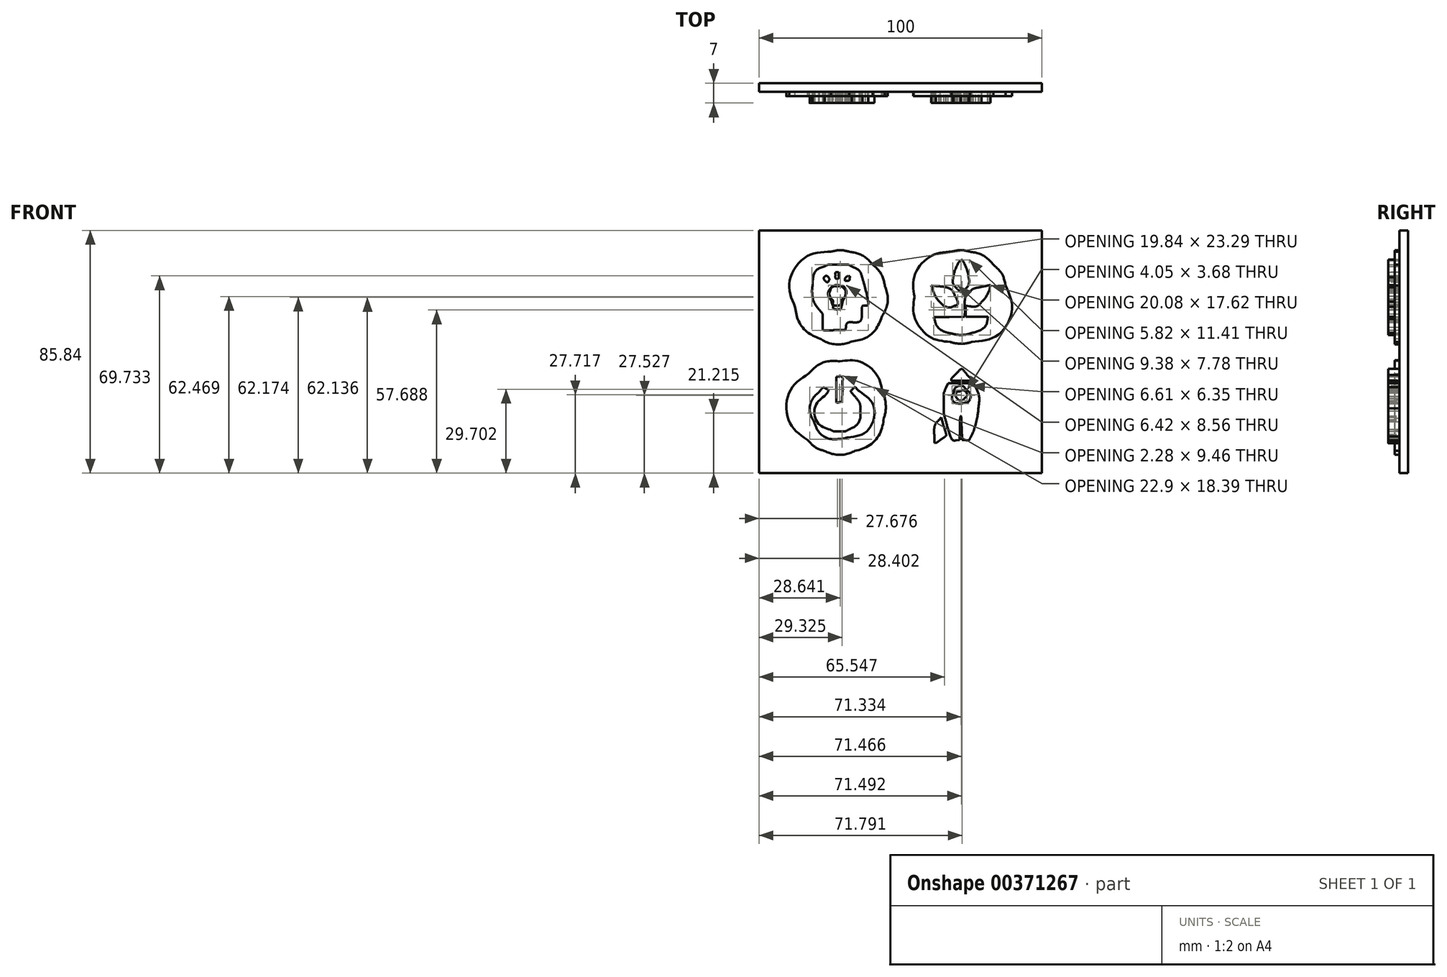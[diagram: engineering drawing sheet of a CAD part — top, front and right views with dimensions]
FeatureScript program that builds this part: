
annotation { "Feature Type Name" : "Feature", "Feature Type Description" : "" }
export const myFeature = defineFeature(function(context is Context, id is Id, definition is map)
    precondition{}
    {
        {
            var Q0;
            Q0=qCreatedBy(makeId("Front.planeOp"),FACE);
            var sketch = newSketch(context, id + "F0", { "sketchPlane" : qUnion([Q0])});
            skFitSpline(sketch, "E0", {"points": [v(-58.7, -58.7) * mm, v(-59.54, -57.85) * mm, v(-59.7, -57.5) * mm, v(-59.68, -56.5) * mm]});
            skLineSegment(sketch, "E1", {"start": v(-59.68, -56.5) * mm, "end": v(-59.65, -55.31) * mm});
            skLineSegment(sketch, "E2", {"start": v(-59.65, -55.31) * mm, "end": v(-59.39, -56.23) * mm});
            skFitSpline(sketch, "E3", {"points": [v(-59.39, -56.23) * mm, v(-59.05, -57.4) * mm, v(-57.42, -59.03) * mm, v(-56.24, -59.37) * mm]});
            skLineSegment(sketch, "E4", {"start": v(-56.24, -59.37) * mm, "end": v(-55.33, -59.64) * mm});
            skLineSegment(sketch, "E5", {"start": v(-55.33, -59.64) * mm, "end": v(-56.52, -59.66) * mm});
            skFitSpline(sketch, "E6", {"points": [v(-56.52, -59.66) * mm, v(-57.52, -59.68) * mm, v(-57.86, -59.53) * mm, v(-58.7, -58.7) * mm]});
            skFitSpline(sketch, "E7", {"points": [v(56.22, -59.37) * mm, v(56.72, -59.23) * mm, v(57.58, -58.67) * mm, v(58.12, -58.13) * mm]});
            skFitSpline(sketch, "E8", {"points": [v(58.12, -58.13) * mm, v(58.66, -57.59) * mm, v(59.22, -56.73) * mm, v(59.36, -56.23) * mm]});
            skLineSegment(sketch, "E9", {"start": v(59.36, -56.23) * mm, "end": v(59.63, -55.31) * mm});
            skLineSegment(sketch, "E10", {"start": v(59.63, -55.31) * mm, "end": v(59.65, -56.5) * mm});
            skFitSpline(sketch, "E11", {"points": [v(59.65, -56.5) * mm, v(59.67, -57.5) * mm, v(59.52, -57.85) * mm, v(58.68, -58.7) * mm]});
            skFitSpline(sketch, "E12", {"points": [v(58.68, -58.7) * mm, v(57.84, -59.53) * mm, v(57.5, -59.68) * mm, v(56.5, -59.66) * mm]});
            skLineSegment(sketch, "E13", {"start": v(56.5, -59.66) * mm, "end": v(55.3, -59.64) * mm});
            skLineSegment(sketch, "E14", {"start": v(55.3, -59.64) * mm, "end": v(56.22, -59.37) * mm});
            skFitSpline(sketch, "E15", {"points": [v(-25.98, -48.72) * mm, v(-28.66, -47.95) * mm, v(-31.18, -46.46) * mm, v(-33.19, -44.46) * mm]});
            skFitSpline(sketch, "E16", {"points": [v(-33.19, -44.46) * mm, v(-35.29, -42.37) * mm, v(-36.5, -40.4) * mm, v(-37.45, -37.53) * mm]});
            skFitSpline(sketch, "E17", {"points": [v(-37.45, -37.53) * mm, v(-38.36, -34.76) * mm, v(-38.36, -29.9) * mm, v(-37.43, -27.23) * mm]});
            skFitSpline(sketch, "E18", {"points": [v(-37.43, -27.23) * mm, v(-36.45, -24.4) * mm, v(-35.23, -22.47) * mm, v(-33.05, -20.32) * mm]});
            skFitSpline(sketch, "E19", {"points": [v(-33.05, -20.32) * mm, v(-29.86, -17.16) * mm, v(-26.18, -15.66) * mm, v(-21.6, -15.66) * mm]});
            skFitSpline(sketch, "E20", {"points": [v(-21.6, -15.66) * mm, v(-16.86, -15.66) * mm, v(-13.33, -17.12) * mm, v(-9.96, -20.48) * mm]});
            skFitSpline(sketch, "E21", {"points": [v(-9.96, -20.48) * mm, v(-6.62, -23.8) * mm, v(-4.95, -27.8) * mm, v(-4.95, -32.45) * mm]});
            skFitSpline(sketch, "E22", {"points": [v(-4.95, -32.45) * mm, v(-4.95, -40.1) * mm, v(-10.21, -46.96) * mm, v(-17.5, -48.82) * mm]});
            skFitSpline(sketch, "E23", {"points": [v(-17.5, -48.82) * mm, v(-19.73, -49.39) * mm, v(-23.82, -49.34) * mm, v(-25.98, -48.72) * mm]});
            skLineSegment(sketch, "E24", {"start": v(-25.98, -48.72) * mm, "end": v(-25.98, -48.72) * mm});
            skFitSpline(sketch, "E25", {"points": [v(-16.12, -47.82) * mm, v(-11.18, -45.97) * mm, v(-7.23, -41.5) * mm, v(-5.9, -36.27) * mm]});
            skFitSpline(sketch, "E26", {"points": [v(-5.9, -36.27) * mm, v(-5.29, -33.8) * mm, v(-5.5, -29.47) * mm, v(-6.36, -27.03) * mm]});
            skFitSpline(sketch, "E27", {"points": [v(-6.36, -27.03) * mm, v(-8.6, -20.64) * mm, v(-14.77, -16.18) * mm, v(-21.42, -16.16) * mm]});
            skFitSpline(sketch, "E28", {"points": [v(-21.42, -16.16) * mm, v(-25.68, -16.15) * mm, v(-29.35, -17.6) * mm, v(-32.46, -20.5) * mm]});
            skFitSpline(sketch, "E29", {"points": [v(-32.46, -20.5) * mm, v(-39.17, -26.79) * mm, v(-39.37, -37.44) * mm, v(-32.91, -43.9) * mm]});
            skFitSpline(sketch, "E30", {"points": [v(-32.91, -43.9) * mm, v(-30.85, -45.96) * mm, v(-29.24, -47) * mm, v(-26.78, -47.88) * mm]});
            skFitSpline(sketch, "E31", {"points": [v(-26.78, -47.88) * mm, v(-23.57, -49) * mm, v(-19.23, -48.98) * mm, v(-16.12, -47.82) * mm]});
            skFitSpline(sketch, "E32", {"points": [v(-23.93, -43.88) * mm, v(-26.91, -43.13) * mm, v(-29.78, -40.69) * mm, v(-31.13, -37.74) * mm]});
            skFitSpline(sketch, "E33", {"points": [v(-31.13, -37.74) * mm, v(-31.75, -36.39) * mm, v(-31.87, -35.7) * mm, v(-31.89, -33.58) * mm]});
            skFitSpline(sketch, "E34", {"points": [v(-31.89, -33.58) * mm, v(-31.9, -31.26) * mm, v(-31.82, -30.87) * mm, v(-30.99, -29.17) * mm]});
            skFitSpline(sketch, "E35", {"points": [v(-30.99, -29.17) * mm, v(-30.02, -27.21) * mm, v(-27.91, -24.98) * mm, v(-27.03, -24.98) * mm]});
            skFitSpline(sketch, "E36", {"points": [v(-27.03, -24.98) * mm, v(-26.75, -24.98) * mm, v(-26.24, -25.17) * mm, v(-25.9, -25.41) * mm]});
            skFitSpline(sketch, "E37", {"points": [v(-25.9, -25.41) * mm, v(-24.95, -26.08) * mm, v(-25.08, -27.3) * mm, v(-26.22, -28.57) * mm]});
            skFitSpline(sketch, "E38", {"points": [v(-26.22, -28.57) * mm, v(-27.8, -30.34) * mm, v(-28.22, -31.39) * mm, v(-28.22, -33.58) * mm]});
            skFitSpline(sketch, "E39", {"points": [v(-28.22, -33.58) * mm, v(-28.22, -36.4) * mm, v(-27.01, -38.46) * mm, v(-24.64, -39.68) * mm]});
            skFitSpline(sketch, "E40", {"points": [v(-24.64, -39.68) * mm, v(-20.27, -41.93) * mm, v(-14.86, -38.73) * mm, v(-14.83, -33.9) * mm]});
            skFitSpline(sketch, "E41", {"points": [v(-14.83, -33.9) * mm, v(-14.83, -31.88) * mm, v(-15.31, -30.57) * mm, v(-16.7, -28.88) * mm]});
            skFitSpline(sketch, "E42", {"points": [v(-16.7, -28.88) * mm, v(-18.06, -27.23) * mm, v(-18.22, -26.4) * mm, v(-17.37, -25.54) * mm]});
            skFitSpline(sketch, "E43", {"points": [v(-17.37, -25.54) * mm, v(-16.46, -24.64) * mm, v(-15.64, -24.84) * mm, v(-14.23, -26.32) * mm]});
            skFitSpline(sketch, "E44", {"points": [v(-14.23, -26.32) * mm, v(-12.61, -28.01) * mm, v(-12.17, -28.74) * mm, v(-11.6, -30.62) * mm]});
            skFitSpline(sketch, "E45", {"points": [v(-11.6, -30.62) * mm, v(-10.12, -35.63) * mm, v(-12.51, -40.87) * mm, v(-17.3, -43.11) * mm]});
            skFitSpline(sketch, "E46", {"points": [v(-17.3, -43.11) * mm, v(-19.3, -44.05) * mm, v(-22.01, -44.36) * mm, v(-23.93, -43.88) * mm]});
            skFitSpline(sketch, "E47", {"points": [v(-18.7, -43.01) * mm, v(-11.6, -40.62) * mm, v(-9.47, -32.06) * mm, v(-14.63, -26.74) * mm]});
            skFitSpline(sketch, "E48", {"points": [v(-14.63, -26.74) * mm, v(-15.9, -25.43) * mm, v(-16.25, -25.31) * mm, v(-16.92, -25.98) * mm]});
            skFitSpline(sketch, "E49", {"points": [v(-16.92, -25.98) * mm, v(-17.58, -26.64) * mm, v(-17.49, -26.95) * mm, v(-16.14, -28.6) * mm]});
            skFitSpline(sketch, "E50", {"points": [v(-16.14, -28.6) * mm, v(-14.75, -30.3) * mm, v(-14.26, -31.6) * mm, v(-14.26, -33.64) * mm]});
            skFitSpline(sketch, "E51", {"points": [v(-14.26, -33.64) * mm, v(-14.26, -36.4) * mm, v(-15.67, -38.8) * mm, v(-18.03, -40.11) * mm]});
            skFitSpline(sketch, "E52", {"points": [v(-18.03, -40.11) * mm, v(-19.27, -40.8) * mm, v(-19.8, -40.92) * mm, v(-21.6, -40.91) * mm]});
            skFitSpline(sketch, "E53", {"points": [v(-21.6, -40.91) * mm, v(-23.22, -40.9) * mm, v(-23.99, -40.76) * mm, v(-24.85, -40.3) * mm]});
            skFitSpline(sketch, "E54", {"points": [v(-24.85, -40.3) * mm, v(-29.26, -37.95) * mm, v(-30.25, -32.3) * mm, v(-26.94, -28.47) * mm]});
            skFitSpline(sketch, "E55", {"points": [v(-26.94, -28.47) * mm, v(-25.71, -27.06) * mm, v(-25.55, -26.27) * mm, v(-26.4, -25.82) * mm]});
            skFitSpline(sketch, "E56", {"points": [v(-26.4, -25.82) * mm, v(-27.12, -25.44) * mm, v(-27.72, -25.75) * mm, v(-28.94, -27.14) * mm]});
            skFitSpline(sketch, "E57", {"points": [v(-28.94, -27.14) * mm, v(-31.39, -29.92) * mm, v(-32.05, -34.14) * mm, v(-30.56, -37.44) * mm]});
            skFitSpline(sketch, "E58", {"points": [v(-30.56, -37.44) * mm, v(-28.9, -41.1) * mm, v(-25.4, -43.47) * mm, v(-21.52, -43.57) * mm]});
            skFitSpline(sketch, "E59", {"points": [v(-21.52, -43.57) * mm, v(-20.93, -43.59) * mm, v(-19.67, -43.34) * mm, v(-18.7, -43.01) * mm]});
            skFitSpline(sketch, "E60", {"points": [v(-22.83, -30.67) * mm, v(-23.22, -30.24) * mm, v(-23.3, -29.47) * mm, v(-23.3, -26.01) * mm]});
            skFitSpline(sketch, "E61", {"points": [v(-23.3, -26.01) * mm, v(-23.3, -22.25) * mm, v(-23.24, -21.82) * mm, v(-22.73, -21.3) * mm]});
            skFitSpline(sketch, "E62", {"points": [v(-22.73, -21.3) * mm, v(-22.03, -20.6) * mm, v(-20.99, -20.58) * mm, v(-20.38, -21.26) * mm]});
            skFitSpline(sketch, "E63", {"points": [v(-20.38, -21.26) * mm, v(-19.7, -22) * mm, v(-19.68, -30.07) * mm, v(-20.35, -30.74) * mm]});
            skFitSpline(sketch, "E64", {"points": [v(-20.35, -30.74) * mm, v(-20.95, -31.34) * mm, v(-22.25, -31.3) * mm, v(-22.83, -30.67) * mm]});
            skLineSegment(sketch, "E65", {"start": v(-22.83, -30.67) * mm, "end": v(-22.83, -30.67) * mm});
            skFitSpline(sketch, "E66", {"points": [v(-20.54, -26.22) * mm, v(-20.47, -22.64) * mm, v(-20.53, -21.9) * mm, v(-20.9, -21.59) * mm]});
            skFitSpline(sketch, "E67", {"points": [v(-20.9, -21.59) * mm, v(-21.23, -21.3) * mm, v(-21.5, -21.3) * mm, v(-22.03, -21.54) * mm]});
            skFitSpline(sketch, "E68", {"points": [v(-22.03, -21.54) * mm, v(-22.73, -21.86) * mm, v(-22.73, -21.88) * mm, v(-22.73, -25.9) * mm]});
            skFitSpline(sketch, "E69", {"points": [v(-22.73, -25.9) * mm, v(-22.73, -30.25) * mm, v(-22.6, -30.7) * mm, v(-21.32, -30.56) * mm]});
            skLineSegment(sketch, "E70", {"start": v(-21.32, -30.56) * mm, "end": v(-20.61, -30.48) * mm});
            skLineSegment(sketch, "E71", {"start": v(-20.61, -30.48) * mm, "end": v(-20.54, -26.22) * mm});
            skFitSpline(sketch, "E72", {"points": [v(17.06, -48.8) * mm, v(11.27, -47.27) * mm, v(6.44, -42.41) * mm, v(5.04, -36.7) * mm]});
            skFitSpline(sketch, "E73", {"points": [v(5.04, -36.7) * mm, v(4.1, -32.91) * mm, v(4.57, -28.18) * mm, v(6.19, -25) * mm]});
            skFitSpline(sketch, "E74", {"points": [v(6.19, -25) * mm, v(9.14, -19.16) * mm, v(14.82, -15.66) * mm, v(21.29, -15.67) * mm]});
            skFitSpline(sketch, "E75", {"points": [v(21.29, -15.67) * mm, v(26.13, -15.67) * mm, v(29.94, -17.24) * mm, v(33.3, -20.6) * mm]});
            skFitSpline(sketch, "E76", {"points": [v(33.3, -20.6) * mm, v(39.88, -27.18) * mm, v(39.86, -37.72) * mm, v(33.27, -44.35) * mm]});
            skFitSpline(sketch, "E77", {"points": [v(33.27, -44.35) * mm, v(31.06, -46.57) * mm, v(27.84, -48.36) * mm, v(25.02, -48.94) * mm]});
            skFitSpline(sketch, "E78", {"points": [v(25.02, -48.94) * mm, v(22.96, -49.36) * mm, v(18.93, -49.3) * mm, v(17.06, -48.8) * mm]});
            skFitSpline(sketch, "E79", {"points": [v(27.02, -47.73) * mm, v(34.74, -44.82) * mm, v(39.11, -36.66) * mm, v(37.23, -28.67) * mm]});
            skFitSpline(sketch, "E80", {"points": [v(37.23, -28.67) * mm, v(36.18, -24.21) * mm, v(32.7, -19.85) * mm, v(28.63, -17.87) * mm]});
            skFitSpline(sketch, "E81", {"points": [v(28.63, -17.87) * mm, v(25.96, -16.58) * mm, v(24.06, -16.14) * mm, v(21.14, -16.16) * mm]});
            skFitSpline(sketch, "E82", {"points": [v(21.14, -16.16) * mm, v(11.14, -16.2) * mm, v(3.3, -25.76) * mm, v(5.32, -35.42) * mm]});
            skFitSpline(sketch, "E83", {"points": [v(5.32, -35.42) * mm, v(7.42, -45.46) * mm, v(17.64, -51.26) * mm, v(27.02, -47.73) * mm]});
            skFitSpline(sketch, "E84", {"points": [v(11.53, -44.94) * mm, v(11.07, -43.55) * mm, v(11.32, -39.84) * mm, v(11.96, -38.34) * mm]});
            skFitSpline(sketch, "E85", {"points": [v(11.96, -38.34) * mm, v(12.66, -36.74) * mm, v(14, -35.27) * mm, v(14.58, -35.49) * mm]});
            skFitSpline(sketch, "E86", {"points": [v(14.58, -35.49) * mm, v(14.95, -35.63) * mm, v(16.47, -40.39) * mm, v(16.68, -42.05) * mm]});
            skFitSpline(sketch, "E87", {"points": [v(16.68, -42.05) * mm, v(16.78, -42.82) * mm, v(16.62, -43.01) * mm, v(14.82, -44.24) * mm]});
            skFitSpline(sketch, "E88", {"points": [v(14.82, -44.24) * mm, v(12.62, -45.73) * mm, v(11.84, -45.9) * mm, v(11.53, -44.94) * mm]});
            skFitSpline(sketch, "E89", {"points": [v(14.42, -43.7) * mm, v(15.69, -42.8) * mm, v(16.22, -42.25) * mm, v(16.13, -41.94) * mm]});
            skFitSpline(sketch, "E90", {"points": [v(16.13, -41.94) * mm, v(16.05, -41.69) * mm, v(15.63, -40.23) * mm, v(15.2, -38.7) * mm]});
            skLineSegment(sketch, "E91", {"start": v(15.2, -38.7) * mm, "end": v(14.4, -35.92) * mm});
            skLineSegment(sketch, "E92", {"start": v(14.4, -35.92) * mm, "end": v(13.47, -36.99) * mm});
            skFitSpline(sketch, "E93", {"points": [v(13.47, -36.99) * mm, v(12.33, -38.3) * mm, v(11.92, -39.74) * mm, v(11.92, -42.38) * mm]});
            skFitSpline(sketch, "E94", {"points": [v(11.92, -42.38) * mm, v(11.92, -44.24) * mm, v(12.07, -45.01) * mm, v(12.44, -45.01) * mm]});
            skFitSpline(sketch, "E95", {"points": [v(12.44, -45.01) * mm, v(12.52, -45.01) * mm, v(13.41, -44.42) * mm, v(14.42, -43.7) * mm]});
            skFitSpline(sketch, "E96", {"points": [v(27.82, -44.13) * mm, v(26.16, -42.96) * mm, v(25.79, -42.57) * mm, v(25.9, -42.08) * mm]});
            skFitSpline(sketch, "E97", {"points": [v(25.9, -42.08) * mm, v(26, -41.57) * mm, v(27.35, -36.77) * mm, v(27.66, -35.77) * mm]});
            skFitSpline(sketch, "E98", {"points": [v(27.66, -35.77) * mm, v(27.98, -34.75) * mm, v(29.6, -36) * mm, v(30.69, -38.1) * mm]});
            skFitSpline(sketch, "E99", {"points": [v(30.69, -38.1) * mm, v(31.37, -39.42) * mm, v(31.7, -43.55) * mm, v(31.2, -44.8) * mm]});
            skFitSpline(sketch, "E100", {"points": [v(31.2, -44.8) * mm, v(30.78, -45.9) * mm, v(30.17, -45.78) * mm, v(27.82, -44.13) * mm]});
            skFitSpline(sketch, "E101", {"points": [v(30.77, -43.72) * mm, v(31.03, -41.97) * mm, v(30.72, -39.55) * mm, v(30.06, -38.29) * mm]});
            skFitSpline(sketch, "E102", {"points": [v(30.06, -38.29) * mm, v(29.45, -37.1) * mm, v(28.27, -35.76) * mm, v(28.18, -36.15) * mm]});
            skFitSpline(sketch, "E103", {"points": [v(28.18, -36.15) * mm, v(27.97, -37.03) * mm, v(26.67, -41.56) * mm, v(26.53, -41.94) * mm]});
            skFitSpline(sketch, "E104", {"points": [v(26.53, -41.94) * mm, v(26.4, -42.26) * mm, v(26.87, -42.74) * mm, v(28.25, -43.7) * mm]});
            skFitSpline(sketch, "E105", {"points": [v(28.25, -43.7) * mm, v(29.3, -44.42) * mm, v(30.25, -45.01) * mm, v(30.37, -45.01) * mm]});
            skFitSpline(sketch, "E106", {"points": [v(30.37, -45.01) * mm, v(30.48, -45.01) * mm, v(30.66, -44.43) * mm, v(30.77, -43.72) * mm]});
            skFitSpline(sketch, "E107", {"points": [v(18.27, -43.83) * mm, v(17.92, -43.38) * mm, v(16.7, -39.78) * mm, v(15.86, -36.69) * mm]});
            skFitSpline(sketch, "E108", {"points": [v(15.86, -36.69) * mm, v(15.38, -34.94) * mm, v(15.24, -33.63) * mm, v(15.24, -30.9) * mm]});
            skFitSpline(sketch, "E109", {"points": [v(15.24, -30.9) * mm, v(15.23, -27.6) * mm, v(15.28, -27.26) * mm, v(16.04, -25.61) * mm]});
            skLineSegment(sketch, "E110", {"start": v(16.04, -25.61) * mm, "end": v(16.86, -23.85) * mm});
            skLineSegment(sketch, "E111", {"start": v(16.86, -23.85) * mm, "end": v(21.35, -23.85) * mm});
            skLineSegment(sketch, "E112", {"start": v(21.35, -23.85) * mm, "end": v(25.84, -23.85) * mm});
            skLineSegment(sketch, "E113", {"start": v(25.84, -23.85) * mm, "end": v(26.52, -25.33) * mm});
            skFitSpline(sketch, "E114", {"points": [v(26.52, -25.33) * mm, v(27.5, -27.49) * mm, v(27.81, -29.9) * mm, v(27.48, -32.82) * mm]});
            skFitSpline(sketch, "E115", {"points": [v(27.48, -32.82) * mm, v(27.18, -35.55) * mm, v(25.8, -40.8) * mm, v(24.86, -42.76) * mm]});
            skFitSpline(sketch, "E116", {"points": [v(24.86, -42.76) * mm, v(24.28, -43.98) * mm, v(24.22, -44.03) * mm, v(22.99, -44.03) * mm]});
            skLineSegment(sketch, "E117", {"start": v(22.99, -44.03) * mm, "end": v(21.72, -44.03) * mm});
            skLineSegment(sketch, "E118", {"start": v(21.72, -44.03) * mm, "end": v(21.58, -39.65) * mm});
            skFitSpline(sketch, "E119", {"points": [v(21.58, -39.65) * mm, v(21.5, -37.25) * mm, v(21.34, -35.47) * mm, v(21.23, -35.7) * mm]});
            skFitSpline(sketch, "E120", {"points": [v(21.23, -35.7) * mm, v(21.11, -35.93) * mm, v(20.99, -37.9) * mm, v(20.95, -40.07) * mm]});
            skLineSegment(sketch, "E121", {"start": v(20.95, -40.07) * mm, "end": v(20.87, -44.03) * mm});
            skLineSegment(sketch, "E122", {"start": v(20.87, -44.03) * mm, "end": v(19.72, -44.1) * mm});
            skFitSpline(sketch, "E123", {"points": [v(19.72, -44.1) * mm, v(19.02, -44.16) * mm, v(18.45, -44.05) * mm, v(18.27, -43.83) * mm]});
            skFitSpline(sketch, "E124", {"points": [v(20.45, -39.54) * mm, v(20.45, -36.3) * mm, v(20.53, -35.42) * mm, v(20.87, -35.14) * mm]});
            skFitSpline(sketch, "E125", {"points": [v(20.87, -35.14) * mm, v(21.1, -34.95) * mm, v(21.48, -34.86) * mm, v(21.72, -34.95) * mm]});
            skFitSpline(sketch, "E126", {"points": [v(21.72, -34.95) * mm, v(22.07, -35.1) * mm, v(22.14, -35.83) * mm, v(22.14, -39.36) * mm]});
            skLineSegment(sketch, "E127", {"start": v(22.14, -39.36) * mm, "end": v(22.14, -43.6) * mm});
            skLineSegment(sketch, "E128", {"start": v(22.14, -43.6) * mm, "end": v(23, -43.6) * mm});
            skFitSpline(sketch, "E129", {"points": [v(23, -43.6) * mm, v(23.74, -43.6) * mm, v(23.93, -43.44) * mm, v(24.37, -42.4) * mm]});
            skFitSpline(sketch, "E130", {"points": [v(24.37, -42.4) * mm, v(24.65, -41.74) * mm, v(25.14, -40.31) * mm, v(25.47, -39.23) * mm]});
            skFitSpline(sketch, "E131", {"points": [v(25.47, -39.23) * mm, v(27.32, -33.08) * mm, v(27.49, -29.12) * mm, v(26.05, -25.78) * mm]});
            skLineSegment(sketch, "E132", {"start": v(26.05, -25.78) * mm, "end": v(25.46, -24.41) * mm});
            skLineSegment(sketch, "E133", {"start": v(25.46, -24.41) * mm, "end": v(21.39, -24.41) * mm});
            skLineSegment(sketch, "E134", {"start": v(21.39, -24.41) * mm, "end": v(17.31, -24.41) * mm});
            skLineSegment(sketch, "E135", {"start": v(17.31, -24.41) * mm, "end": v(16.55, -26.03) * mm});
            skFitSpline(sketch, "E136", {"points": [v(16.55, -26.03) * mm, v(15.86, -27.5) * mm, v(15.8, -27.95) * mm, v(15.8, -30.9) * mm]});
            skFitSpline(sketch, "E137", {"points": [v(15.8, -30.9) * mm, v(15.82, -34.17) * mm, v(16.24, -36.36) * mm, v(17.63, -40.5) * mm]});
            skFitSpline(sketch, "E138", {"points": [v(17.63, -40.5) * mm, v(18.67, -43.6) * mm, v(18.68, -43.6) * mm, v(19.6, -43.6) * mm]});
            skLineSegment(sketch, "E139", {"start": v(19.6, -43.6) * mm, "end": v(20.45, -43.6) * mm});
            skLineSegment(sketch, "E140", {"start": v(20.45, -43.6) * mm, "end": v(20.45, -39.54) * mm});
            skFitSpline(sketch, "E141", {"points": [v(20.17, -31.55) * mm, v(19.3, -31.24) * mm, v(18.2, -29.93) * mm, v(18.03, -29.04) * mm]});
            skFitSpline(sketch, "E142", {"points": [v(18.03, -29.04) * mm, v(17.6, -26.78) * mm, v(19.12, -24.98) * mm, v(21.44, -24.98) * mm]});
            skFitSpline(sketch, "E143", {"points": [v(21.44, -24.98) * mm, v(22.57, -24.98) * mm, v(22.9, -25.12) * mm, v(23.72, -25.93) * mm]});
            skFitSpline(sketch, "E144", {"points": [v(23.72, -25.93) * mm, v(24.5, -26.72) * mm, v(24.68, -27.11) * mm, v(24.68, -28.07) * mm]});
            skFitSpline(sketch, "E145", {"points": [v(24.68, -28.07) * mm, v(24.68, -28.7) * mm, v(24.5, -29.6) * mm, v(24.27, -30.03) * mm]});
            skFitSpline(sketch, "E146", {"points": [v(24.27, -30.03) * mm, v(23.62, -31.29) * mm, v(21.55, -32.05) * mm, v(20.17, -31.55) * mm]});
            skFitSpline(sketch, "E147", {"points": [v(22.4, -30.87) * mm, v(24.2, -30.24) * mm, v(24.7, -27.76) * mm, v(23.3, -26.36) * mm]});
            skFitSpline(sketch, "E148", {"points": [v(23.3, -26.36) * mm, v(21.82, -24.9) * mm, v(19.4, -25.43) * mm, v(18.76, -27.37) * mm]});
            skFitSpline(sketch, "E149", {"points": [v(18.76, -27.37) * mm, v(18.14, -29.25) * mm, v(19.14, -30.73) * mm, v(21.32, -31.15) * mm]});
            skFitSpline(sketch, "E150", {"points": [v(21.32, -31.15) * mm, v(21.42, -31.17) * mm, v(21.9, -31.04) * mm, v(22.4, -30.87) * mm]});
            skFitSpline(sketch, "E151", {"points": [v(20.54, -30.33) * mm, v(19.62, -29.97) * mm, v(18.94, -28.78) * mm, v(19.16, -27.93) * mm]});
            skFitSpline(sketch, "E152", {"points": [v(19.16, -27.93) * mm, v(19.6, -26.13) * mm, v(21.59, -25.52) * mm, v(22.86, -26.8) * mm]});
            skFitSpline(sketch, "E153", {"points": [v(22.86, -26.8) * mm, v(23.85, -27.78) * mm, v(23.78, -28.97) * mm, v(22.69, -29.89) * mm]});
            skFitSpline(sketch, "E154", {"points": [v(22.69, -29.89) * mm, v(21.76, -30.67) * mm, v(21.5, -30.72) * mm, v(20.54, -30.33) * mm]});
            skFitSpline(sketch, "E155", {"points": [v(22.56, -29.22) * mm, v(23.55, -28.12) * mm, v(22.37, -26.4) * mm, v(20.87, -26.79) * mm]});
            skFitSpline(sketch, "E156", {"points": [v(20.87, -26.79) * mm, v(19.87, -27.04) * mm, v(19.5, -28.54) * mm, v(20.23, -29.42) * mm]});
            skFitSpline(sketch, "E157", {"points": [v(20.23, -29.42) * mm, v(20.67, -29.96) * mm, v(22, -29.84) * mm, v(22.56, -29.22) * mm]});
            skFitSpline(sketch, "E158", {"points": [v(17.9, -22.64) * mm, v(17.9, -22.44) * mm, v(18.6, -21.6) * mm, v(19.44, -20.77) * mm]});
            skFitSpline(sketch, "E159", {"points": [v(19.44, -20.77) * mm, v(21.28, -18.95) * mm, v(21.8, -18.97) * mm, v(23.53, -20.92) * mm]});
            skFitSpline(sketch, "E160", {"points": [v(23.53, -20.92) * mm, v(25.3, -22.93) * mm, v(25.22, -23) * mm, v(21.3, -23) * mm]});
            skFitSpline(sketch, "E161", {"points": [v(21.3, -23) * mm, v(18.73, -23) * mm, v(17.9, -22.91) * mm, v(17.9, -22.64) * mm]});
            skFitSpline(sketch, "E162", {"points": [v(23.57, -21.9) * mm, v(23.26, -21.33) * mm, v(21.67, -19.9) * mm, v(21.33, -19.9) * mm]});
            skFitSpline(sketch, "E163", {"points": [v(21.33, -19.9) * mm, v(21.22, -19.9) * mm, v(20.57, -20.47) * mm, v(19.89, -21.17) * mm]});
            skLineSegment(sketch, "E164", {"start": v(19.89, -21.17) * mm, "end": v(18.64, -22.44) * mm});
            skLineSegment(sketch, "E165", {"start": v(18.64, -22.44) * mm, "end": v(21.25, -22.44) * mm});
            skFitSpline(sketch, "E166", {"points": [v(21.25, -22.44) * mm, v(23.72, -22.44) * mm, v(23.84, -22.4) * mm, v(23.57, -21.9) * mm]});
            skFitSpline(sketch, "E167", {"points": [v(-24.14, -10.12) * mm, v(-30.9, -8.81) * mm, v(-36.45, -3.46) * mm, v(-37.83, 3.1) * mm]});
            skFitSpline(sketch, "E168", {"points": [v(-37.83, 3.1) * mm, v(-39.6, 11.57) * mm, v(-34.76, 19.95) * mm, v(-26.54, 22.62) * mm]});
            skFitSpline(sketch, "E169", {"points": [v(-26.54, 22.62) * mm, v(-23.33, 23.66) * mm, v(-19.3, 23.66) * mm, v(-16.1, 22.62) * mm]});
            skFitSpline(sketch, "E170", {"points": [v(-16.1, 22.62) * mm, v(-10.86, 20.92) * mm, v(-6.97, 16.98) * mm, v(-5.2, 11.57) * mm]});
            skFitSpline(sketch, "E171", {"points": [v(-5.2, 11.57) * mm, v(-4.3, 8.84) * mm, v(-4.28, 4.52) * mm, v(-5.16, 1.7) * mm]});
            skFitSpline(sketch, "E172", {"points": [v(-5.16, 1.7) * mm, v(-6.75, -3.44) * mm, v(-10.65, -7.45) * mm, v(-15.89, -9.38) * mm]});
            skFitSpline(sketch, "E173", {"points": [v(-15.89, -9.38) * mm, v(-17.32, -9.9) * mm, v(-18.49, -10.1) * mm, v(-20.61, -10.17) * mm]});
            skFitSpline(sketch, "E174", {"points": [v(-20.61, -10.17) * mm, v(-22.17, -10.22) * mm, v(-23.75, -10.2) * mm, v(-24.14, -10.12) * mm]});
            skFitSpline(sketch, "E175", {"points": [v(-17.25, -9.18) * mm, v(-12.55, -7.98) * mm, v(-8.8, -4.9) * mm, v(-6.65, -0.5) * mm]});
            skFitSpline(sketch, "E176", {"points": [v(-6.65, -0.5) * mm, v(-4.94, 3.03) * mm, v(-4.55, 6.68) * mm, v(-5.5, 10.42) * mm]});
            skFitSpline(sketch, "E177", {"points": [v(-5.5, 10.42) * mm, v(-6.3, 13.52) * mm, v(-7.59, 15.77) * mm, v(-9.88, 18.09) * mm]});
            skFitSpline(sketch, "E178", {"points": [v(-9.88, 18.09) * mm, v(-12.18, 20.4) * mm, v(-14.94, 21.92) * mm, v(-18.07, 22.58) * mm]});
            skFitSpline(sketch, "E179", {"points": [v(-18.07, 22.58) * mm, v(-20.56, 23.1) * mm, v(-22.07, 23.1) * mm, v(-24.56, 22.58) * mm]});
            skFitSpline(sketch, "E180", {"points": [v(-24.56, 22.58) * mm, v(-33.48, 20.7) * mm, v(-39.3, 11.7) * mm, v(-37.25, 2.99) * mm]});
            skFitSpline(sketch, "E181", {"points": [v(-37.25, 2.99) * mm, v(-36.15, -1.7) * mm, v(-32.86, -5.9) * mm, v(-28.57, -8.09) * mm]});
            skFitSpline(sketch, "E182", {"points": [v(-28.57, -8.09) * mm, v(-25.44, -9.68) * mm, v(-20.93, -10.12) * mm, v(-17.25, -9.18) * mm]});
            skFitSpline(sketch, "E183", {"points": [v(-27.75, -5.45) * mm, v(-27.97, -5.23) * mm, v(-28.1, -4.12) * mm, v(-28.1, -2.36) * mm]});
            skLineSegment(sketch, "E184", {"start": v(-28.1, -2.36) * mm, "end": v(-28.1, 0.38) * mm});
            skLineSegment(sketch, "E185", {"start": v(-28.1, 0.38) * mm, "end": v(-29.35, 1.86) * mm});
            skFitSpline(sketch, "E186", {"points": [v(-29.23, 16.61) * mm, v(-27.47, 18.2) * mm, v(-25.92, 18.63) * mm, v(-21.88, 18.63) * mm]});
            skFitSpline(sketch, "E187", {"points": [v(-21.88, 18.63) * mm, v(-18.7, 18.63) * mm, v(-18.22, 18.56) * mm, v(-16.96, 17.93) * mm]});
            skFitSpline(sketch, "E188", {"points": [v(-16.96, 17.93) * mm, v(-13.75, 16.35) * mm, v(-12.97, 14.84) * mm, v(-11.56, 7.6) * mm]});
            skFitSpline(sketch, "E189", {"points": [v(-11.56, 7.6) * mm, v(-10.77, 3.5) * mm, v(-10.84, 2.96) * mm, v(-12.15, 2.96) * mm]});
            skFitSpline(sketch, "E190", {"points": [v(-12.15, 2.96) * mm, v(-12.83, 2.96) * mm, v(-13.13, 2.13) * mm, v(-13.13, 0.3) * mm]});
            skFitSpline(sketch, "E191", {"points": [v(-13.13, 0.3) * mm, v(-13.13, -0.98) * mm, v(-13.66, -2.36) * mm, v(-14.27, -2.69) * mm]});
            skFitSpline(sketch, "E192", {"points": [v(-14.27, -2.69) * mm, v(-14.56, -2.84) * mm, v(-15.49, -2.96) * mm, v(-16.34, -2.96) * mm]});
            skFitSpline(sketch, "E193", {"points": [v(-16.34, -2.96) * mm, v(-18.05, -2.96) * mm, v(-18.78, -3.42) * mm, v(-18.78, -4.48) * mm]});
            skFitSpline(sketch, "E194", {"points": [v(-18.78, -4.48) * mm, v(-18.78, -5.66) * mm, v(-19.23, -5.78) * mm, v(-23.44, -5.78) * mm]});
            skFitSpline(sketch, "E195", {"points": [v(-23.44, -5.78) * mm, v(-26.15, -5.78) * mm, v(-27.52, -5.68) * mm, v(-27.75, -5.45) * mm]});
            skFitSpline(sketch, "E196", {"points": [v(-19.3, -4.1) * mm, v(-19.04, -2.8) * mm, v(-18.4, -2.4) * mm, v(-16.54, -2.4) * mm]});
            skFitSpline(sketch, "E197", {"points": [v(-16.54, -2.4) * mm, v(-15.68, -2.4) * mm, v(-14.82, -2.3) * mm, v(-14.63, -2.18) * mm]});
            skFitSpline(sketch, "E198", {"points": [v(-14.63, -2.18) * mm, v(-14.11, -1.84) * mm, v(-13.7, -0.5) * mm, v(-13.7, 0.85) * mm]});
            skFitSpline(sketch, "E199", {"points": [v(-13.7, 0.85) * mm, v(-13.7, 2.65) * mm, v(-13.3, 3.53) * mm, v(-12.45, 3.53) * mm]});
            skFitSpline(sketch, "E200", {"points": [v(-12.45, 3.53) * mm, v(-12.07, 3.53) * mm, v(-11.7, 3.62) * mm, v(-11.63, 3.74) * mm]});
            skFitSpline(sketch, "E201", {"points": [v(-11.63, 3.74) * mm, v(-11.44, 4.04) * mm, v(-12.73, 10.63) * mm, v(-13.42, 12.91) * mm]});
            skFitSpline(sketch, "E202", {"points": [v(-13.42, 12.91) * mm, v(-14.08, 15.1) * mm, v(-15.15, 16.35) * mm, v(-17.27, 17.39) * mm]});
            skFitSpline(sketch, "E203", {"points": [v(-17.27, 17.39) * mm, v(-18.48, 17.99) * mm, v(-19.02, 18.06) * mm, v(-22.02, 18.06) * mm]});
            skFitSpline(sketch, "E204", {"points": [v(-22.02, 18.06) * mm, v(-24.96, 18.06) * mm, v(-25.6, 17.97) * mm, v(-26.86, 17.4) * mm]});
            skFitSpline(sketch, "E205", {"points": [v(-26.86, 17.4) * mm, v(-29.59, 16.17) * mm, v(-30.75, 14.3) * mm, v(-31.1, 10.59) * mm]});
            skFitSpline(sketch, "E206", {"points": [v(-31.1, 10.59) * mm, v(-31.29, 8.53) * mm, v(-30.84, 5.32) * mm, v(-30.2, 4.07) * mm]});
            skFitSpline(sketch, "E207", {"points": [v(-30.2, 4.07) * mm, v(-29.98, 3.64) * mm, v(-29.28, 2.7) * mm, v(-28.66, 1.98) * mm]});
            skLineSegment(sketch, "E208", {"start": v(-28.66, 1.98) * mm, "end": v(-27.53, 0.67) * mm});
            skLineSegment(sketch, "E209", {"start": v(-27.53, 0.67) * mm, "end": v(-27.53, -2.09) * mm});
            skFitSpline(sketch, "E210", {"points": [v(-27.53, -2.09) * mm, v(-27.53, -3.6) * mm, v(-27.44, -4.93) * mm, v(-27.33, -5.04) * mm]});
            skFitSpline(sketch, "E211", {"points": [v(-27.33, -5.04) * mm, v(-27.22, -5.15) * mm, v(-25.42, -5.2) * mm, v(-23.32, -5.16) * mm]});
            skLineSegment(sketch, "E212", {"start": v(-23.32, -5.16) * mm, "end": v(-19.5, -5.08) * mm});
            skLineSegment(sketch, "E213", {"start": v(-19.5, -5.08) * mm, "end": v(-19.3, -4.1) * mm});
            skFitSpline(sketch, "E214", {"points": [v(-23.7, 1.43) * mm, v(-23.94, 1.68) * mm, v(-24.14, 2.06) * mm, v(-24.14, 2.28) * mm]});
            skFitSpline(sketch, "E215", {"points": [v(-24.14, 2.28) * mm, v(-24.14, 2.5) * mm, v(-24.25, 2.68) * mm, v(-24.39, 2.68) * mm]});
            skFitSpline(sketch, "E216", {"points": [v(-24.39, 2.68) * mm, v(-24.53, 2.68) * mm, v(-24.8, 3.1) * mm, v(-24.98, 3.6) * mm]});
            skFitSpline(sketch, "E217", {"points": [v(-24.98, 3.6) * mm, v(-25.17, 4.1) * mm, v(-25.57, 4.98) * mm, v(-25.86, 5.54) * mm]});
            skFitSpline(sketch, "E218", {"points": [v(-25.86, 5.54) * mm, v(-27.37, 8.42) * mm, v(-25.58, 11.7) * mm, v(-22.5, 11.71) * mm]});
            skFitSpline(sketch, "E219", {"points": [v(-22.5, 11.71) * mm, v(-20.97, 11.71) * mm, v(-19.75, 11.1) * mm, v(-19.05, 9.94) * mm]});
            skFitSpline(sketch, "E220", {"points": [v(-19.05, 9.94) * mm, v(-18.32, 8.74) * mm, v(-18.33, 6.77) * mm, v(-19.06, 5.57) * mm]});
            skFitSpline(sketch, "E221", {"points": [v(-19.06, 5.57) * mm, v(-19.37, 5.06) * mm, v(-19.63, 4.42) * mm, v(-19.63, 4.14) * mm]});
            skFitSpline(sketch, "E222", {"points": [v(-19.63, 4.14) * mm, v(-19.63, 3.86) * mm, v(-19.88, 3.36) * mm, v(-20.2, 3.03) * mm]});
            skFitSpline(sketch, "E223", {"points": [v(-20.2, 3.03) * mm, v(-20.5, 2.7) * mm, v(-20.75, 2.3) * mm, v(-20.75, 2.15) * mm]});
            skFitSpline(sketch, "E224", {"points": [v(-20.75, 2.15) * mm, v(-20.75, 1.6) * mm, v(-21.66, 0.99) * mm, v(-22.45, 0.99) * mm]});
            skFitSpline(sketch, "E225", {"points": [v(-22.45, 0.99) * mm, v(-22.9, 0.99) * mm, v(-23.45, 1.19) * mm, v(-23.7, 1.43) * mm]});
            skFitSpline(sketch, "E226", {"points": [v(-21.38, 2.47) * mm, v(-21.17, 2.9) * mm, v(-20.89, 3.25) * mm, v(-20.74, 3.25) * mm]});
            skFitSpline(sketch, "E227", {"points": [v(-20.74, 3.25) * mm, v(-20.6, 3.25) * mm, v(-20.47, 3.4) * mm, v(-20.47, 3.57) * mm]});
            skFitSpline(sketch, "E228", {"points": [v(-20.47, 3.57) * mm, v(-20.47, 3.77) * mm, v(-20.68, 3.71) * mm, v(-20.99, 3.43) * mm]});
            skFitSpline(sketch, "E229", {"points": [v(-20.99, 3.43) * mm, v(-21.27, 3.17) * mm, v(-21.93, 2.96) * mm, v(-22.45, 2.96) * mm]});
            skFitSpline(sketch, "E230", {"points": [v(-23.9, 3.43) * mm, v(-24.2, 3.69) * mm, v(-24.42, 3.77) * mm, v(-24.42, 3.6) * mm]});
            skFitSpline(sketch, "E231", {"points": [v(-24.42, 3.6) * mm, v(-24.42, 3.44) * mm, v(-24.23, 3.23) * mm, v(-24, 3.14) * mm]});
            skFitSpline(sketch, "E232", {"points": [v(-24, 3.14) * mm, v(-23.77, 3.06) * mm, v(-23.58, 2.81) * mm, v(-23.58, 2.6) * mm]});
            skFitSpline(sketch, "E233", {"points": [v(-23.58, 2.6) * mm, v(-23.58, 1.38) * mm, v(-21.94, 1.28) * mm, v(-21.38, 2.47) * mm]});
            skFitSpline(sketch, "E234", {"points": [v(-21.38, 3.87) * mm, v(-21.19, 4.05) * mm, v(-21.04, 4.44) * mm, v(-21.04, 4.73) * mm]});
            skFitSpline(sketch, "E235", {"points": [v(-21.04, 4.73) * mm, v(-21.04, 5.01) * mm, v(-20.8, 5.59) * mm, v(-20.49, 6) * mm]});
            skFitSpline(sketch, "E236", {"points": [v(-20.49, 6) * mm, v(-19.12, 7.92) * mm, v(-20.16, 10.3) * mm, v(-22.37, 10.3) * mm]});
            skFitSpline(sketch, "E237", {"points": [v(-22.37, 10.3) * mm, v(-23.7, 10.3) * mm, v(-24.4, 9.86) * mm, v(-24.87, 8.73) * mm]});
            skFitSpline(sketch, "E238", {"points": [v(-24.87, 8.73) * mm, v(-25.22, 7.9) * mm, v(-25.22, 7.63) * mm, v(-24.88, 6.8) * mm]});
            skFitSpline(sketch, "E239", {"points": [v(-24.88, 6.8) * mm, v(-24.66, 6.28) * mm, v(-24.34, 5.77) * mm, v(-24.17, 5.66) * mm]});
            skFitSpline(sketch, "E240", {"points": [v(-24.17, 5.66) * mm, v(-24, 5.56) * mm, v(-23.86, 5.19) * mm, v(-23.86, 4.84) * mm]});
            skFitSpline(sketch, "E241", {"points": [v(-23.86, 4.84) * mm, v(-23.86, 4) * mm, v(-23.35, 3.53) * mm, v(-22.45, 3.53) * mm]});
            skFitSpline(sketch, "E242", {"points": [v(-22.45, 3.53) * mm, v(-22.04, 3.53) * mm, v(-21.56, 3.68) * mm, v(-21.38, 3.87) * mm]});
            skLineSegment(sketch, "E243", {"start": v(-21.38, 3.87) * mm, "end": v(-21.38, 3.87) * mm});
            skFitSpline(sketch, "E244", {"points": [v(-24.82, 5.4) * mm, v(-25.07, 5.61) * mm, v(-25.14, 5.64) * mm, v(-24.99, 5.45) * mm]});
            skFitSpline(sketch, "E245", {"points": [v(-24.99, 5.45) * mm, v(-24.83, 5.26) * mm, v(-24.7, 4.85) * mm, v(-24.67, 4.53) * mm]});
            skFitSpline(sketch, "E246", {"points": [v(-24.67, 4.53) * mm, v(-24.64, 4) * mm, v(-24.63, 4) * mm, v(-24.5, 4.48) * mm]});
            skFitSpline(sketch, "E247", {"points": [v(-24.5, 4.48) * mm, v(-24.43, 4.77) * mm, v(-24.57, 5.18) * mm, v(-24.82, 5.4) * mm]});
            skFitSpline(sketch, "E248", {"points": [v(-19.8, 5.5) * mm, v(-19.53, 5.87) * mm, v(-19.55, 5.88) * mm, v(-19.98, 5.54) * mm]});
            skFitSpline(sketch, "E249", {"points": [v(-19.98, 5.54) * mm, v(-20.25, 5.33) * mm, v(-20.46, 4.88) * mm, v(-20.44, 4.55) * mm]});
            skFitSpline(sketch, "E250", {"points": [v(-20.44, 4.55) * mm, v(-20.4, 3.98) * mm, v(-20.4, 3.98) * mm, v(-20.27, 4.52) * mm]});
            skFitSpline(sketch, "E251", {"points": [v(-20.27, 4.52) * mm, v(-20.2, 4.83) * mm, v(-19.98, 5.27) * mm, v(-19.8, 5.5) * mm]});
            skFitSpline(sketch, "E252", {"points": [v(-19.15, 8.66) * mm, v(-19.24, 8.89) * mm, v(-19.3, 8.82) * mm, v(-19.32, 8.5) * mm]});
            skFitSpline(sketch, "E253", {"points": [v(-19.32, 8.5) * mm, v(-19.33, 8.2) * mm, v(-19.27, 8.03) * mm, v(-19.17, 8.12) * mm]});
            skFitSpline(sketch, "E254", {"points": [v(-19.17, 8.12) * mm, v(-19.08, 8.21) * mm, v(-19.07, 8.46) * mm, v(-19.15, 8.66) * mm]});
            skLineSegment(sketch, "E255", {"start": v(-19.15, 8.66) * mm, "end": v(-19.15, 8.66) * mm});
            skFitSpline(sketch, "E256", {"points": [v(-24.23, 10.48) * mm, v(-23.75, 10.87) * mm, v(-23.76, 10.88) * mm, v(-24.35, 10.6) * mm]});
            skFitSpline(sketch, "E257", {"points": [v(-24.35, 10.6) * mm, v(-24.7, 10.43) * mm, v(-25.11, 10) * mm, v(-25.28, 9.66) * mm]});
            skFitSpline(sketch, "E258", {"points": [v(-25.28, 9.66) * mm, v(-25.56, 9.08) * mm, v(-25.55, 9.07) * mm, v(-25.17, 9.55) * mm]});
            skFitSpline(sketch, "E259", {"points": [v(-25.17, 9.55) * mm, v(-24.94, 9.83) * mm, v(-24.52, 10.25) * mm, v(-24.23, 10.48) * mm]});
            skFitSpline(sketch, "E260", {"points": [v(-19.62, 9.73) * mm, v(-19.79, 10.04) * mm, v(-20.2, 10.44) * mm, v(-20.54, 10.62) * mm]});
            skFitSpline(sketch, "E261", {"points": [v(-20.54, 10.62) * mm, v(-21.02, 10.88) * mm, v(-20.98, 10.76) * mm, v(-20.32, 10.07) * mm]});
            skFitSpline(sketch, "E262", {"points": [v(-20.32, 10.07) * mm, v(-19.33, 9.04) * mm, v(-19.22, 8.99) * mm, v(-19.62, 9.73) * mm]});
            skFitSpline(sketch, "E263", {"points": [v(-21.4, 11.04) * mm, v(-21.49, 11.13) * mm, v(-21.73, 11.14) * mm, v(-21.94, 11.06) * mm]});
            skFitSpline(sketch, "E264", {"points": [v(-21.94, 11.06) * mm, v(-22.16, 10.97) * mm, v(-22.1, 10.9) * mm, v(-21.77, 10.89) * mm]});
            skFitSpline(sketch, "E265", {"points": [v(-21.77, 10.89) * mm, v(-21.47, 10.88) * mm, v(-21.3, 10.94) * mm, v(-21.4, 11.04) * mm]});
            skLineSegment(sketch, "E266", {"start": v(-21.4, 11.04) * mm, "end": v(-21.4, 11.04) * mm});
            skFitSpline(sketch, "E267", {"points": [v(-26.62, 12.33) * mm, v(-27.05, 12.76) * mm, v(-27.06, 13.6) * mm, v(-26.65, 13.85) * mm]});
            skFitSpline(sketch, "E268", {"points": [v(-26.65, 13.85) * mm, v(-26.2, 14.12) * mm, v(-25.16, 12.98) * mm, v(-25.36, 12.44) * mm]});
            skFitSpline(sketch, "E269", {"points": [v(-25.36, 12.44) * mm, v(-25.57, 11.91) * mm, v(-26.15, 11.86) * mm, v(-26.62, 12.33) * mm]});
            skFitSpline(sketch, "E270", {"points": [v(-19.63, 12.64) * mm, v(-19.63, 13.11) * mm, v(-18.74, 13.97) * mm, v(-18.24, 13.97) * mm]});
            skFitSpline(sketch, "E271", {"points": [v(-18.24, 13.97) * mm, v(-18.03, 13.97) * mm, v(-17.93, 13.67) * mm, v(-17.98, 13.2) * mm]});
            skFitSpline(sketch, "E272", {"points": [v(-17.98, 13.2) * mm, v(-18.05, 12.59) * mm, v(-18.24, 12.4) * mm, v(-18.85, 12.33) * mm]});
            skFitSpline(sketch, "E273", {"points": [v(-18.85, 12.33) * mm, v(-19.37, 12.27) * mm, v(-19.63, 12.37) * mm, v(-19.63, 12.64) * mm]});
            skFitSpline(sketch, "E274", {"points": [v(-23.01, 14.25) * mm, v(-23.01, 15.2) * mm, v(-22.92, 15.38) * mm, v(-22.45, 15.38) * mm]});
            skFitSpline(sketch, "E275", {"points": [v(-22.45, 15.38) * mm, v(-21.98, 15.38) * mm, v(-21.88, 15.2) * mm, v(-21.88, 14.25) * mm]});
            skFitSpline(sketch, "E276", {"points": [v(-21.88, 14.25) * mm, v(-21.88, 13.31) * mm, v(-21.98, 13.12) * mm, v(-22.45, 13.12) * mm]});
            skFitSpline(sketch, "E277", {"points": [v(-22.45, 13.12) * mm, v(-22.92, 13.12) * mm, v(-23.01, 13.31) * mm, v(-23.01, 14.25) * mm]});
            skFitSpline(sketch, "E278", {"points": [v(17.12, -9.73) * mm, v(11.51, -8.26) * mm, v(7.08, -4.08) * mm, v(5.32, 1.41) * mm]});
            skFitSpline(sketch, "E279", {"points": [v(5.32, 1.41) * mm, v(4.4, 4.25) * mm, v(4.29, 8.38) * mm, v(5.05, 11) * mm]});
            skFitSpline(sketch, "E280", {"points": [v(5.05, 11) * mm, v(6.73, 16.78) * mm, v(11.14, 21.2) * mm, v(16.92, 22.88) * mm]});
            skFitSpline(sketch, "E281", {"points": [v(16.92, 22.88) * mm, v(18.97, 23.48) * mm, v(23.04, 23.55) * mm, v(25.25, 23.03) * mm]});
            skFitSpline(sketch, "E282", {"points": [v(25.25, 23.03) * mm, v(32.4, 21.33) * mm, v(37.72, 14.97) * mm, v(38.14, 7.62) * mm]});
            skFitSpline(sketch, "E283", {"points": [v(38.14, 7.62) * mm, v(38.8, -3.9) * mm, v(28.21, -12.64) * mm, v(17.12, -9.73) * mm]});
            skFitSpline(sketch, "E284", {"points": [v(25.12, -9.3) * mm, v(34.06, -7.05) * mm, v(39.38, 1.83) * mm, v(37.1, 10.7) * mm]});
            skFitSpline(sketch, "E285", {"points": [v(37.1, 10.7) * mm, v(36.32, 13.77) * mm, v(35.32, 15.47) * mm, v(32.84, 17.99) * mm]});
            skFitSpline(sketch, "E286", {"points": [v(32.84, 17.99) * mm, v(30.39, 20.47) * mm, v(27.86, 21.87) * mm, v(24.53, 22.58) * mm]});
            skFitSpline(sketch, "E287", {"points": [v(24.53, 22.58) * mm, v(22.06, 23.1) * mm, v(20.54, 23.1) * mm, v(18.05, 22.58) * mm]});
            skFitSpline(sketch, "E288", {"points": [v(18.05, 22.58) * mm, v(10.66, 21.03) * mm, v(4.94, 14.07) * mm, v(4.94, 6.63) * mm]});
            skFitSpline(sketch, "E289", {"points": [v(4.94, 6.63) * mm, v(4.94, -0.58) * mm, v(10.47, -7.58) * mm, v(17.51, -9.29) * mm]});
            skFitSpline(sketch, "E290", {"points": [v(17.51, -9.29) * mm, v(19.73, -9.82) * mm, v(23.05, -9.83) * mm, v(25.12, -9.3) * mm]});
            skLineSegment(sketch, "E291", {"start": v(25.12, -9.3) * mm, "end": v(25.12, -9.3) * mm});
            skFitSpline(sketch, "E292", {"points": [v(17.49, -6.8) * mm, v(15.54, -6.18) * mm, v(14.12, -5.31) * mm, v(12.9, -4) * mm]});
            skFitSpline(sketch, "E293", {"points": [v(12.9, -4) * mm, v(11.78, -2.78) * mm, v(10.92, -0.72) * mm, v(11.28, -0.13) * mm]});
            skFitSpline(sketch, "E294", {"points": [v(11.28, -0.13) * mm, v(11.38, 0.03) * mm, v(13.62, 0.14) * mm, v(16.8, 0.14) * mm]});
            skLineSegment(sketch, "E295", {"start": v(16.8, 0.14) * mm, "end": v(22.14, 0.14) * mm});
            skLineSegment(sketch, "E296", {"start": v(22.14, 0.14) * mm, "end": v(22.14, 2.61) * mm});
            skFitSpline(sketch, "E297", {"points": [v(22.14, 2.61) * mm, v(22.15, 5.96) * mm, v(22.5, 7.07) * mm, v(24.08, 8.65) * mm]});
            skFitSpline(sketch, "E298", {"points": [v(24.08, 8.65) * mm, v(25.56, 10.12) * mm, v(27.22, 10.76) * mm, v(30.4, 11.05) * mm]});
            skFitSpline(sketch, "E299", {"points": [v(30.4, 11.05) * mm, v(32.28, 11.23) * mm, v(32.3, 11.22) * mm, v(32.3, 10.54) * mm]});
            skFitSpline(sketch, "E300", {"points": [v(32.3, 10.54) * mm, v(32.3, 9.43) * mm, v(30.2, 5.45) * mm, v(29.02, 4.32) * mm]});
            skFitSpline(sketch, "E301", {"points": [v(29.02, 4.32) * mm, v(27.7, 3.05) * mm, v(26.77, 2.68) * mm, v(24.95, 2.68) * mm]});
            skLineSegment(sketch, "E302", {"start": v(24.95, 2.68) * mm, "end": v(23.55, 2.68) * mm});
            skLineSegment(sketch, "E303", {"start": v(23.55, 2.68) * mm, "end": v(23.55, 1.42) * mm});
            skLineSegment(sketch, "E304", {"start": v(23.55, 1.42) * mm, "end": v(23.55, 0.16) * mm});
            skLineSegment(sketch, "E305", {"start": v(23.55, 0.16) * mm, "end": v(27.43, 0.08) * mm});
            skLineSegment(sketch, "E306", {"start": v(27.43, 0.08) * mm, "end": v(31.32, 0) * mm});
            skLineSegment(sketch, "E307", {"start": v(31.32, 0) * mm, "end": v(31.28, -1.06) * mm});
            skFitSpline(sketch, "E308", {"points": [v(31.28, -1.06) * mm, v(31.22, -3.26) * mm, v(28.73, -5.66) * mm, v(25.46, -6.67) * mm]});
            skFitSpline(sketch, "E309", {"points": [v(25.46, -6.67) * mm, v(23.49, -7.29) * mm, v(19.24, -7.35) * mm, v(17.49, -6.8) * mm]});
            skFitSpline(sketch, "E310", {"points": [v(25.18, -6.1) * mm, v(28.13, -5.2) * mm, v(30.22, -3.35) * mm, v(30.76, -1.2) * mm]});
            skLineSegment(sketch, "E311", {"start": v(30.76, -1.2) * mm, "end": v(30.95, -0.42) * mm});
            skLineSegment(sketch, "E312", {"start": v(30.95, -0.42) * mm, "end": v(26.97, -0.42) * mm});
            skLineSegment(sketch, "E313", {"start": v(26.97, -0.42) * mm, "end": v(22.99, -0.42) * mm});
            skLineSegment(sketch, "E314", {"start": v(22.99, -0.42) * mm, "end": v(22.99, 1.54) * mm});
            skLineSegment(sketch, "E315", {"start": v(22.99, 1.54) * mm, "end": v(22.99, 3.5) * mm});
            skLineSegment(sketch, "E316", {"start": v(22.99, 3.5) * mm, "end": v(24.36, 3.34) * mm});
            skFitSpline(sketch, "E317", {"points": [v(24.36, 3.34) * mm, v(26.16, 3.13) * mm, v(27.45, 3.58) * mm, v(28.7, 4.87) * mm]});
            skFitSpline(sketch, "E318", {"points": [v(28.7, 4.87) * mm, v(29.66, 5.88) * mm, v(31.21, 8.59) * mm, v(31.6, 9.95) * mm]});
            skFitSpline(sketch, "E319", {"points": [v(31.6, 9.95) * mm, v(31.82, 10.73) * mm, v(31.46, 10.76) * mm, v(28.64, 10.16) * mm]});
            skFitSpline(sketch, "E320", {"points": [v(28.64, 10.16) * mm, v(26.18, 9.64) * mm, v(25.3, 9.2) * mm, v(24.18, 7.93) * mm]});
            skFitSpline(sketch, "E321", {"points": [v(24.18, 7.93) * mm, v(23.03, 6.63) * mm, v(22.71, 5.36) * mm, v(22.7, 2.2) * mm]});
            skLineSegment(sketch, "E322", {"start": v(22.7, 2.2) * mm, "end": v(22.7, -0.41) * mm});
            skLineSegment(sketch, "E323", {"start": v(22.7, -0.41) * mm, "end": v(17.23, -0.49) * mm});
            skLineSegment(sketch, "E324", {"start": v(17.23, -0.49) * mm, "end": v(11.75, -0.56) * mm});
            skLineSegment(sketch, "E325", {"start": v(11.75, -0.56) * mm, "end": v(12.13, -1.66) * mm});
            skFitSpline(sketch, "E326", {"points": [v(12.13, -1.66) * mm, v(12.82, -3.68) * mm, v(15.4, -5.68) * mm, v(18.12, -6.32) * mm]});
            skFitSpline(sketch, "E327", {"points": [v(18.12, -6.32) * mm, v(20, -6.77) * mm, v(23.39, -6.67) * mm, v(25.18, -6.1) * mm]});
            skLineSegment(sketch, "E328", {"start": v(25.18, -6.1) * mm, "end": v(25.18, -6.1) * mm});
            skFitSpline(sketch, "E329", {"points": [v(15.14, 3.15) * mm, v(14.63, 3.4) * mm, v(13.8, 4.1) * mm, v(13.28, 4.7) * mm]});
            skFitSpline(sketch, "E330", {"points": [v(13.28, 4.7) * mm, v(12.18, 5.98) * mm, v(10.65, 8.93) * mm, v(10.4, 10.23) * mm]});
            skLineSegment(sketch, "E331", {"start": v(10.4, 10.23) * mm, "end": v(10.22, 11.15) * mm});
            skLineSegment(sketch, "E332", {"start": v(10.22, 11.15) * mm, "end": v(11.45, 11.14) * mm});
            skFitSpline(sketch, "E333", {"points": [v(11.45, 11.14) * mm, v(13.04, 11.14) * mm, v(15.94, 10.45) * mm, v(17.28, 9.77) * mm]});
            skFitSpline(sketch, "E334", {"points": [v(17.28, 9.77) * mm, v(19.3, 8.73) * mm, v(20.45, 6.84) * mm, v(20.45, 4.55) * mm]});
            skFitSpline(sketch, "E335", {"points": [v(20.45, 4.55) * mm, v(20.45, 3.4) * mm, v(20.38, 3.28) * mm, v(19.56, 3) * mm]});
            skFitSpline(sketch, "E336", {"points": [v(19.56, 3) * mm, v(18.28, 2.55) * mm, v(16.22, 2.62) * mm, v(15.14, 3.15) * mm]});
            skFitSpline(sketch, "E337", {"points": [v(19.16, 3.52) * mm, v(20.1, 3.88) * mm, v(20.14, 5.17) * mm, v(19.25, 6.92) * mm]});
            skFitSpline(sketch, "E338", {"points": [v(19.25, 6.92) * mm, v(18.25, 8.9) * mm, v(16.16, 9.99) * mm, v(12.44, 10.45) * mm]});
            skLineSegment(sketch, "E339", {"start": v(12.44, 10.45) * mm, "end": v(10.86, 10.65) * mm});
            skLineSegment(sketch, "E340", {"start": v(10.86, 10.65) * mm, "end": v(11.28, 9.45) * mm});
            skFitSpline(sketch, "E341", {"points": [v(11.28, 9.45) * mm, v(11.85, 7.84) * mm, v(13.21, 5.5) * mm, v(14.01, 4.74) * mm]});
            skFitSpline(sketch, "E342", {"points": [v(14.01, 4.74) * mm, v(15.5, 3.35) * mm, v(17.48, 2.88) * mm, v(19.16, 3.52) * mm]});
            skFitSpline(sketch, "E343", {"points": [v(19.92, 8.66) * mm, v(18.5, 10.05) * mm, v(18.07, 11.07) * mm, v(18.08, 13.06) * mm]});
            skFitSpline(sketch, "E344", {"points": [v(18.08, 13.06) * mm, v(18.1, 14.61) * mm, v(18.26, 15.18) * mm, v(19.45, 17.52) * mm]});
            skFitSpline(sketch, "E345", {"points": [v(19.45, 17.52) * mm, v(21.2, 20.98) * mm, v(21.49, 20.98) * mm, v(23.24, 17.58) * mm]});
            skFitSpline(sketch, "E346", {"points": [v(23.24, 17.58) * mm, v(24.83, 14.5) * mm, v(25.09, 12.45) * mm, v(24.13, 10.47) * mm]});
            skFitSpline(sketch, "E347", {"points": [v(24.13, 10.47) * mm, v(23.45, 9.07) * mm, v(22.1, 7.76) * mm, v(21.33, 7.76) * mm]});
            skFitSpline(sketch, "E348", {"points": [v(21.33, 7.76) * mm, v(21.06, 7.76) * mm, v(20.42, 8.17) * mm, v(19.92, 8.66) * mm]});
            skFitSpline(sketch, "E349", {"points": [v(22.38, 9.04) * mm, v(23.57, 10.04) * mm, v(24.24, 11.93) * mm, v(24.02, 13.62) * mm]});
            skFitSpline(sketch, "E350", {"points": [v(24.02, 13.62) * mm, v(23.81, 15.17) * mm, v(21.68, 19.71) * mm, v(21.27, 19.46) * mm]});
            skFitSpline(sketch, "E351", {"points": [v(21.27, 19.46) * mm, v(20.76, 19.14) * mm, v(19.02, 15.36) * mm, v(18.76, 14) * mm]});
            skFitSpline(sketch, "E352", {"points": [v(18.76, 14) * mm, v(18.42, 12.2) * mm, v(18.81, 10.84) * mm, v(20.08, 9.44) * mm]});
            skFitSpline(sketch, "E353", {"points": [v(20.08, 9.44) * mm, v(20.63, 8.83) * mm, v(21.18, 8.33) * mm, v(21.3, 8.33) * mm]});
            skFitSpline(sketch, "E354", {"points": [v(21.3, 8.33) * mm, v(21.43, 8.33) * mm, v(21.92, 8.65) * mm, v(22.38, 9.04) * mm]});
            skFitSpline(sketch, "E355", {"points": [v(-34.06, 34.82) * mm, v(-34.25, 35.12) * mm, v(-34.6, 35.29) * mm, v(-34.88, 35.22) * mm]});
            skFitSpline(sketch, "E356", {"points": [v(-34.88, 35.22) * mm, v(-35.15, 35.14) * mm, v(-35.61, 35.21) * mm, v(-35.9, 35.37) * mm]});
            skFitSpline(sketch, "E357", {"points": [v(-35.9, 35.37) * mm, v(-36.25, 35.56) * mm, v(-36.6, 35.56) * mm, v(-36.93, 35.37) * mm]});
            skFitSpline(sketch, "E358", {"points": [v(-36.93, 35.37) * mm, v(-37.26, 35.2) * mm, v(-37.7, 35.19) * mm, v(-38.22, 35.37) * mm]});
            skFitSpline(sketch, "E359", {"points": [v(-38.22, 35.37) * mm, v(-38.72, 35.54) * mm, v(-39.17, 35.54) * mm, v(-39.49, 35.37) * mm]});
            skFitSpline(sketch, "E360", {"points": [v(-39.49, 35.37) * mm, v(-39.8, 35.2) * mm, v(-40.26, 35.2) * mm, v(-40.74, 35.36) * mm]});
            skFitSpline(sketch, "E361", {"points": [v(-40.74, 35.36) * mm, v(-41.22, 35.52) * mm, v(-41.72, 35.52) * mm, v(-42.1, 35.35) * mm]});
            skFitSpline(sketch, "E362", {"points": [v(-42.1, 35.35) * mm, v(-42.55, 35.15) * mm, v(-42.96, 35.2) * mm, v(-43.6, 35.5) * mm]});
            skFitSpline(sketch, "E363", {"points": [v(-43.6, 35.5) * mm, v(-44.07, 35.75) * mm, v(-44.46, 35.83) * mm, v(-44.46, 35.7) * mm]});
            skFitSpline(sketch, "E364", {"points": [v(-44.46, 35.7) * mm, v(-44.46, 35.35) * mm, v(-46.26, 35.04) * mm, v(-46.98, 35.27) * mm]});
            skFitSpline(sketch, "E365", {"points": [v(-46.98, 35.27) * mm, v(-47.5, 35.44) * mm, v(-47.57, 35.68) * mm, v(-47.57, 37.54) * mm]});
            skFitSpline(sketch, "E366", {"points": [v(-47.57, 37.54) * mm, v(-47.57, 38.68) * mm, v(-47.43, 39.7) * mm, v(-47.27, 39.8) * mm]});
            skFitSpline(sketch, "E367", {"points": [v(-47.27, 39.8) * mm, v(-46.66, 40.18) * mm, v(-46.15, 39.3) * mm, v(-46.15, 37.9) * mm]});
            skFitSpline(sketch, "E368", {"points": [v(-46.15, 37.9) * mm, v(-46.15, 36.5) * mm, v(-46.15, 36.49) * mm, v(-45.38, 36.68) * mm]});
            skFitSpline(sketch, "E369", {"points": [v(-45.38, 36.68) * mm, v(-44.47, 36.91) * mm, v(-44, 37.5) * mm, v(-44.63, 37.63) * mm]});
            skFitSpline(sketch, "E370", {"points": [v(-44.63, 37.63) * mm, v(-45.22, 37.76) * mm, v(-45.07, 39.8) * mm, v(-44.46, 39.8) * mm]});
            skFitSpline(sketch, "E371", {"points": [v(-44.46, 39.8) * mm, v(-44.23, 39.8) * mm, v(-44, 39.5) * mm, v(-43.94, 39.13) * mm]});
            skLineSegment(sketch, "E372", {"start": v(-43.94, 39.13) * mm, "end": v(-43.85, 38.47) * mm});
            skLineSegment(sketch, "E373", {"start": v(-43.85, 38.47) * mm, "end": v(-43.43, 39.06) * mm});
            skFitSpline(sketch, "E374", {"points": [v(-43.43, 39.06) * mm, v(-43.2, 39.4) * mm, v(-42.7, 39.65) * mm, v(-42.3, 39.65) * mm]});
            skFitSpline(sketch, "E375", {"points": [v(-42.3, 39.65) * mm, v(-41.73, 39.65) * mm, v(-41.63, 39.55) * mm, v(-41.78, 39.08) * mm]});
            skFitSpline(sketch, "E376", {"points": [v(-41.78, 39.08) * mm, v(-41.95, 38.55) * mm, v(-41.88, 38.53) * mm, v(-40.82, 38.7) * mm]});
            skFitSpline(sketch, "E377", {"points": [v(-40.82, 38.7) * mm, v(-40.1, 38.81) * mm, v(-39.52, 38.76) * mm, v(-39.27, 38.55) * mm]});
            skFitSpline(sketch, "E378", {"points": [v(-39.27, 38.55) * mm, v(-39.04, 38.36) * mm, v(-38.8, 38.33) * mm, v(-38.7, 38.47) * mm]});
            skFitSpline(sketch, "E379", {"points": [v(-38.7, 38.47) * mm, v(-38.62, 38.61) * mm, v(-37.34, 38.74) * mm, v(-35.86, 38.76) * mm]});
            skLineSegment(sketch, "E380", {"start": v(-35.86, 38.76) * mm, "end": v(-33.17, 38.78) * mm});
            skLineSegment(sketch, "E381", {"start": v(-33.17, 38.78) * mm, "end": v(-33.17, 37.82) * mm});
            skFitSpline(sketch, "E382", {"points": [v(-33.17, 37.82) * mm, v(-33.17, 36.49) * mm, v(-32.66, 36.3) * mm, v(-32.55, 37.6) * mm]});
            skLineSegment(sketch, "E383", {"start": v(-32.55, 37.6) * mm, "end": v(-32.47, 38.67) * mm});
            skLineSegment(sketch, "E384", {"start": v(-32.47, 38.67) * mm, "end": v(-31.06, 38.74) * mm});
            skFitSpline(sketch, "E385", {"points": [v(-31.06, 38.74) * mm, v(-30.18, 38.8) * mm, v(-29.57, 38.97) * mm, v(-29.43, 39.24) * mm]});
            skFitSpline(sketch, "E386", {"points": [v(-29.43, 39.24) * mm, v(-29.1, 39.8) * mm, v(-28.44, 39.76) * mm, v(-28.29, 39.16) * mm]});
            skFitSpline(sketch, "E387", {"points": [v(-28.29, 39.16) * mm, v(-28.16, 38.69) * mm, v(-28.16, 38.69) * mm, v(-28.13, 39.16) * mm]});
            skFitSpline(sketch, "E388", {"points": [v(-28.13, 39.16) * mm, v(-28.08, 39.77) * mm, v(-27.31, 39.8) * mm, v(-26.68, 39.23) * mm]});
            skFitSpline(sketch, "E389", {"points": [v(-26.68, 39.23) * mm, v(-26.36, 38.94) * mm, v(-25.57, 38.8) * mm, v(-24.26, 38.78) * mm]});
            skFitSpline(sketch, "E390", {"points": [v(-24.26, 38.78) * mm, v(-23.18, 38.76) * mm, v(-22.16, 38.63) * mm, v(-21.98, 38.48) * mm]});
            skFitSpline(sketch, "E391", {"points": [v(-21.98, 38.48) * mm, v(-21.77, 38.31) * mm, v(-21.59, 38.32) * mm, v(-21.47, 38.51) * mm]});
            skFitSpline(sketch, "E392", {"points": [v(-21.47, 38.51) * mm, v(-21.2, 38.96) * mm, v(-19.72, 38.86) * mm, v(-19.22, 38.36) * mm]});
            skFitSpline(sketch, "E393", {"points": [v(-19.22, 38.36) * mm, v(-18.16, 37.3) * mm, v(-19.23, 34.86) * mm, v(-20.57, 35.28) * mm]});
            skFitSpline(sketch, "E394", {"points": [v(-20.57, 35.28) * mm, v(-20.9, 35.38) * mm, v(-21.53, 35.46) * mm, v(-21.95, 35.44) * mm]});
            skFitSpline(sketch, "E395", {"points": [v(-21.95, 35.44) * mm, v(-22.68, 35.41) * mm, v(-22.73, 35.49) * mm, v(-22.73, 36.56) * mm]});
            skFitSpline(sketch, "E396", {"points": [v(-22.73, 36.56) * mm, v(-22.73, 37.26) * mm, v(-22.84, 37.64) * mm, v(-23.01, 37.54) * mm]});
            skFitSpline(sketch, "E397", {"points": [v(-23.01, 37.54) * mm, v(-23.17, 37.44) * mm, v(-23.3, 36.93) * mm, v(-23.3, 36.4) * mm]});
            skFitSpline(sketch, "E398", {"points": [v(-23.3, 36.4) * mm, v(-23.3, 35.6) * mm, v(-23.4, 35.42) * mm, v(-23.86, 35.42) * mm]});
            skFitSpline(sketch, "E399", {"points": [v(-23.86, 35.42) * mm, v(-24.31, 35.42) * mm, v(-24.42, 35.6) * mm, v(-24.42, 36.4) * mm]});
            skFitSpline(sketch, "E400", {"points": [v(-24.42, 36.4) * mm, v(-24.42, 36.93) * mm, v(-24.55, 37.44) * mm, v(-24.7, 37.54) * mm]});
            skFitSpline(sketch, "E401", {"points": [v(-24.7, 37.54) * mm, v(-24.88, 37.64) * mm, v(-24.99, 37.26) * mm, v(-24.99, 36.57) * mm]});
            skFitSpline(sketch, "E402", {"points": [v(-24.99, 36.57) * mm, v(-24.99, 35.27) * mm, v(-24.63, 35.38) * mm, v(-28.96, 35.31) * mm]});
            skFitSpline(sketch, "E403", {"points": [v(-28.96, 35.31) * mm, v(-30.81, 35.29) * mm, v(-31.29, 35.19) * mm, v(-31.51, 34.79) * mm]});
            skFitSpline(sketch, "E404", {"points": [v(-31.51, 34.79) * mm, v(-31.9, 34.1) * mm, v(-33.62, 34.12) * mm, v(-34.06, 34.82) * mm]});
            skLineSegment(sketch, "E405", {"start": v(-34.06, 34.82) * mm, "end": v(-34.06, 34.82) * mm});
            skFitSpline(sketch, "E406", {"points": [v(-25.56, 36.62) * mm, v(-25.56, 37.12) * mm, v(-25.62, 37.16) * mm, v(-25.82, 36.84) * mm]});
            skFitSpline(sketch, "E407", {"points": [v(-25.82, 36.84) * mm, v(-25.96, 36.62) * mm, v(-26.02, 36.33) * mm, v(-25.94, 36.2) * mm]});
            skFitSpline(sketch, "E408", {"points": [v(-25.94, 36.2) * mm, v(-25.7, 35.81) * mm, v(-25.55, 35.97) * mm, v(-25.56, 36.62) * mm]});
            skFitSpline(sketch, "E409", {"points": [v(-31.44, 36.52) * mm, v(-31.67, 36.67) * mm, v(-31.75, 36.99) * mm, v(-31.64, 37.34) * mm]});
            skFitSpline(sketch, "E410", {"points": [v(-31.64, 37.34) * mm, v(-31.54, 37.65) * mm, v(-31.59, 38) * mm, v(-31.75, 38.1) * mm]});
            skFitSpline(sketch, "E411", {"points": [v(-31.75, 38.1) * mm, v(-31.93, 38.2) * mm, v(-32.04, 37.9) * mm, v(-32.04, 37.27) * mm]});
            skFitSpline(sketch, "E412", {"points": [v(-32.04, 37.27) * mm, v(-32.04, 36.5) * mm, v(-31.93, 36.27) * mm, v(-31.55, 36.27) * mm]});
            skFitSpline(sketch, "E413", {"points": [v(-31.55, 36.27) * mm, v(-31.16, 36.27) * mm, v(-31.14, 36.33) * mm, v(-31.44, 36.52) * mm]});
            skFitSpline(sketch, "E414", {"points": [v(-28.94, 36.38) * mm, v(-28.94, 36.44) * mm, v(-29.14, 36.56) * mm, v(-29.38, 36.66) * mm]});
            skFitSpline(sketch, "E415", {"points": [v(-29.38, 36.66) * mm, v(-29.63, 36.75) * mm, v(-29.74, 36.7) * mm, v(-29.64, 36.55) * mm]});
            skFitSpline(sketch, "E416", {"points": [v(-29.64, 36.55) * mm, v(-29.48, 36.28) * mm, v(-28.94, 36.15) * mm, v(-28.94, 36.38) * mm]});
            skFitSpline(sketch, "E417", {"points": [v(-41.3, 37.46) * mm, v(-41.52, 37.67) * mm, v(-41.56, 37.56) * mm, v(-41.43, 37.1) * mm]});
            skFitSpline(sketch, "E418", {"points": [v(-41.43, 37.1) * mm, v(-41.33, 36.7) * mm, v(-41.2, 36.58) * mm, v(-41.13, 36.8) * mm]});
            skFitSpline(sketch, "E419", {"points": [v(-41.13, 36.8) * mm, v(-41.07, 37) * mm, v(-41.15, 37.3) * mm, v(-41.3, 37.46) * mm]});
            skFitSpline(sketch, "E420", {"points": [v(-39.87, 36.72) * mm, v(-39.65, 36.94) * mm, v(-39.94, 37.68) * mm, v(-40.26, 37.68) * mm]});
            skFitSpline(sketch, "E421", {"points": [v(-40.26, 37.68) * mm, v(-40.4, 37.68) * mm, v(-40.51, 37.42) * mm, v(-40.51, 37.11) * mm]});
            skFitSpline(sketch, "E422", {"points": [v(-40.51, 37.11) * mm, v(-40.51, 36.56) * mm, v(-40.21, 36.38) * mm, v(-39.87, 36.72) * mm]});
            skFitSpline(sketch, "E423", {"points": [v(-37.26, 37.11) * mm, v(-37.26, 37.32) * mm, v(-37.42, 37.54) * mm, v(-37.62, 37.6) * mm]});
            skFitSpline(sketch, "E424", {"points": [v(-37.62, 37.6) * mm, v(-37.83, 37.68) * mm, v(-37.97, 37.48) * mm, v(-37.97, 37.11) * mm]});
            skFitSpline(sketch, "E425", {"points": [v(-37.97, 37.11) * mm, v(-37.97, 36.75) * mm, v(-37.83, 36.55) * mm, v(-37.62, 36.62) * mm]});
            skFitSpline(sketch, "E426", {"points": [v(-37.62, 36.62) * mm, v(-37.42, 36.68) * mm, v(-37.26, 36.9) * mm, v(-37.26, 37.11) * mm]});
            skFitSpline(sketch, "E427", {"points": [v(-28.25, 36.81) * mm, v(-28.16, 36.96) * mm, v(-28.21, 37.15) * mm, v(-28.37, 37.25) * mm]});
            skFitSpline(sketch, "E428", {"points": [v(-28.37, 37.25) * mm, v(-28.53, 37.35) * mm, v(-28.66, 37.23) * mm, v(-28.66, 36.99) * mm]});
            skFitSpline(sketch, "E429", {"points": [v(-28.66, 36.99) * mm, v(-28.66, 36.5) * mm, v(-28.49, 36.42) * mm, v(-28.25, 36.81) * mm]});
            skFitSpline(sketch, "E430", {"points": [v(-21.7, 37.17) * mm, v(-21.78, 37.4) * mm, v(-21.85, 37.32) * mm, v(-21.86, 37) * mm]});
            skFitSpline(sketch, "E431", {"points": [v(-21.86, 37) * mm, v(-21.87, 36.7) * mm, v(-21.8, 36.53) * mm, v(-21.71, 36.63) * mm]});
            skFitSpline(sketch, "E432", {"points": [v(-21.71, 36.63) * mm, v(-21.62, 36.72) * mm, v(-21.6, 36.96) * mm, v(-21.7, 37.17) * mm]});
            skLineSegment(sketch, "E433", {"start": v(-21.7, 37.17) * mm, "end": v(-21.7, 37.17) * mm});
            skFitSpline(sketch, "E434", {"points": [v(-1.85, 34.68) * mm, v(-1.85, 35.12) * mm, v(-3.05, 35.54) * mm, v(-4.01, 35.45) * mm]});
            skFitSpline(sketch, "E435", {"points": [v(-4.01, 35.45) * mm, v(-4.54, 35.4) * mm, v(-4.65, 35.55) * mm, v(-4.74, 36.46) * mm]});
            skLineSegment(sketch, "E436", {"start": v(-4.74, 36.46) * mm, "end": v(-4.86, 37.54) * mm});
            skLineSegment(sketch, "E437", {"start": v(-4.86, 37.54) * mm, "end": v(-4.9, 36.51) * mm});
            skFitSpline(sketch, "E438", {"points": [v(-4.9, 36.51) * mm, v(-4.95, 35.56) * mm, v(-5.02, 35.48) * mm, v(-6, 35.34) * mm]});
            skFitSpline(sketch, "E439", {"points": [v(-6, 35.34) * mm, v(-6.6, 35.25) * mm, v(-7.57, 35.27) * mm, v(-8.2, 35.37) * mm]});
            skFitSpline(sketch, "E440", {"points": [v(-8.2, 35.37) * mm, v(-9.26, 35.56) * mm, v(-9.33, 35.63) * mm, v(-9.47, 36.7) * mm]});
            skFitSpline(sketch, "E441", {"points": [v(-9.47, 36.7) * mm, v(-9.57, 37.54) * mm, v(-9.66, 37.7) * mm, v(-9.82, 37.3) * mm]});
            skFitSpline(sketch, "E442", {"points": [v(-9.82, 37.3) * mm, v(-9.94, 37.02) * mm, v(-10.03, 36.48) * mm, v(-10.03, 36.1) * mm]});
            skFitSpline(sketch, "E443", {"points": [v(-10.03, 36.1) * mm, v(-10.03, 35.6) * mm, v(-10.19, 35.42) * mm, v(-10.6, 35.42) * mm]});
            skFitSpline(sketch, "E444", {"points": [v(-10.6, 35.42) * mm, v(-11.07, 35.42) * mm, v(-11.16, 35.6) * mm, v(-11.16, 36.57) * mm]});
            skFitSpline(sketch, "E445", {"points": [v(-11.16, 36.57) * mm, v(-11.16, 37.26) * mm, v(-11.27, 37.64) * mm, v(-11.44, 37.54) * mm]});
            skFitSpline(sketch, "E446", {"points": [v(-11.44, 37.54) * mm, v(-11.6, 37.44) * mm, v(-11.72, 36.94) * mm, v(-11.72, 36.43) * mm]});
            skFitSpline(sketch, "E447", {"points": [v(-11.72, 36.43) * mm, v(-11.72, 35.54) * mm, v(-11.78, 35.49) * mm, v(-12.92, 35.36) * mm]});
            skFitSpline(sketch, "E448", {"points": [v(-12.92, 35.36) * mm, v(-13.58, 35.29) * mm, v(-14.6, 35.29) * mm, v(-15.18, 35.36) * mm]});
            skFitSpline(sketch, "E449", {"points": [v(-15.18, 35.36) * mm, v(-16.2, 35.48) * mm, v(-16.24, 35.52) * mm, v(-16.24, 36.6) * mm]});
            skFitSpline(sketch, "E450", {"points": [v(-16.24, 36.6) * mm, v(-16.24, 37.27) * mm, v(-16.35, 37.64) * mm, v(-16.52, 37.54) * mm]});
            skFitSpline(sketch, "E451", {"points": [v(-16.52, 37.54) * mm, v(-16.68, 37.44) * mm, v(-16.8, 36.93) * mm, v(-16.8, 36.4) * mm]});
            skFitSpline(sketch, "E452", {"points": [v(-16.8, 36.4) * mm, v(-16.8, 35.6) * mm, v(-16.91, 35.42) * mm, v(-17.37, 35.42) * mm]});
            skFitSpline(sketch, "E453", {"points": [v(-17.37, 35.42) * mm, v(-17.87, 35.42) * mm, v(-17.93, 35.6) * mm, v(-17.93, 37.11) * mm]});
            skLineSegment(sketch, "E454", {"start": v(-17.93, 37.11) * mm, "end": v(-17.93, 38.8) * mm});
            skLineSegment(sketch, "E455", {"start": v(-17.93, 38.8) * mm, "end": v(-16.1, 38.77) * mm});
            skLineSegment(sketch, "E456", {"start": v(-16.1, 38.77) * mm, "end": v(-14.26, 38.75) * mm});
            skLineSegment(sketch, "E457", {"start": v(-14.26, 38.75) * mm, "end": v(-14.26, 37.65) * mm});
            skFitSpline(sketch, "E458", {"points": [v(-14.26, 37.65) * mm, v(-14.26, 36.24) * mm, v(-13.76, 36.2) * mm, v(-13.65, 37.6) * mm]});
            skLineSegment(sketch, "E459", {"start": v(-13.65, 37.6) * mm, "end": v(-13.56, 38.67) * mm});
            skLineSegment(sketch, "E460", {"start": v(-13.56, 38.67) * mm, "end": v(-10.82, 38.68) * mm});
            skFitSpline(sketch, "E461", {"points": [v(-10.82, 38.68) * mm, v(-8.65, 38.7) * mm, v(-7.97, 38.8) * mm, v(-7.55, 39.17) * mm]});
            skFitSpline(sketch, "E462", {"points": [v(-7.55, 39.17) * mm, v(-6.9, 39.77) * mm, v(-6.08, 39.8) * mm, v(-6.08, 39.23) * mm]});
            skFitSpline(sketch, "E463", {"points": [v(-6.08, 39.23) * mm, v(-6.08, 38.55) * mm, v(-4.76, 38.7) * mm, v(-4.58, 39.4) * mm]});
            skFitSpline(sketch, "E464", {"points": [v(-4.58, 39.4) * mm, v(-4.38, 40.15) * mm, v(-3.4, 40) * mm, v(-3.41, 39.22) * mm]});
            skFitSpline(sketch, "E465", {"points": [v(-3.41, 39.22) * mm, v(-3.43, 38.73) * mm, v(-3.24, 38.66) * mm, v(-1.72, 38.67) * mm]});
            skLineSegment(sketch, "E466", {"start": v(-1.72, 38.67) * mm, "end": v(-0.01, 38.67) * mm});
            skLineSegment(sketch, "E467", {"start": v(-0.01, 38.67) * mm, "end": v(0.08, 37.6) * mm});
            skFitSpline(sketch, "E468", {"points": [v(0.08, 37.6) * mm, v(0.2, 36.2) * mm, v(0.7, 36.24) * mm, v(0.7, 37.65) * mm]});
            skLineSegment(sketch, "E469", {"start": v(0.7, 37.65) * mm, "end": v(0.7, 38.75) * mm});
            skLineSegment(sketch, "E470", {"start": v(0.7, 38.75) * mm, "end": v(2.17, 38.76) * mm});
            skFitSpline(sketch, "E471", {"points": [v(2.17, 38.76) * mm, v(2.98, 38.77) * mm, v(3.8, 38.64) * mm, v(4, 38.47) * mm]});
            skFitSpline(sketch, "E472", {"points": [v(4, 38.47) * mm, v(4.2, 38.3) * mm, v(4.36, 37.62) * mm, v(4.36, 36.95) * mm]});
            skFitSpline(sketch, "E473", {"points": [v(4.36, 36.95) * mm, v(4.36, 35.4) * mm, v(4, 35.2) * mm, v(1.33, 35.28) * mm]});
            skFitSpline(sketch, "E474", {"points": [v(1.33, 35.28) * mm, v(-0.5, 35.34) * mm, v(-0.72, 35.3) * mm, v(-0.72, 34.82) * mm]});
            skFitSpline(sketch, "E475", {"points": [v(-0.72, 34.82) * mm, v(-0.72, 34.48) * mm, v(-0.92, 34.3) * mm, v(-1.28, 34.3) * mm]});
            skFitSpline(sketch, "E476", {"points": [v(-1.28, 34.3) * mm, v(-1.6, 34.3) * mm, v(-1.85, 34.47) * mm, v(-1.85, 34.68) * mm]});
            skLineSegment(sketch, "E477", {"start": v(-1.85, 34.68) * mm, "end": v(-1.85, 34.68) * mm});
            skFitSpline(sketch, "E478", {"points": [v(-12.65, 37.46) * mm, v(-12.72, 37.81) * mm, v(-12.78, 37.6) * mm, v(-12.78, 36.97) * mm]});
            skFitSpline(sketch, "E479", {"points": [v(-12.78, 36.97) * mm, v(-12.78, 36.35) * mm, v(-12.73, 36.06) * mm, v(-12.66, 36.33) * mm]});
            skFitSpline(sketch, "E480", {"points": [v(-12.66, 36.33) * mm, v(-12.59, 36.6) * mm, v(-12.59, 37.11) * mm, v(-12.65, 37.46) * mm]});
            skFitSpline(sketch, "E481", {"points": [v(-3.77, 37.5) * mm, v(-4.03, 38.02) * mm, v(-4.07, 37.96) * mm, v(-4.08, 36.97) * mm]});
            skFitSpline(sketch, "E482", {"points": [v(-4.08, 36.97) * mm, v(-4.08, 36.03) * mm, v(-4.04, 35.93) * mm, v(-3.78, 36.37) * mm]});
            skFitSpline(sketch, "E483", {"points": [v(-3.78, 36.37) * mm, v(-3.57, 36.73) * mm, v(-3.57, 37.07) * mm, v(-3.77, 37.5) * mm]});
            skFitSpline(sketch, "E484", {"points": [v(-15.2, 37.6) * mm, v(-15.27, 37.88) * mm, v(-15.33, 37.66) * mm, v(-15.33, 37.11) * mm]});
            skFitSpline(sketch, "E485", {"points": [v(-15.33, 37.11) * mm, v(-15.33, 36.57) * mm, v(-15.27, 36.35) * mm, v(-15.2, 36.62) * mm]});
            skFitSpline(sketch, "E486", {"points": [v(-15.2, 36.62) * mm, v(-15.13, 36.9) * mm, v(-15.13, 37.34) * mm, v(-15.2, 37.6) * mm]});
            skFitSpline(sketch, "E487", {"points": [v(-0.69, 38.04) * mm, v(-0.92, 38.27) * mm, v(-1, 38.06) * mm, v(-0.98, 37.24) * mm]});
            skFitSpline(sketch, "E488", {"points": [v(-0.98, 37.24) * mm, v(-0.95, 36.14) * mm, v(-0.95, 36.13) * mm, v(-0.66, 36.93) * mm]});
            skFitSpline(sketch, "E489", {"points": [v(-0.66, 36.93) * mm, v(-0.46, 37.5) * mm, v(-0.46, 37.82) * mm, v(-0.69, 38.04) * mm]});
            skLineSegment(sketch, "E490", {"start": v(-0.69, 38.04) * mm, "end": v(-0.69, 38.04) * mm});
            skFitSpline(sketch, "E491", {"points": [v(-1.9, 37.04) * mm, v(-2.01, 37.64) * mm, v(-2.51, 37.6) * mm, v(-2.64, 36.99) * mm]});
            skFitSpline(sketch, "E492", {"points": [v(-2.64, 36.99) * mm, v(-2.7, 36.73) * mm, v(-2.54, 36.55) * mm, v(-2.27, 36.55) * mm]});
            skFitSpline(sketch, "E493", {"points": [v(-2.27, 36.55) * mm, v(-1.98, 36.55) * mm, v(-1.84, 36.73) * mm, v(-1.9, 37.04) * mm]});
            skFitSpline(sketch, "E494", {"points": [v(1.95, 36.81) * mm, v(2.04, 36.96) * mm, v(1.99, 37.15) * mm, v(1.83, 37.25) * mm]});
            skFitSpline(sketch, "E495", {"points": [v(1.83, 37.25) * mm, v(1.67, 37.35) * mm, v(1.54, 37.23) * mm, v(1.54, 36.99) * mm]});
            skFitSpline(sketch, "E496", {"points": [v(1.54, 36.99) * mm, v(1.54, 36.5) * mm, v(1.71, 36.42) * mm, v(1.95, 36.81) * mm]});
            skFitSpline(sketch, "E497", {"points": [v(-8.58, 37.47) * mm, v(-8.86, 37.75) * mm, v(-8.9, 37.72) * mm, v(-8.74, 37.31) * mm]});
            skFitSpline(sketch, "E498", {"points": [v(-8.74, 37.31) * mm, v(-8.64, 37.03) * mm, v(-8.48, 36.88) * mm, v(-8.4, 36.96) * mm]});
            skFitSpline(sketch, "E499", {"points": [v(-8.4, 36.96) * mm, v(-8.3, 37.05) * mm, v(-8.4, 37.28) * mm, v(-8.58, 37.47) * mm]});
            skFitSpline(sketch, "E500", {"points": [v(28.4, 34.79) * mm, v(27.95, 35.69) * mm, v(28.01, 37.86) * mm, v(28.5, 38.35) * mm]});
            skFitSpline(sketch, "E501", {"points": [v(28.5, 38.35) * mm, v(29.18, 39.03) * mm, v(37.58, 39.03) * mm, v(38.08, 38.35) * mm]});
            skFitSpline(sketch, "E502", {"points": [v(38.08, 38.35) * mm, v(38.37, 37.95) * mm, v(38.48, 38.02) * mm, v(38.9, 38.93) * mm]});
            skFitSpline(sketch, "E503", {"points": [v(38.9, 38.93) * mm, v(39.36, 39.88) * mm, v(39.49, 39.96) * mm, v(40.44, 39.88) * mm]});
            skFitSpline(sketch, "E504", {"points": [v(40.44, 39.88) * mm, v(41.23, 39.82) * mm, v(41.5, 39.66) * mm, v(41.56, 39.22) * mm]});
            skFitSpline(sketch, "E505", {"points": [v(41.56, 39.22) * mm, v(41.63, 38.74) * mm, v(41.8, 38.67) * mm, v(42.73, 38.76) * mm]});
            skFitSpline(sketch, "E506", {"points": [v(42.73, 38.76) * mm, v(43.53, 38.83) * mm, v(43.86, 39.01) * mm, v(43.97, 39.42) * mm]});
            skFitSpline(sketch, "E507", {"points": [v(43.97, 39.42) * mm, v(44.16, 40.16) * mm, v(45.15, 39.99) * mm, v(45.13, 39.21) * mm]});
            skFitSpline(sketch, "E508", {"points": [v(45.13, 39.21) * mm, v(45.12, 38.74) * mm, v(45.26, 38.67) * mm, v(46.02, 38.76) * mm]});
            skFitSpline(sketch, "E509", {"points": [v(46.02, 38.76) * mm, v(47.05, 38.88) * mm, v(47.41, 38.42) * mm, v(47.5, 36.92) * mm]});
            skFitSpline(sketch, "E510", {"points": [v(47.5, 36.92) * mm, v(47.58, 35.48) * mm, v(47.08, 35.22) * mm, v(44.4, 35.33) * mm]});
            skFitSpline(sketch, "E511", {"points": [v(44.4, 35.33) * mm, v(43.1, 35.38) * mm, v(41.06, 35.43) * mm, v(39.87, 35.44) * mm]});
            skFitSpline(sketch, "E512", {"points": [v(39.87, 35.44) * mm, v(38.08, 35.45) * mm, v(37.68, 35.54) * mm, v(37.57, 35.93) * mm]});
            skFitSpline(sketch, "E513", {"points": [v(37.57, 35.93) * mm, v(37.46, 36.37) * mm, v(37.45, 36.36) * mm, v(37.42, 35.91) * mm]});
            skFitSpline(sketch, "E514", {"points": [v(37.42, 35.91) * mm, v(37.4, 35.62) * mm, v(37.16, 35.42) * mm, v(36.82, 35.42) * mm]});
            skFitSpline(sketch, "E515", {"points": [v(36.82, 35.42) * mm, v(36.35, 35.42) * mm, v(36.25, 35.6) * mm, v(36.25, 36.57) * mm]});
            skFitSpline(sketch, "E516", {"points": [v(36.25, 36.57) * mm, v(36.25, 37.26) * mm, v(36.14, 37.64) * mm, v(35.97, 37.54) * mm]});
            skFitSpline(sketch, "E517", {"points": [v(35.97, 37.54) * mm, v(35.82, 37.44) * mm, v(35.69, 36.93) * mm, v(35.69, 36.4) * mm]});
            skFitSpline(sketch, "E518", {"points": [v(35.69, 36.4) * mm, v(35.69, 35.47) * mm, v(35.64, 35.42) * mm, v(34.63, 35.37) * mm]});
            skFitSpline(sketch, "E519", {"points": [v(34.63, 35.37) * mm, v(34.05, 35.34) * mm, v(33.32, 35.35) * mm, v(33, 35.38) * mm]});
            skFitSpline(sketch, "E520", {"points": [v(33, 35.38) * mm, v(31.72, 35.5) * mm, v(31.37, 35.42) * mm, v(30.98, 34.87) * mm]});
            skFitSpline(sketch, "E521", {"points": [v(30.98, 34.87) * mm, v(30.46, 34.12) * mm, v(28.77, 34.07) * mm, v(28.4, 34.79) * mm]});
            skLineSegment(sketch, "E522", {"start": v(28.4, 34.79) * mm, "end": v(28.4, 34.79) * mm});
            skFitSpline(sketch, "E523", {"points": [v(31.1, 37.75) * mm, v(31.02, 38.1) * mm, v(30.97, 37.81) * mm, v(30.97, 37.11) * mm]});
            skFitSpline(sketch, "E524", {"points": [v(30.97, 37.11) * mm, v(30.97, 36.41) * mm, v(31.02, 36.13) * mm, v(31.1, 36.48) * mm]});
            skFitSpline(sketch, "E525", {"points": [v(31.1, 36.48) * mm, v(31.16, 36.83) * mm, v(31.16, 37.4) * mm, v(31.1, 37.75) * mm]});
            skFitSpline(sketch, "E526", {"points": [v(34.76, 37.46) * mm, v(34.7, 37.81) * mm, v(34.64, 37.6) * mm, v(34.63, 36.97) * mm]});
            skFitSpline(sketch, "E527", {"points": [v(34.63, 36.97) * mm, v(34.63, 36.35) * mm, v(34.68, 36.06) * mm, v(34.75, 36.33) * mm]});
            skFitSpline(sketch, "E528", {"points": [v(34.75, 36.33) * mm, v(34.83, 36.6) * mm, v(34.83, 37.11) * mm, v(34.76, 37.46) * mm]});
            skFitSpline(sketch, "E529", {"points": [v(40.12, 37.75) * mm, v(40.05, 38.1) * mm, v(40, 37.81) * mm, v(40, 37.11) * mm]});
            skFitSpline(sketch, "E530", {"points": [v(40, 37.11) * mm, v(40, 36.41) * mm, v(40.05, 36.13) * mm, v(40.12, 36.48) * mm]});
            skFitSpline(sketch, "E531", {"points": [v(40.12, 36.48) * mm, v(40.19, 36.83) * mm, v(40.19, 37.4) * mm, v(40.12, 37.75) * mm]});
            skFitSpline(sketch, "E532", {"points": [v(45, 36.27) * mm, v(45.3, 36.46) * mm, v(45.32, 36.54) * mm, v(45.06, 36.54) * mm]});
            skFitSpline(sketch, "E533", {"points": [v(45.06, 36.54) * mm, v(44.85, 36.55) * mm, v(44.73, 36.81) * mm, v(44.78, 37.18) * mm]});
            skFitSpline(sketch, "E534", {"points": [v(44.78, 37.18) * mm, v(44.83, 37.53) * mm, v(44.73, 37.88) * mm, v(44.58, 37.96) * mm]});
            skFitSpline(sketch, "E535", {"points": [v(44.58, 37.96) * mm, v(44.42, 38.04) * mm, v(44.26, 37.63) * mm, v(44.2, 37.04) * mm]});
            skFitSpline(sketch, "E536", {"points": [v(44.2, 37.04) * mm, v(44.12, 35.95) * mm, v(44.28, 35.8) * mm, v(45, 36.27) * mm]});
            skFitSpline(sketch, "E537", {"points": [v(30.05, 37.14) * mm, v(30.05, 37.82) * mm, v(29.39, 37.73) * mm, v(29.25, 37.02) * mm]});
            skFitSpline(sketch, "E538", {"points": [v(29.25, 37.02) * mm, v(29.2, 36.74) * mm, v(29.34, 36.55) * mm, v(29.6, 36.55) * mm]});
            skFitSpline(sketch, "E539", {"points": [v(29.6, 36.55) * mm, v(29.86, 36.55) * mm, v(30.05, 36.8) * mm, v(30.05, 37.14) * mm]});
            skFitSpline(sketch, "E540", {"points": [v(33.71, 37.11) * mm, v(33.71, 37.42) * mm, v(33.6, 37.68) * mm, v(33.45, 37.68) * mm]});
            skFitSpline(sketch, "E541", {"points": [v(33.45, 37.68) * mm, v(33.07, 37.68) * mm, v(32.8, 37.16) * mm, v(33, 36.83) * mm]});
            skFitSpline(sketch, "E542", {"points": [v(33, 36.83) * mm, v(33.3, 36.35) * mm, v(33.71, 36.52) * mm, v(33.71, 37.11) * mm]});
            skFitSpline(sketch, "E543", {"points": [v(41.52, 37.47) * mm, v(41.44, 37.66) * mm, v(41.38, 37.5) * mm, v(41.38, 37.11) * mm]});
            skFitSpline(sketch, "E544", {"points": [v(41.38, 37.11) * mm, v(41.38, 36.73) * mm, v(41.44, 36.57) * mm, v(41.52, 36.76) * mm]});
            skFitSpline(sketch, "E545", {"points": [v(41.52, 36.76) * mm, v(41.6, 36.95) * mm, v(41.6, 37.27) * mm, v(41.52, 37.47) * mm]});
            skFitSpline(sketch, "E546", {"points": [v(43.26, 37.04) * mm, v(43.14, 37.64) * mm, v(42.64, 37.6) * mm, v(42.51, 36.99) * mm]});
            skFitSpline(sketch, "E547", {"points": [v(42.51, 36.99) * mm, v(42.46, 36.73) * mm, v(42.62, 36.55) * mm, v(42.89, 36.55) * mm]});
            skFitSpline(sketch, "E548", {"points": [v(42.89, 36.55) * mm, v(43.18, 36.55) * mm, v(43.32, 36.73) * mm, v(43.26, 37.04) * mm]});
            skFitSpline(sketch, "E549", {"points": [v(37.52, 37.68) * mm, v(37.62, 37.83) * mm, v(37.56, 37.96) * mm, v(37.4, 37.96) * mm]});
            skFitSpline(sketch, "E550", {"points": [v(37.4, 37.96) * mm, v(37.24, 37.96) * mm, v(37.1, 37.83) * mm, v(37.1, 37.68) * mm]});
            skFitSpline(sketch, "E551", {"points": [v(37.1, 37.68) * mm, v(37.1, 37.52) * mm, v(37.16, 37.4) * mm, v(37.23, 37.4) * mm]});
            skFitSpline(sketch, "E552", {"points": [v(37.23, 37.4) * mm, v(37.3, 37.4) * mm, v(37.43, 37.52) * mm, v(37.52, 37.68) * mm]});
            skFitSpline(sketch, "E553", {"points": [v(5.74, 35.74) * mm, v(5.45, 36.03) * mm, v(5.2, 36.56) * mm, v(5.2, 36.9) * mm]});
            skFitSpline(sketch, "E554", {"points": [v(5.2, 36.9) * mm, v(5.2, 37.78) * mm, v(5.97, 38.8) * mm, v(6.6, 38.8) * mm]});
            skFitSpline(sketch, "E555", {"points": [v(6.6, 38.8) * mm, v(6.9, 38.8) * mm, v(7.2, 39) * mm, v(7.29, 39.23) * mm]});
            skFitSpline(sketch, "E556", {"points": [v(7.29, 39.23) * mm, v(7.38, 39.46) * mm, v(7.7, 39.65) * mm, v(8.02, 39.65) * mm]});
            skFitSpline(sketch, "E557", {"points": [v(8.02, 39.65) * mm, v(8.34, 39.65) * mm, v(8.6, 39.47) * mm, v(8.6, 39.23) * mm]});
            skFitSpline(sketch, "E558", {"points": [v(8.6, 39.23) * mm, v(8.6, 39) * mm, v(8.72, 38.8) * mm, v(8.88, 38.8) * mm]});
            skFitSpline(sketch, "E559", {"points": [v(8.88, 38.8) * mm, v(9.03, 38.8) * mm, v(9.16, 38.37) * mm, v(9.16, 37.84) * mm]});
            skFitSpline(sketch, "E560", {"points": [v(9.16, 37.84) * mm, v(9.16, 36.49) * mm, v(9.67, 36.3) * mm, v(9.78, 37.6) * mm]});
            skFitSpline(sketch, "E561", {"points": [v(9.78, 37.6) * mm, v(9.85, 38.45) * mm, v(9.98, 38.67) * mm, v(10.43, 38.67) * mm]});
            skFitSpline(sketch, "E562", {"points": [v(10.43, 38.67) * mm, v(10.92, 38.67) * mm, v(11, 38.45) * mm, v(11.08, 37.04) * mm]});
            skFitSpline(sketch, "E563", {"points": [v(11.08, 37.04) * mm, v(11.16, 35.52) * mm, v(11.12, 35.42) * mm, v(10.52, 35.4) * mm]});
            skFitSpline(sketch, "E564", {"points": [v(10.52, 35.4) * mm, v(6.3, 35.2) * mm, v(6.27, 35.2) * mm, v(5.74, 35.74) * mm]});
            skFitSpline(sketch, "E565", {"points": [v(8.3, 37.48) * mm, v(8.31, 37.76) * mm, v(8.19, 37.91) * mm, v(8.03, 37.82) * mm]});
            skFitSpline(sketch, "E566", {"points": [v(8.03, 37.82) * mm, v(7.88, 37.72) * mm, v(7.75, 37.3) * mm, v(7.75, 36.89) * mm]});
            skFitSpline(sketch, "E567", {"points": [v(7.75, 36.89) * mm, v(7.76, 36.3) * mm, v(7.82, 36.22) * mm, v(8.03, 36.55) * mm]});
            skFitSpline(sketch, "E568", {"points": [v(8.03, 36.55) * mm, v(8.18, 36.78) * mm, v(8.3, 37.2) * mm, v(8.3, 37.48) * mm]});
            skFitSpline(sketch, "E569", {"points": [v(5.97, 37.17) * mm, v(5.88, 37.4) * mm, v(5.81, 37.32) * mm, v(5.8, 37) * mm]});
            skFitSpline(sketch, "E570", {"points": [v(5.8, 37) * mm, v(5.78, 36.7) * mm, v(5.85, 36.53) * mm, v(5.94, 36.63) * mm]});
            skFitSpline(sketch, "E571", {"points": [v(5.94, 36.63) * mm, v(6.04, 36.72) * mm, v(6.05, 36.96) * mm, v(5.97, 37.17) * mm]});
            skLineSegment(sketch, "E572", {"start": v(5.97, 37.17) * mm, "end": v(5.97, 37.17) * mm});
            skFitSpline(sketch, "E573", {"points": [v(7.19, 37.11) * mm, v(7.19, 37.42) * mm, v(7.06, 37.68) * mm, v(6.9, 37.68) * mm]});
            skFitSpline(sketch, "E574", {"points": [v(6.9, 37.68) * mm, v(6.75, 37.68) * mm, v(6.62, 37.42) * mm, v(6.62, 37.11) * mm]});
            skFitSpline(sketch, "E575", {"points": [v(6.62, 37.11) * mm, v(6.62, 36.8) * mm, v(6.75, 36.55) * mm, v(6.9, 36.55) * mm]});
            skFitSpline(sketch, "E576", {"points": [v(6.9, 36.55) * mm, v(7.06, 36.55) * mm, v(7.19, 36.8) * mm, v(7.19, 37.11) * mm]});
            skFitSpline(sketch, "E577", {"points": [v(10.49, 37.6) * mm, v(10.41, 37.88) * mm, v(10.35, 37.72) * mm, v(10.34, 37.25) * mm]});
            skFitSpline(sketch, "E578", {"points": [v(10.34, 37.25) * mm, v(10.34, 36.79) * mm, v(10.4, 36.56) * mm, v(10.47, 36.76) * mm]});
            skFitSpline(sketch, "E579", {"points": [v(10.47, 36.76) * mm, v(10.55, 36.95) * mm, v(10.56, 37.33) * mm, v(10.49, 37.6) * mm]});
            skLineSegment(sketch, "E580", {"start": v(10.49, 37.6) * mm, "end": v(10.49, 37.6) * mm});
            skFitSpline(sketch, "E581", {"points": [v(7.97, 38.85) * mm, v(7.9, 39.06) * mm, v(7.77, 38.93) * mm, v(7.67, 38.55) * mm]});
            skFitSpline(sketch, "E582", {"points": [v(7.67, 38.55) * mm, v(7.55, 38.08) * mm, v(7.59, 37.97) * mm, v(7.8, 38.18) * mm]});
            skFitSpline(sketch, "E583", {"points": [v(7.8, 38.18) * mm, v(7.96, 38.34) * mm, v(8.04, 38.64) * mm, v(7.97, 38.85) * mm]});
            skFitSpline(sketch, "E584", {"points": [v(13.08, 35.34) * mm, v(12.07, 35.45) * mm, v(12.06, 35.46) * mm, v(11.9, 37.03) * mm]});
            skFitSpline(sketch, "E585", {"points": [v(11.9, 37.03) * mm, v(11.8, 37.9) * mm, v(11.86, 38.85) * mm, v(12, 39.14) * mm]});
            skFitSpline(sketch, "E586", {"points": [v(12, 39.14) * mm, v(12.34, 39.75) * mm, v(13.11, 39.83) * mm, v(13.11, 39.25) * mm]});
            skFitSpline(sketch, "E587", {"points": [v(13.11, 39.25) * mm, v(13.11, 38.78) * mm, v(14.4, 38.61) * mm, v(16.71, 38.76) * mm]});
            skFitSpline(sketch, "E588", {"points": [v(16.71, 38.76) * mm, v(17.72, 38.83) * mm, v(18.2, 38.98) * mm, v(18.2, 39.24) * mm]});
            skFitSpline(sketch, "E589", {"points": [v(18.2, 39.24) * mm, v(18.2, 39.8) * mm, v(18.63, 39.98) * mm, v(19.45, 39.77) * mm]});
            skFitSpline(sketch, "E590", {"points": [v(19.45, 39.77) * mm, v(19.85, 39.67) * mm, v(20.17, 39.4) * mm, v(20.17, 39.13) * mm]});
            skFitSpline(sketch, "E591", {"points": [v(20.17, 39.13) * mm, v(20.17, 38.78) * mm, v(20.44, 38.67) * mm, v(21.3, 38.67) * mm]});
            skFitSpline(sketch, "E592", {"points": [v(21.3, 38.67) * mm, v(22.28, 38.67) * mm, v(22.43, 38.75) * mm, v(22.43, 39.3) * mm]});
            skFitSpline(sketch, "E593", {"points": [v(22.43, 39.3) * mm, v(22.43, 40.1) * mm, v(23.27, 40.16) * mm, v(23.47, 39.37) * mm]});
            skFitSpline(sketch, "E594", {"points": [v(23.47, 39.37) * mm, v(23.6, 38.9) * mm, v(23.86, 38.8) * mm, v(25.08, 38.8) * mm]});
            skFitSpline(sketch, "E595", {"points": [v(25.08, 38.8) * mm, v(26.83, 38.8) * mm, v(27.22, 38.48) * mm, v(27.22, 37.06) * mm]});
            skFitSpline(sketch, "E596", {"points": [v(27.22, 37.06) * mm, v(27.22, 35.76) * mm, v(26.2, 34.89) * mm, v(25.17, 35.32) * mm]});
            skFitSpline(sketch, "E597", {"points": [v(25.17, 35.32) * mm, v(24.82, 35.46) * mm, v(23.78, 35.5) * mm, v(22.85, 35.41) * mm]});
            skFitSpline(sketch, "E598", {"points": [v(22.85, 35.41) * mm, v(21.92, 35.33) * mm, v(20.5, 35.3) * mm, v(19.69, 35.37) * mm]});
            skFitSpline(sketch, "E599", {"points": [v(19.69, 35.37) * mm, v(18.24, 35.49) * mm, v(18.22, 35.5) * mm, v(18.11, 36.51) * mm]});
            skLineSegment(sketch, "E600", {"start": v(18.11, 36.51) * mm, "end": v(18, 37.54) * mm});
            skLineSegment(sketch, "E601", {"start": v(18, 37.54) * mm, "end": v(17.96, 36.48) * mm});
            skFitSpline(sketch, "E602", {"points": [v(17.96, 36.48) * mm, v(17.92, 35.64) * mm, v(17.8, 35.42) * mm, v(17.36, 35.42) * mm]});
            skFitSpline(sketch, "E603", {"points": [v(17.36, 35.42) * mm, v(16.94, 35.42) * mm, v(16.8, 35.66) * mm, v(16.7, 36.48) * mm]});
            skLineSegment(sketch, "E604", {"start": v(16.7, 36.48) * mm, "end": v(16.6, 37.54) * mm});
            skLineSegment(sketch, "E605", {"start": v(16.6, 37.54) * mm, "end": v(16.55, 36.48) * mm});
            skFitSpline(sketch, "E606", {"points": [v(16.55, 36.48) * mm, v(16.5, 35.58) * mm, v(16.4, 35.42) * mm, v(15.86, 35.42) * mm]});
            skFitSpline(sketch, "E607", {"points": [v(15.86, 35.42) * mm, v(15.51, 35.41) * mm, v(14.97, 35.37) * mm, v(14.66, 35.32) * mm]});
            skFitSpline(sketch, "E608", {"points": [v(14.66, 35.32) * mm, v(14.35, 35.26) * mm, v(13.64, 35.27) * mm, v(13.08, 35.34) * mm]});
            skFitSpline(sketch, "E609", {"points": [v(19.23, 37.33) * mm, v(19.16, 37.6) * mm, v(19.1, 37.37) * mm, v(19.1, 36.83) * mm]});
            skFitSpline(sketch, "E610", {"points": [v(19.1, 36.83) * mm, v(19.1, 36.29) * mm, v(19.16, 36.07) * mm, v(19.23, 36.34) * mm]});
            skFitSpline(sketch, "E611", {"points": [v(19.23, 36.34) * mm, v(19.3, 36.6) * mm, v(19.3, 37.05) * mm, v(19.23, 37.33) * mm]});
            skFitSpline(sketch, "E612", {"points": [v(23.8, 36.48) * mm, v(23.8, 36.75) * mm, v(23.68, 37.29) * mm, v(23.55, 37.68) * mm]});
            skFitSpline(sketch, "E613", {"points": [v(23.55, 37.68) * mm, v(23.36, 38.28) * mm, v(23.32, 38.2) * mm, v(23.3, 37.18) * mm]});
            skFitSpline(sketch, "E614", {"points": [v(23.3, 37.18) * mm, v(23.28, 36.52) * mm, v(23.4, 35.98) * mm, v(23.55, 35.98) * mm]});
            skFitSpline(sketch, "E615", {"points": [v(23.55, 35.98) * mm, v(23.7, 35.98) * mm, v(23.82, 36.2) * mm, v(23.8, 36.48) * mm]});
            skFitSpline(sketch, "E616", {"points": [v(13.02, 37.17) * mm, v(12.93, 37.4) * mm, v(12.87, 37.32) * mm, v(12.85, 37) * mm]});
            skFitSpline(sketch, "E617", {"points": [v(12.85, 37) * mm, v(12.84, 36.7) * mm, v(12.9, 36.53) * mm, v(13, 36.63) * mm]});
            skFitSpline(sketch, "E618", {"points": [v(13, 36.63) * mm, v(13.1, 36.72) * mm, v(13.1, 36.96) * mm, v(13.02, 37.17) * mm]});
            skLineSegment(sketch, "E619", {"start": v(13.02, 37.17) * mm, "end": v(13.02, 37.17) * mm});
            skFitSpline(sketch, "E620", {"points": [v(21.58, 37.11) * mm, v(21.58, 37.42) * mm, v(21.46, 37.68) * mm, v(21.31, 37.68) * mm]});
            skFitSpline(sketch, "E621", {"points": [v(21.31, 37.68) * mm, v(20.93, 37.68) * mm, v(20.67, 37.16) * mm, v(20.87, 36.83) * mm]});
            skFitSpline(sketch, "E622", {"points": [v(20.87, 36.83) * mm, v(21.17, 36.35) * mm, v(21.58, 36.52) * mm, v(21.58, 37.11) * mm]});
            skFitSpline(sketch, "E623", {"points": [v(22.7, 37.11) * mm, v(22.7, 37.27) * mm, v(22.58, 37.4) * mm, v(22.43, 37.4) * mm]});
            skFitSpline(sketch, "E624", {"points": [v(22.43, 37.4) * mm, v(22.27, 37.4) * mm, v(22.14, 37.27) * mm, v(22.14, 37.11) * mm]});
            skFitSpline(sketch, "E625", {"points": [v(22.14, 37.11) * mm, v(22.14, 36.96) * mm, v(22.27, 36.83) * mm, v(22.43, 36.83) * mm]});
            skFitSpline(sketch, "E626", {"points": [v(22.43, 36.83) * mm, v(22.58, 36.83) * mm, v(22.7, 36.96) * mm, v(22.7, 37.11) * mm]});
            skFitSpline(sketch, "E627", {"points": [v(25.1, 37.96) * mm, v(25.2, 38.12) * mm, v(25.15, 38.24) * mm, v(24.98, 38.24) * mm]});
            skFitSpline(sketch, "E628", {"points": [v(24.98, 38.24) * mm, v(24.82, 38.24) * mm, v(24.68, 38.12) * mm, v(24.68, 37.96) * mm]});
            skFitSpline(sketch, "E629", {"points": [v(24.68, 37.96) * mm, v(24.68, 37.8) * mm, v(24.74, 37.68) * mm, v(24.8, 37.68) * mm]});
            skFitSpline(sketch, "E630", {"points": [v(24.8, 37.68) * mm, v(24.88, 37.68) * mm, v(25.01, 37.8) * mm, v(25.1, 37.96) * mm]});
            skFitSpline(sketch, "E631", {"points": [v(-53.07, 41.91) * mm, v(-53.17, 42.07) * mm, v(-53.5, 42.2) * mm, v(-53.82, 42.2) * mm]});
            skFitSpline(sketch, "E632", {"points": [v(-53.82, 42.2) * mm, v(-54.56, 42.2) * mm, v(-56.31, 43.94) * mm, v(-56.31, 44.67) * mm]});
            skFitSpline(sketch, "E633", {"points": [v(-56.31, 44.67) * mm, v(-56.31, 44.98) * mm, v(-56.51, 45.4) * mm, v(-56.75, 45.6) * mm]});
            skFitSpline(sketch, "E634", {"points": [v(-56.75, 45.6) * mm, v(-57.23, 45.99) * mm, v(-57.1, 47.12) * mm, v(-56.43, 48.45) * mm]});
            skFitSpline(sketch, "E635", {"points": [v(-56.43, 48.45) * mm, v(-55.98, 49.32) * mm, v(-54.57, 50.23) * mm, v(-53.31, 50.47) * mm]});
            skFitSpline(sketch, "E636", {"points": [v(-53.31, 50.47) * mm, v(-52.1, 50.7) * mm, v(-49.44, 49.37) * mm, v(-49.3, 48.47) * mm]});
            skFitSpline(sketch, "E637", {"points": [v(-49.3, 48.47) * mm, v(-49.2, 47.63) * mm, v(-49.92, 47.37) * mm, v(-50.8, 47.95) * mm]});
            skFitSpline(sketch, "E638", {"points": [v(-50.8, 47.95) * mm, v(-51.69, 48.53) * mm, v(-51.8, 48.52) * mm, v(-51.8, 47.87) * mm]});
            skFitSpline(sketch, "E639", {"points": [v(-51.8, 47.87) * mm, v(-51.8, 47.42) * mm, v(-51.55, 47.31) * mm, v(-50.39, 47.23) * mm]});
            skFitSpline(sketch, "E640", {"points": [v(-50.39, 47.23) * mm, v(-49.2, 47.15) * mm, v(-48.98, 47.2) * mm, v(-48.98, 47.63) * mm]});
            skFitSpline(sketch, "E641", {"points": [v(-48.98, 47.63) * mm, v(-48.98, 47.9) * mm, v(-48.79, 48.12) * mm, v(-48.55, 48.12) * mm]});
            skFitSpline(sketch, "E642", {"points": [v(-48.55, 48.12) * mm, v(-48, 48.12) * mm, v(-48, 48.58) * mm, v(-48.57, 48.8) * mm]});
            skFitSpline(sketch, "E643", {"points": [v(-48.57, 48.8) * mm, v(-48.86, 48.9) * mm, v(-48.98, 49.23) * mm, v(-48.93, 49.74) * mm]});
            skFitSpline(sketch, "E644", {"points": [v(-48.93, 49.74) * mm, v(-48.84, 50.5) * mm, v(-48.77, 50.52) * mm, v(-47, 50.6) * mm]});
            skFitSpline(sketch, "E645", {"points": [v(-47, 50.6) * mm, v(-42.87, 50.8) * mm, v(-41.36, 50.03) * mm, v(-41.36, 47.7) * mm]});
            skFitSpline(sketch, "E646", {"points": [v(-41.36, 47.7) * mm, v(-41.36, 46.82) * mm, v(-41.52, 46.26) * mm, v(-41.9, 45.89) * mm]});
            skFitSpline(sketch, "E647", {"points": [v(-41.9, 45.89) * mm, v(-42.38, 45.4) * mm, v(-42.4, 45.3) * mm, v(-42, 44.74) * mm]});
            skFitSpline(sketch, "E648", {"points": [v(-42, 44.74) * mm, v(-41.77, 44.4) * mm, v(-41.5, 43.8) * mm, v(-41.39, 43.4) * mm]});
            skFitSpline(sketch, "E649", {"points": [v(-41.39, 43.4) * mm, v(-41.22, 42.78) * mm, v(-41.04, 43.07) * mm, v(-40.08, 45.47) * mm]});
            skFitSpline(sketch, "E650", {"points": [v(-40.08, 45.47) * mm, v(-38.9, 48.4) * mm, v(-37.17, 50.66) * mm, v(-36.12, 50.66) * mm]});
            skFitSpline(sketch, "E651", {"points": [v(-36.12, 50.66) * mm, v(-35.29, 50.66) * mm, v(-34.52, 49.54) * mm, v(-33.3, 46.53) * mm]});
            skLineSegment(sketch, "E652", {"start": v(-33.3, 46.53) * mm, "end": v(-32.18, 43.75) * mm});
            skLineSegment(sketch, "E653", {"start": v(-32.18, 43.75) * mm, "end": v(-32.1, 46.85) * mm});
            skFitSpline(sketch, "E654", {"points": [v(-32.1, 46.85) * mm, v(-32.03, 49.9) * mm, v(-32.01, 49.96) * mm, v(-31.27, 50.3) * mm]});
            skFitSpline(sketch, "E655", {"points": [v(-31.27, 50.3) * mm, v(-30.86, 50.5) * mm, v(-30.11, 50.66) * mm, v(-29.61, 50.66) * mm]});
            skFitSpline(sketch, "E656", {"points": [v(-29.61, 50.66) * mm, v(-28.87, 50.66) * mm, v(-28.58, 50.47) * mm, v(-28.04, 49.6) * mm]});
            skLineSegment(sketch, "E657", {"start": v(-28.04, 49.6) * mm, "end": v(-27.39, 48.54) * mm});
            skLineSegment(sketch, "E658", {"start": v(-27.39, 48.54) * mm, "end": v(-27.25, 49.53) * mm});
            skFitSpline(sketch, "E659", {"points": [v(-27.25, 49.53) * mm, v(-27.13, 50.36) * mm, v(-26.98, 50.53) * mm, v(-26.32, 50.6) * mm]});
            skFitSpline(sketch, "E660", {"points": [v(-26.32, 50.6) * mm, v(-25.5, 50.7) * mm, v(-23.86, 50.12) * mm, v(-23.86, 49.74) * mm]});
            skFitSpline(sketch, "E661", {"points": [v(-23.86, 49.74) * mm, v(-23.86, 49.63) * mm, v(-23.73, 49.53) * mm, v(-23.58, 49.53) * mm]});
            skFitSpline(sketch, "E662", {"points": [v(-23.58, 49.53) * mm, v(-23.42, 49.53) * mm, v(-23.3, 49.79) * mm, v(-23.3, 50.1) * mm]});
            skFitSpline(sketch, "E663", {"points": [v(-23.3, 50.1) * mm, v(-23.3, 50.62) * mm, v(-23.1, 50.66) * mm, v(-20.47, 50.66) * mm]});
            skFitSpline(sketch, "E664", {"points": [v(-20.47, 50.66) * mm, v(-18.78, 50.66) * mm, v(-17.65, 50.55) * mm, v(-17.65, 50.38) * mm]});
            skFitSpline(sketch, "E665", {"points": [v(-17.65, 50.38) * mm, v(-17.65, 50) * mm, v(-16.71, 50.02) * mm, v(-16.34, 50.4) * mm]});
            skFitSpline(sketch, "E666", {"points": [v(-16.34, 50.4) * mm, v(-16.17, 50.56) * mm, v(-15.15, 50.65) * mm, v(-13.95, 50.6) * mm]});
            skFitSpline(sketch, "E667", {"points": [v(-13.95, 50.6) * mm, v(-11.9, 50.52) * mm, v(-11.86, 50.5) * mm, v(-11.78, 49.74) * mm]});
            skFitSpline(sketch, "E668", {"points": [v(-11.78, 49.74) * mm, v(-11.73, 49.32) * mm, v(-11.57, 48.97) * mm, v(-11.42, 48.97) * mm]});
            skFitSpline(sketch, "E669", {"points": [v(-11.42, 48.97) * mm, v(-11.28, 48.97) * mm, v(-11.16, 47.82) * mm, v(-11.16, 46.43) * mm]});
            skLineSegment(sketch, "E670", {"start": v(-11.16, 46.43) * mm, "end": v(-11.16, 43.89) * mm});
            skLineSegment(sketch, "E671", {"start": v(-11.16, 43.89) * mm, "end": v(-9.47, 43.89) * mm});
            skLineSegment(sketch, "E672", {"start": v(-9.47, 43.89) * mm, "end": v(-7.8, 43.89) * mm});
            skLineSegment(sketch, "E673", {"start": v(-7.8, 43.89) * mm, "end": v(-7.71, 47.2) * mm});
            skLineSegment(sketch, "E674", {"start": v(-7.71, 47.2) * mm, "end": v(-7.63, 50.52) * mm});
            skLineSegment(sketch, "E675", {"start": v(-7.63, 50.52) * mm, "end": v(-6.64, 50.52) * mm});
            skFitSpline(sketch, "E676", {"points": [v(-6.64, 50.52) * mm, v(-5.78, 50.52) * mm, v(-5.64, 50.42) * mm, v(-5.57, 49.74) * mm]});
            skFitSpline(sketch, "E677", {"points": [v(-5.57, 49.74) * mm, v(-5.52, 49.32) * mm, v(-5.36, 48.97) * mm, v(-5.21, 48.97) * mm]});
            skFitSpline(sketch, "E678", {"points": [v(-5.21, 48.97) * mm, v(-5.07, 48.97) * mm, v(-4.95, 47.82) * mm, v(-4.95, 46.43) * mm]});
            skLineSegment(sketch, "E679", {"start": v(-4.95, 46.43) * mm, "end": v(-4.95, 43.89) * mm});
            skLineSegment(sketch, "E680", {"start": v(-4.95, 43.89) * mm, "end": v(-3.26, 43.89) * mm});
            skLineSegment(sketch, "E681", {"start": v(-3.26, 43.89) * mm, "end": v(-1.56, 43.89) * mm});
            skLineSegment(sketch, "E682", {"start": v(-1.56, 43.89) * mm, "end": v(-1.56, 47) * mm});
            skLineSegment(sketch, "E683", {"start": v(-1.56, 47) * mm, "end": v(-1.56, 50.1) * mm});
            skLineSegment(sketch, "E684", {"start": v(-1.56, 50.1) * mm, "end": v(-0.6, 50.1) * mm});
            skFitSpline(sketch, "E685", {"points": [v(-0.6, 50.1) * mm, v(-0.06, 50.1) * mm, v(0.46, 50.22) * mm, v(0.55, 50.38) * mm]});
            skFitSpline(sketch, "E686", {"points": [v(0.55, 50.38) * mm, v(0.8, 50.78) * mm, v(5.02, 50.74) * mm, v(5.44, 50.32) * mm]});
            skFitSpline(sketch, "E687", {"points": [v(5.44, 50.32) * mm, v(5.67, 50.09) * mm, v(5.77, 48.68) * mm, v(5.77, 45.8) * mm]});
            skLineSegment(sketch, "E688", {"start": v(5.77, 45.8) * mm, "end": v(5.77, 41.63) * mm});
            skLineSegment(sketch, "E689", {"start": v(5.77, 41.63) * mm, "end": v(-3.8, 41.64) * mm});
            skFitSpline(sketch, "E690", {"points": [v(-3.8, 41.64) * mm, v(-11.06, 41.64) * mm, v(-13.41, 41.73) * mm, v(-13.54, 41.99) * mm]});
            skFitSpline(sketch, "E691", {"points": [v(-13.54, 41.99) * mm, v(-13.66, 42.26) * mm, v(-13.74, 42.26) * mm, v(-13.86, 41.98) * mm]});
            skFitSpline(sketch, "E692", {"points": [v(-13.86, 41.98) * mm, v(-13.96, 41.78) * mm, v(-14.55, 41.63) * mm, v(-15.27, 41.63) * mm]});
            skFitSpline(sketch, "E693", {"points": [v(-15.27, 41.63) * mm, v(-16.8, 41.63) * mm, v(-16.88, 41.85) * mm, v(-16.75, 45.68) * mm]});
            skFitSpline(sketch, "E694", {"points": [v(-16.75, 45.68) * mm, v(-16.7, 47.18) * mm, v(-16.7, 48.4) * mm, v(-16.73, 48.4) * mm]});
            skFitSpline(sketch, "E695", {"points": [v(-16.73, 48.4) * mm, v(-16.92, 48.4) * mm, v(-17.65, 46.27) * mm, v(-17.65, 45.73) * mm]});
            skFitSpline(sketch, "E696", {"points": [v(-17.65, 45.73) * mm, v(-17.65, 45.4) * mm, v(-17.96, 44.36) * mm, v(-18.33, 43.44) * mm]});
            skLineSegment(sketch, "E697", {"start": v(-18.33, 43.44) * mm, "end": v(-19, 41.77) * mm});
            skLineSegment(sketch, "E698", {"start": v(-19, 41.77) * mm, "end": v(-20.45, 41.68) * mm});
            skFitSpline(sketch, "E699", {"points": [v(-20.45, 41.68) * mm, v(-21.51, 41.62) * mm, v(-21.88, 41.7) * mm, v(-21.88, 41.98) * mm]});
            skFitSpline(sketch, "E700", {"points": [v(-21.88, 41.98) * mm, v(-21.88, 42.2) * mm, v(-22.32, 43.44) * mm, v(-22.86, 44.75) * mm]});
            skLineSegment(sketch, "E701", {"start": v(-22.86, 44.75) * mm, "end": v(-23.83, 47.13) * mm});
            skLineSegment(sketch, "E702", {"start": v(-23.83, 47.13) * mm, "end": v(-23.85, 44.38) * mm});
            skLineSegment(sketch, "E703", {"start": v(-23.85, 44.38) * mm, "end": v(-23.86, 41.63) * mm});
            skLineSegment(sketch, "E704", {"start": v(-23.86, 41.63) * mm, "end": v(-25.13, 41.63) * mm});
            skLineSegment(sketch, "E705", {"start": v(-25.13, 41.63) * mm, "end": v(-26.41, 41.63) * mm});
            skLineSegment(sketch, "E706", {"start": v(-26.41, 41.63) * mm, "end": v(-27.82, 43.78) * mm});
            skLineSegment(sketch, "E707", {"start": v(-27.82, 43.78) * mm, "end": v(-29.22, 45.93) * mm});
            skLineSegment(sketch, "E708", {"start": v(-29.22, 45.93) * mm, "end": v(-29.22, 43.78) * mm});
            skLineSegment(sketch, "E709", {"start": v(-29.22, 43.78) * mm, "end": v(-29.22, 41.63) * mm});
            skLineSegment(sketch, "E710", {"start": v(-29.22, 41.63) * mm, "end": v(-31.88, 41.63) * mm});
            skFitSpline(sketch, "E711", {"points": [v(-31.88, 41.63) * mm, v(-34.3, 41.63) * mm, v(-34.56, 41.68) * mm, v(-34.72, 42.2) * mm]});
            skFitSpline(sketch, "E712", {"points": [v(-34.72, 42.2) * mm, v(-34.87, 42.64) * mm, v(-35.15, 42.76) * mm, v(-36.14, 42.76) * mm]});
            skFitSpline(sketch, "E713", {"points": [v(-36.14, 42.76) * mm, v(-37.12, 42.76) * mm, v(-37.4, 42.64) * mm, v(-37.55, 42.2) * mm]});
            skFitSpline(sketch, "E714", {"points": [v(-37.55, 42.2) * mm, v(-37.71, 41.68) * mm, v(-37.97, 41.63) * mm, v(-40.63, 41.63) * mm]});
            skLineSegment(sketch, "E715", {"start": v(-40.63, 41.63) * mm, "end": v(-43.54, 41.63) * mm});
            skLineSegment(sketch, "E716", {"start": v(-43.54, 41.63) * mm, "end": v(-44.7, 43.4) * mm});
            skLineSegment(sketch, "E717", {"start": v(-44.7, 43.4) * mm, "end": v(-45.87, 45.16) * mm});
            skLineSegment(sketch, "E718", {"start": v(-45.87, 45.16) * mm, "end": v(-45.87, 43.4) * mm});
            skLineSegment(sketch, "E719", {"start": v(-45.87, 43.4) * mm, "end": v(-45.87, 41.63) * mm});
            skLineSegment(sketch, "E720", {"start": v(-45.87, 41.63) * mm, "end": v(-47, 41.63) * mm});
            skFitSpline(sketch, "E721", {"points": [v(-47, 41.63) * mm, v(-47.62, 41.63) * mm, v(-48.13, 41.75) * mm, v(-48.13, 41.9) * mm]});
            skFitSpline(sketch, "E722", {"points": [v(-48.13, 41.9) * mm, v(-48.13, 42.33) * mm, v(-49.07, 42.38) * mm, v(-50.03, 42) * mm]});
            skFitSpline(sketch, "E723", {"points": [v(-50.03, 42) * mm, v(-51.1, 41.56) * mm, v(-52.82, 41.51) * mm, v(-53.07, 41.91) * mm]});
            skLineSegment(sketch, "E724", {"start": v(-53.07, 41.91) * mm, "end": v(-53.07, 41.91) * mm});
            skFitSpline(sketch, "E725", {"points": [v(-50.4, 42.65) * mm, v(-49.27, 43.1) * mm, v(-49.26, 43.12) * mm, v(-49.26, 44.57) * mm]});
            skFitSpline(sketch, "E726", {"points": [v(-49.26, 44.57) * mm, v(-49.26, 45.37) * mm, v(-49.41, 46.18) * mm, v(-49.6, 46.37) * mm]});
            skFitSpline(sketch, "E727", {"points": [v(-49.6, 46.37) * mm, v(-49.78, 46.56) * mm, v(-50.51, 46.69) * mm, v(-51.22, 46.66) * mm]});
            skLineSegment(sketch, "E728", {"start": v(-51.22, 46.66) * mm, "end": v(-52.5, 46.62) * mm});
            skLineSegment(sketch, "E729", {"start": v(-52.5, 46.62) * mm, "end": v(-51.1, 46.45) * mm});
            skLineSegment(sketch, "E730", {"start": v(-51.1, 46.45) * mm, "end": v(-49.68, 46.29) * mm});
            skLineSegment(sketch, "E731", {"start": v(-49.68, 46.29) * mm, "end": v(-49.6, 45.12) * mm});
            skFitSpline(sketch, "E732", {"points": [v(-49.6, 45.12) * mm, v(-49.53, 44.13) * mm, v(-49.63, 43.86) * mm, v(-50.27, 43.35) * mm]});
            skFitSpline(sketch, "E733", {"points": [v(-50.27, 43.35) * mm, v(-50.69, 43.03) * mm, v(-51.4, 42.76) * mm, v(-51.85, 42.76) * mm]});
            skFitSpline(sketch, "E734", {"points": [v(-51.85, 42.76) * mm, v(-52.33, 42.76) * mm, v(-52.6, 42.64) * mm, v(-52.5, 42.48) * mm]});
            skFitSpline(sketch, "E735", {"points": [v(-52.5, 42.48) * mm, v(-52.26, 42.08) * mm, v(-51.7, 42.12) * mm, v(-50.4, 42.65) * mm]});
            skFitSpline(sketch, "E736", {"points": [v(-46.44, 44.15) * mm, v(-46.44, 45.44) * mm, v(-46.32, 46.15) * mm, v(-46.08, 46.24) * mm]});
            skFitSpline(sketch, "E737", {"points": [v(-46.08, 46.24) * mm, v(-45.83, 46.34) * mm, v(-45.82, 46.45) * mm, v(-46.04, 46.62) * mm]});
            skFitSpline(sketch, "E738", {"points": [v(-46.04, 46.62) * mm, v(-46.21, 46.75) * mm, v(-46.42, 47.04) * mm, v(-46.51, 47.27) * mm]});
            skFitSpline(sketch, "E739", {"points": [v(-46.51, 47.27) * mm, v(-46.6, 47.5) * mm, v(-46.68, 46.53) * mm, v(-46.7, 45.1) * mm]});
            skFitSpline(sketch, "E740", {"points": [v(-46.7, 45.1) * mm, v(-46.72, 42.9) * mm, v(-46.79, 42.52) * mm, v(-47.14, 42.66) * mm]});
            skFitSpline(sketch, "E741", {"points": [v(-47.14, 42.66) * mm, v(-47.38, 42.75) * mm, v(-47.57, 42.68) * mm, v(-47.57, 42.5) * mm]});
            skFitSpline(sketch, "E742", {"points": [v(-47.57, 42.5) * mm, v(-47.57, 42.33) * mm, v(-47.31, 42.2) * mm, v(-47, 42.2) * mm]});
            skFitSpline(sketch, "E743", {"points": [v(-47, 42.2) * mm, v(-46.5, 42.2) * mm, v(-46.44, 42.38) * mm, v(-46.44, 44.15) * mm]});
            skFitSpline(sketch, "E744", {"points": [v(-21.04, 42.76) * mm, v(-21.04, 43.07) * mm, v(-21.15, 43.32) * mm, v(-21.3, 43.32) * mm]});
            skFitSpline(sketch, "E745", {"points": [v(-21.3, 43.32) * mm, v(-21.43, 43.32) * mm, v(-21.48, 43.07) * mm, v(-21.4, 42.76) * mm]});
            skFitSpline(sketch, "E746", {"points": [v(-21.4, 42.76) * mm, v(-21.32, 42.45) * mm, v(-21.2, 42.2) * mm, v(-21.15, 42.2) * mm]});
            skFitSpline(sketch, "E747", {"points": [v(-21.15, 42.2) * mm, v(-21.09, 42.2) * mm, v(-21.04, 42.45) * mm, v(-21.04, 42.76) * mm]});
            skFitSpline(sketch, "E748", {"points": [v(-14.43, 42.64) * mm, v(-14.34, 42.89) * mm, v(-14.29, 44.12) * mm, v(-14.32, 45.4) * mm]});
            skLineSegment(sketch, "E749", {"start": v(-14.32, 45.4) * mm, "end": v(-14.37, 47.7) * mm});
            skLineSegment(sketch, "E750", {"start": v(-14.37, 47.7) * mm, "end": v(-14.53, 45.17) * mm});
            skFitSpline(sketch, "E751", {"points": [v(-14.53, 45.17) * mm, v(-14.68, 42.77) * mm, v(-14.72, 42.63) * mm, v(-15.4, 42.44) * mm]});
            skLineSegment(sketch, "E752", {"start": v(-15.4, 42.44) * mm, "end": v(-16.1, 42.25) * mm});
            skLineSegment(sketch, "E753", {"start": v(-16.1, 42.25) * mm, "end": v(-15.35, 42.22) * mm});
            skFitSpline(sketch, "E754", {"points": [v(-15.35, 42.22) * mm, v(-14.91, 42.2) * mm, v(-14.54, 42.38) * mm, v(-14.43, 42.64) * mm]});
            skFitSpline(sketch, "E755", {"points": [v(-11.72, 42.45) * mm, v(-11.72, 42.59) * mm, v(-11.96, 42.64) * mm, v(-12.26, 42.57) * mm]});
            skFitSpline(sketch, "E756", {"points": [v(-12.26, 42.57) * mm, v(-12.92, 42.4) * mm, v(-13.3, 42.93) * mm, v(-12.86, 43.45) * mm]});
            skFitSpline(sketch, "E757", {"points": [v(-12.86, 43.45) * mm, v(-12.42, 43.98) * mm, v(-12.6, 48.18) * mm, v(-13.06, 48.33) * mm]});
            skFitSpline(sketch, "E758", {"points": [v(-13.06, 48.33) * mm, v(-13.55, 48.5) * mm, v(-13.56, 43.02) * mm, v(-13.08, 42.53) * mm]});
            skFitSpline(sketch, "E759", {"points": [v(-13.08, 42.53) * mm, v(-12.68, 42.14) * mm, v(-11.72, 42.08) * mm, v(-11.72, 42.45) * mm]});
            skFitSpline(sketch, "E760", {"points": [v(-5.51, 42.45) * mm, v(-5.51, 42.59) * mm, v(-5.77, 42.64) * mm, v(-6.08, 42.56) * mm]});
            skFitSpline(sketch, "E761", {"points": [v(-6.08, 42.56) * mm, v(-6.39, 42.48) * mm, v(-6.64, 42.36) * mm, v(-6.64, 42.3) * mm]});
            skFitSpline(sketch, "E762", {"points": [v(-6.64, 42.3) * mm, v(-6.64, 42.24) * mm, v(-6.39, 42.2) * mm, v(-6.08, 42.2) * mm]});
            skFitSpline(sketch, "E763", {"points": [v(-6.08, 42.2) * mm, v(-5.77, 42.2) * mm, v(-5.51, 42.3) * mm, v(-5.51, 42.45) * mm]});
            skFitSpline(sketch, "E764", {"points": [v(5.21, 42.4) * mm, v(5.21, 42.52) * mm, v(4.42, 42.58) * mm, v(3.45, 42.54) * mm]});
            skFitSpline(sketch, "E765", {"points": [v(3.45, 42.54) * mm, v(0.45, 42.4) * mm, v(0.16, 42.28) * mm, v(2.74, 42.24) * mm]});
            skFitSpline(sketch, "E766", {"points": [v(2.74, 42.24) * mm, v(4.1, 42.21) * mm, v(5.2, 42.29) * mm, v(5.21, 42.4) * mm]});
            skFitSpline(sketch, "E767", {"points": [v(-19.34, 42.76) * mm, v(-19.34, 42.91) * mm, v(-19.48, 43.04) * mm, v(-19.64, 43.04) * mm]});
            skFitSpline(sketch, "E768", {"points": [v(-19.64, 43.04) * mm, v(-19.8, 43.04) * mm, v(-19.86, 42.91) * mm, v(-19.77, 42.76) * mm]});
            skFitSpline(sketch, "E769", {"points": [v(-19.77, 42.76) * mm, v(-19.67, 42.6) * mm, v(-19.54, 42.48) * mm, v(-19.47, 42.48) * mm]});
            skFitSpline(sketch, "E770", {"points": [v(-19.47, 42.48) * mm, v(-19.4, 42.48) * mm, v(-19.34, 42.6) * mm, v(-19.34, 42.76) * mm]});
            skFitSpline(sketch, "E771", {"points": [v(-7.5, 43.07) * mm, v(-7.5, 43.23) * mm, v(-7.62, 43.28) * mm, v(-7.77, 43.18) * mm]});
            skFitSpline(sketch, "E772", {"points": [v(-7.77, 43.18) * mm, v(-7.93, 43.09) * mm, v(-8.05, 42.88) * mm, v(-8.05, 42.72) * mm]});
            skFitSpline(sketch, "E773", {"points": [v(-8.05, 42.72) * mm, v(-8.05, 42.57) * mm, v(-7.93, 42.52) * mm, v(-7.77, 42.62) * mm]});
            skFitSpline(sketch, "E774", {"points": [v(-7.77, 42.62) * mm, v(-7.62, 42.71) * mm, v(-7.5, 42.92) * mm, v(-7.5, 43.07) * mm]});
            skFitSpline(sketch, "E775", {"points": [v(-33.17, 43.18) * mm, v(-33.17, 43.41) * mm, v(-33.22, 43.6) * mm, v(-33.28, 43.6) * mm]});
            skFitSpline(sketch, "E776", {"points": [v(-33.28, 43.6) * mm, v(-33.34, 43.6) * mm, v(-33.47, 43.41) * mm, v(-33.56, 43.18) * mm]});
            skFitSpline(sketch, "E777", {"points": [v(-33.56, 43.18) * mm, v(-33.65, 42.95) * mm, v(-33.6, 42.76) * mm, v(-33.45, 42.76) * mm]});
            skFitSpline(sketch, "E778", {"points": [v(-33.45, 42.76) * mm, v(-33.3, 42.76) * mm, v(-33.17, 42.95) * mm, v(-33.17, 43.18) * mm]});
            skFitSpline(sketch, "E779", {"points": [v(-30.35, 45.86) * mm, v(-30.35, 47.74) * mm, v(-30.46, 48.97) * mm, v(-30.63, 48.97) * mm]});
            skFitSpline(sketch, "E780", {"points": [v(-30.63, 48.97) * mm, v(-30.8, 48.97) * mm, v(-30.91, 47.74) * mm, v(-30.91, 45.86) * mm]});
            skFitSpline(sketch, "E781", {"points": [v(-30.91, 45.86) * mm, v(-30.91, 43.98) * mm, v(-30.8, 42.76) * mm, v(-30.63, 42.76) * mm]});
            skFitSpline(sketch, "E782", {"points": [v(-30.63, 42.76) * mm, v(-30.46, 42.76) * mm, v(-30.35, 43.98) * mm, v(-30.35, 45.86) * mm]});
            skFitSpline(sketch, "E783", {"points": [v(-16.03, 46.64) * mm, v(-16.09, 47.38) * mm, v(-16.14, 46.77) * mm, v(-16.14, 45.3) * mm]});
            skFitSpline(sketch, "E784", {"points": [v(-16.14, 45.3) * mm, v(-16.14, 43.82) * mm, v(-16.09, 43.22) * mm, v(-16.03, 43.96) * mm]});
            skFitSpline(sketch, "E785", {"points": [v(-16.03, 43.96) * mm, v(-15.97, 44.7) * mm, v(-15.97, 45.9) * mm, v(-16.03, 46.64) * mm]});
            skFitSpline(sketch, "E786", {"points": [v(-13.77, 48.04) * mm, v(-13.83, 49.1) * mm, v(-13.87, 48.3) * mm, v(-13.87, 46.29) * mm]});
            skFitSpline(sketch, "E787", {"points": [v(-13.87, 46.29) * mm, v(-13.87, 44.27) * mm, v(-13.83, 43.4) * mm, v(-13.77, 44.37) * mm]});
            skFitSpline(sketch, "E788", {"points": [v(-13.77, 44.37) * mm, v(-13.72, 45.33) * mm, v(-13.72, 46.98) * mm, v(-13.77, 48.04) * mm]});
            skLineSegment(sketch, "E789", {"start": v(-13.77, 48.04) * mm, "end": v(-13.77, 48.04) * mm});
            skFitSpline(sketch, "E790", {"points": [v(-6.54, 43.39) * mm, v(-6.41, 43.89) * mm, v(-6.3, 43.95) * mm, v(-6.03, 43.67) * mm]});
            skFitSpline(sketch, "E791", {"points": [v(-6.03, 43.67) * mm, v(-5.84, 43.48) * mm, v(-5.61, 43.32) * mm, v(-5.53, 43.32) * mm]});
            skFitSpline(sketch, "E792", {"points": [v(-5.53, 43.32) * mm, v(-5.44, 43.32) * mm, v(-5.41, 44.47) * mm, v(-5.46, 45.88) * mm]});
            skFitSpline(sketch, "E793", {"points": [v(-5.46, 45.88) * mm, v(-5.53, 47.69) * mm, v(-5.65, 48.4) * mm, v(-5.89, 48.32) * mm]});
            skFitSpline(sketch, "E794", {"points": [v(-5.89, 48.32) * mm, v(-6.07, 48.25) * mm, v(-6.44, 48.31) * mm, v(-6.71, 48.45) * mm]});
            skFitSpline(sketch, "E795", {"points": [v(-6.71, 48.45) * mm, v(-7.17, 48.68) * mm, v(-7.2, 48.47) * mm, v(-7.2, 45.73) * mm]});
            skFitSpline(sketch, "E796", {"points": [v(-7.2, 45.73) * mm, v(-7.2, 42.95) * mm, v(-6.92, 41.94) * mm, v(-6.54, 43.39) * mm]});
            skFitSpline(sketch, "E797", {"points": [v(3.44, 43.25) * mm, v(2.85, 43.3) * mm, v(1.97, 43.3) * mm, v(1.46, 43.24) * mm]});
            skFitSpline(sketch, "E798", {"points": [v(1.46, 43.24) * mm, v(0.96, 43.18) * mm, v(1.44, 43.13) * mm, v(2.53, 43.13) * mm]});
            skFitSpline(sketch, "E799", {"points": [v(2.53, 43.13) * mm, v(3.62, 43.13) * mm, v(4.03, 43.18) * mm, v(3.44, 43.25) * mm]});
            skLineSegment(sketch, "E800", {"start": v(3.44, 43.25) * mm, "end": v(3.44, 43.25) * mm});
            skFitSpline(sketch, "E801", {"points": [v(-47.92, 46.07) * mm, v(-47.99, 46.65) * mm, v(-48.04, 46.24) * mm, v(-48.04, 45.16) * mm]});
            skFitSpline(sketch, "E802", {"points": [v(-48.04, 45.16) * mm, v(-48.04, 44.07) * mm, v(-47.99, 43.6) * mm, v(-47.93, 44.1) * mm]});
            skFitSpline(sketch, "E803", {"points": [v(-47.93, 44.1) * mm, v(-47.86, 44.6) * mm, v(-47.86, 45.48) * mm, v(-47.92, 46.07) * mm]});
            skFitSpline(sketch, "E804", {"points": [v(-47.08, 46.07) * mm, v(-47.14, 46.65) * mm, v(-47.19, 46.24) * mm, v(-47.2, 45.16) * mm]});
            skFitSpline(sketch, "E805", {"points": [v(-47.2, 45.16) * mm, v(-47.2, 44.07) * mm, v(-47.14, 43.6) * mm, v(-47.08, 44.1) * mm]});
            skFitSpline(sketch, "E806", {"points": [v(-47.08, 44.1) * mm, v(-47.02, 44.6) * mm, v(-47.02, 45.48) * mm, v(-47.08, 46.07) * mm]});
            skLineSegment(sketch, "E807", {"start": v(-47.08, 46.07) * mm, "end": v(-47.08, 46.07) * mm});
            skFitSpline(sketch, "E808", {"points": [v(-42.89, 44.75) * mm, v(-43.72, 46.01) * mm, v(-43.69, 46.74) * mm, v(-42.8, 46.57) * mm]});
            skFitSpline(sketch, "E809", {"points": [v(-42.8, 46.57) * mm, v(-42.38, 46.5) * mm, v(-42.28, 46.58) * mm, v(-42.4, 46.92) * mm]});
            skFitSpline(sketch, "E810", {"points": [v(-42.4, 46.92) * mm, v(-42.5, 47.16) * mm, v(-42.46, 47.3) * mm, v(-42.32, 47.2) * mm]});
            skFitSpline(sketch, "E811", {"points": [v(-42.32, 47.2) * mm, v(-42.18, 47.12) * mm, v(-42.06, 47.34) * mm, v(-42.06, 47.7) * mm]});
            skFitSpline(sketch, "E812", {"points": [v(-42.06, 47.7) * mm, v(-42.06, 48.06) * mm, v(-42.11, 48.3) * mm, v(-42.18, 48.24) * mm]});
            skFitSpline(sketch, "E813", {"points": [v(-42.18, 48.24) * mm, v(-42.32, 48.1) * mm, v(-43.2, 49.33) * mm, v(-43.13, 49.56) * mm]});
            skFitSpline(sketch, "E814", {"points": [v(-43.13, 49.56) * mm, v(-43.1, 49.66) * mm, v(-44, 49.76) * mm, v(-45.1, 49.79) * mm]});
            skFitSpline(sketch, "E815", {"points": [v(-45.1, 49.79) * mm, v(-46.23, 49.82) * mm, v(-47.38, 49.87) * mm, v(-47.68, 49.9) * mm]});
            skFitSpline(sketch, "E816", {"points": [v(-47.68, 49.9) * mm, v(-47.97, 49.93) * mm, v(-48.28, 49.76) * mm, v(-48.36, 49.53) * mm]});
            skFitSpline(sketch, "E817", {"points": [v(-48.36, 49.53) * mm, v(-48.48, 49.17) * mm, v(-48.44, 49.16) * mm, v(-48.04, 49.5) * mm]});
            skFitSpline(sketch, "E818", {"points": [v(-48.04, 49.5) * mm, v(-47.73, 49.75) * mm, v(-47.57, 49.77) * mm, v(-47.57, 49.57) * mm]});
            skFitSpline(sketch, "E819", {"points": [v(-47.57, 49.57) * mm, v(-47.57, 49.4) * mm, v(-47.38, 49.25) * mm, v(-47.14, 49.25) * mm]});
            skFitSpline(sketch, "E820", {"points": [v(-47.14, 49.25) * mm, v(-46.9, 49.25) * mm, v(-46.72, 49.15) * mm, v(-46.72, 49.02) * mm]});
            skFitSpline(sketch, "E821", {"points": [v(-46.72, 49.02) * mm, v(-46.72, 48.9) * mm, v(-46.27, 48.85) * mm, v(-45.73, 48.91) * mm]});
            skFitSpline(sketch, "E822", {"points": [v(-45.73, 48.91) * mm, v(-44.01, 49.11) * mm, v(-42.7, 47.74) * mm, v(-43.67, 46.77) * mm]});
            skFitSpline(sketch, "E823", {"points": [v(-43.67, 46.77) * mm, v(-43.86, 46.58) * mm, v(-44.23, 46.43) * mm, v(-44.5, 46.43) * mm]});
            skFitSpline(sketch, "E824", {"points": [v(-44.5, 46.43) * mm, v(-44.86, 46.43) * mm, v(-44.95, 46.29) * mm, v(-44.83, 45.96) * mm]});
            skFitSpline(sketch, "E825", {"points": [v(-44.83, 45.96) * mm, v(-44.72, 45.68) * mm, v(-44.76, 45.56) * mm, v(-44.93, 45.66) * mm]});
            skFitSpline(sketch, "E826", {"points": [v(-44.93, 45.66) * mm, v(-45.09, 45.76) * mm, v(-45.21, 45.65) * mm, v(-45.21, 45.43) * mm]});
            skFitSpline(sketch, "E827", {"points": [v(-45.21, 45.43) * mm, v(-45.21, 45.14) * mm, v(-45.12, 45.1) * mm, v(-44.86, 45.32) * mm]});
            skFitSpline(sketch, "E828", {"points": [v(-44.86, 45.32) * mm, v(-44.43, 45.68) * mm, v(-44.05, 45.19) * mm, v(-44.35, 44.66) * mm]});
            skFitSpline(sketch, "E829", {"points": [v(-44.35, 44.66) * mm, v(-44.46, 44.47) * mm, v(-44.45, 44.4) * mm, v(-44.33, 44.51) * mm]});
            skFitSpline(sketch, "E830", {"points": [v(-44.33, 44.51) * mm, v(-44.2, 44.63) * mm, v(-43.72, 44.4) * mm, v(-43.26, 44) * mm]});
            skFitSpline(sketch, "E831", {"points": [v(-43.26, 44) * mm, v(-42.11, 43.05) * mm, v(-41.96, 43.35) * mm, v(-42.89, 44.75) * mm]});
            skFitSpline(sketch, "E832", {"points": [v(-35.5, 43.52) * mm, v(-35.77, 43.59) * mm, v(-36.28, 43.59) * mm, v(-36.63, 43.52) * mm]});
            skFitSpline(sketch, "E833", {"points": [v(-36.63, 43.52) * mm, v(-36.98, 43.45) * mm, v(-36.76, 43.4) * mm, v(-36.14, 43.4) * mm]});
            skFitSpline(sketch, "E834", {"points": [v(-36.14, 43.4) * mm, v(-35.51, 43.4) * mm, v(-35.23, 43.45) * mm, v(-35.5, 43.52) * mm]});
            skFitSpline(sketch, "E835", {"points": [v(-26.76, 43.88) * mm, v(-26.84, 44.18) * mm, v(-26.72, 44.58) * mm, v(-26.5, 44.76) * mm]});
            skFitSpline(sketch, "E836", {"points": [v(-26.5, 44.76) * mm, v(-26.06, 45.13) * mm, v(-26.06, 45.12) * mm, v(-25.6, 44.31) * mm]});
            skFitSpline(sketch, "E837", {"points": [v(-25.6, 44.31) * mm, v(-25.36, 43.87) * mm, v(-25.3, 44.43) * mm, v(-25.33, 46.85) * mm]});
            skFitSpline(sketch, "E838", {"points": [v(-25.33, 46.85) * mm, v(-25.37, 49) * mm, v(-25.41, 49.37) * mm, v(-25.48, 48.05) * mm]});
            skFitSpline(sketch, "E839", {"points": [v(-25.48, 48.05) * mm, v(-25.56, 46.52) * mm, v(-25.7, 46) * mm, v(-26.25, 45.42) * mm]});
            skLineSegment(sketch, "E840", {"start": v(-26.25, 45.42) * mm, "end": v(-26.93, 44.69) * mm});
            skLineSegment(sketch, "E841", {"start": v(-26.93, 44.69) * mm, "end": v(-27.82, 45.91) * mm});
            skFitSpline(sketch, "E842", {"points": [v(-27.82, 45.91) * mm, v(-28.3, 46.58) * mm, v(-28.89, 47.48) * mm, v(-29.11, 47.9) * mm]});
            skFitSpline(sketch, "E843", {"points": [v(-29.11, 47.9) * mm, v(-29.63, 48.9) * mm, v(-29.79, 48.89) * mm, v(-29.79, 47.84) * mm]});
            skFitSpline(sketch, "E844", {"points": [v(-29.79, 47.84) * mm, v(-29.79, 47.35) * mm, v(-29.64, 47) * mm, v(-29.43, 47) * mm]});
            skFitSpline(sketch, "E845", {"points": [v(-29.43, 47) * mm, v(-29.24, 47) * mm, v(-28.58, 46.16) * mm, v(-27.96, 45.16) * mm]});
            skFitSpline(sketch, "E846", {"points": [v(-27.96, 45.16) * mm, v(-26.79, 43.24) * mm, v(-26.52, 42.95) * mm, v(-26.76, 43.88) * mm]});
            skFitSpline(sketch, "E847", {"points": [v(-15.19, 46.36) * mm, v(-15.25, 46.94) * mm, v(-15.3, 46.46) * mm, v(-15.3, 45.3) * mm]});
            skFitSpline(sketch, "E848", {"points": [v(-15.3, 45.3) * mm, v(-15.3, 44.13) * mm, v(-15.25, 43.66) * mm, v(-15.19, 44.24) * mm]});
            skFitSpline(sketch, "E849", {"points": [v(-15.19, 44.24) * mm, v(-15.13, 44.82) * mm, v(-15.13, 45.77) * mm, v(-15.19, 46.36) * mm]});
            skFitSpline(sketch, "E850", {"points": [v(-11.72, 45.86) * mm, v(-11.72, 47.37) * mm, v(-11.84, 48.4) * mm, v(-12, 48.4) * mm]});
            skFitSpline(sketch, "E851", {"points": [v(-12, 48.4) * mm, v(-12.32, 48.4) * mm, v(-12.4, 43.82) * mm, v(-12.1, 43.51) * mm]});
            skFitSpline(sketch, "E852", {"points": [v(-12.1, 43.51) * mm, v(-11.75, 43.16) * mm, v(-11.72, 43.32) * mm, v(-11.72, 45.86) * mm]});
            skFitSpline(sketch, "E853", {"points": [v(-9.1, 43.52) * mm, v(-9.46, 43.59) * mm, v(-10.1, 43.59) * mm, v(-10.52, 43.52) * mm]});
            skFitSpline(sketch, "E854", {"points": [v(-10.52, 43.52) * mm, v(-10.95, 43.46) * mm, v(-10.67, 43.4) * mm, v(-9.89, 43.4) * mm]});
            skFitSpline(sketch, "E855", {"points": [v(-9.89, 43.4) * mm, v(-9.11, 43.4) * mm, v(-8.76, 43.45) * mm, v(-9.1, 43.52) * mm]});
            skFitSpline(sketch, "E856", {"points": [v(-2.76, 43.52) * mm, v(-3.19, 43.59) * mm, v(-3.89, 43.59) * mm, v(-4.32, 43.52) * mm]});
            skFitSpline(sketch, "E857", {"points": [v(-4.32, 43.52) * mm, v(-4.74, 43.46) * mm, v(-4.4, 43.4) * mm, v(-3.54, 43.4) * mm]});
            skFitSpline(sketch, "E858", {"points": [v(-3.54, 43.4) * mm, v(-2.69, 43.4) * mm, v(-2.34, 43.46) * mm, v(-2.76, 43.52) * mm]});
            skFitSpline(sketch, "E859", {"points": [v(-20.15, 43.89) * mm, v(-20.01, 45.04) * mm, v(-20.1, 45.88) * mm, v(-20.38, 45.98) * mm]});
            skFitSpline(sketch, "E860", {"points": [v(-20.38, 45.98) * mm, v(-20.56, 46.05) * mm, v(-20.96, 46.67) * mm, v(-21.27, 47.36) * mm]});
            skFitSpline(sketch, "E861", {"points": [v(-21.27, 47.36) * mm, v(-21.57, 48.05) * mm, v(-22, 48.72) * mm, v(-22.2, 48.84) * mm]});
            skFitSpline(sketch, "E862", {"points": [v(-22.2, 48.84) * mm, v(-22.5, 49.02) * mm, v(-22.52, 48.98) * mm, v(-22.3, 48.67) * mm]});
            skFitSpline(sketch, "E863", {"points": [v(-22.3, 48.67) * mm, v(-21.65, 47.78) * mm, v(-20.7, 44.96) * mm, v(-20.83, 44.3) * mm]});
            skFitSpline(sketch, "E864", {"points": [v(-20.83, 44.3) * mm, v(-20.91, 43.84) * mm, v(-20.83, 43.6) * mm, v(-20.57, 43.6) * mm]});
            skFitSpline(sketch, "E865", {"points": [v(-20.57, 43.6) * mm, v(-20.36, 43.6) * mm, v(-20.17, 43.73) * mm, v(-20.15, 43.89) * mm]});
            skFitSpline(sketch, "E866", {"points": [v(-19.4, 44.32) * mm, v(-19.48, 44.4) * mm, v(-19.64, 44.25) * mm, v(-19.75, 43.97) * mm]});
            skFitSpline(sketch, "E867", {"points": [v(-19.75, 43.97) * mm, v(-19.9, 43.57) * mm, v(-19.87, 43.53) * mm, v(-19.6, 43.81) * mm]});
            skFitSpline(sketch, "E868", {"points": [v(-19.6, 43.81) * mm, v(-19.4, 44) * mm, v(-19.31, 44.23) * mm, v(-19.4, 44.32) * mm]});
            skFitSpline(sketch, "E869", {"points": [v(-33.24, 44.6) * mm, v(-33.28, 44.64) * mm, v(-33.74, 44.6) * mm, v(-34.26, 44.52) * mm]});
            skFitSpline(sketch, "E870", {"points": [v(-34.26, 44.52) * mm, v(-34.86, 44.43) * mm, v(-35.08, 44.3) * mm, v(-34.85, 44.16) * mm]});
            skFitSpline(sketch, "E871", {"points": [v(-34.85, 44.16) * mm, v(-34.56, 43.98) * mm, v(-33.01, 44.4) * mm, v(-33.24, 44.6) * mm]});
            skFitSpline(sketch, "E872", {"points": [v(-24.78, 47.77) * mm, v(-24.84, 48.5) * mm, v(-24.89, 47.9) * mm, v(-24.89, 46.43) * mm]});
            skFitSpline(sketch, "E873", {"points": [v(-24.89, 46.43) * mm, v(-24.89, 44.95) * mm, v(-24.84, 44.35) * mm, v(-24.78, 45.09) * mm]});
            skFitSpline(sketch, "E874", {"points": [v(-24.78, 45.09) * mm, v(-24.72, 45.82) * mm, v(-24.72, 47.03) * mm, v(-24.78, 47.77) * mm]});
            skFitSpline(sketch, "E875", {"points": [v(-35.92, 44.35) * mm, v(-36.1, 44.43) * mm, v(-36.5, 44.44) * mm, v(-36.77, 44.36) * mm]});
            skFitSpline(sketch, "E876", {"points": [v(-36.77, 44.36) * mm, v(-37.04, 44.3) * mm, v(-36.88, 44.23) * mm, v(-36.42, 44.22) * mm]});
            skFitSpline(sketch, "E877", {"points": [v(-36.42, 44.22) * mm, v(-35.95, 44.22) * mm, v(-35.73, 44.28) * mm, v(-35.92, 44.35) * mm]});
            skFitSpline(sketch, "E878", {"points": [v(-52.15, 44.76) * mm, v(-52.42, 44.91) * mm, v(-52.72, 45.54) * mm, v(-52.82, 46.16) * mm]});
            skFitSpline(sketch, "E879", {"points": [v(-52.82, 46.16) * mm, v(-52.97, 47.07) * mm, v(-53.08, 47.22) * mm, v(-53.39, 46.96) * mm]});
            skFitSpline(sketch, "E880", {"points": [v(-53.39, 46.96) * mm, v(-54.3, 46.2) * mm, v(-53.37, 44.43) * mm, v(-52.09, 44.46) * mm]});
            skFitSpline(sketch, "E881", {"points": [v(-52.09, 44.46) * mm, v(-51.74, 44.47) * mm, v(-51.75, 44.52) * mm, v(-52.15, 44.76) * mm]});
            skFitSpline(sketch, "E882", {"points": [v(-50.2, 45.5) * mm, v(-50.26, 45.78) * mm, v(-50.33, 45.62) * mm, v(-50.33, 45.16) * mm]});
            skFitSpline(sketch, "E883", {"points": [v(-50.33, 45.16) * mm, v(-50.34, 44.7) * mm, v(-50.28, 44.47) * mm, v(-50.2, 44.66) * mm]});
            skFitSpline(sketch, "E884", {"points": [v(-50.2, 44.66) * mm, v(-50.13, 44.85) * mm, v(-50.12, 45.23) * mm, v(-50.2, 45.5) * mm]});
            skFitSpline(sketch, "E885", {"points": [v(-21.63, 45.55) * mm, v(-21.8, 46.05) * mm, v(-22, 46.4) * mm, v(-22.06, 46.35) * mm]});
            skFitSpline(sketch, "E886", {"points": [v(-22.06, 46.35) * mm, v(-22.12, 46.29) * mm, v(-22.03, 45.83) * mm, v(-21.85, 45.33) * mm]});
            skFitSpline(sketch, "E887", {"points": [v(-21.85, 45.33) * mm, v(-21.68, 44.83) * mm, v(-21.49, 44.47) * mm, v(-21.43, 44.53) * mm]});
            skFitSpline(sketch, "E888", {"points": [v(-21.43, 44.53) * mm, v(-21.37, 44.6) * mm, v(-21.46, 45.05) * mm, v(-21.63, 45.55) * mm]});
            skLineSegment(sketch, "E889", {"start": v(4.65, 46.14) * mm, "end": v(4.65, 47.84) * mm});
            skLineSegment(sketch, "E890", {"start": v(4.65, 47.84) * mm, "end": v(3.02, 47.79) * mm});
            skLineSegment(sketch, "E891", {"start": v(3.02, 47.79) * mm, "end": v(1.4, 47.74) * mm});
            skLineSegment(sketch, "E892", {"start": v(1.4, 47.74) * mm, "end": v(2.76, 47.63) * mm});
            skLineSegment(sketch, "E893", {"start": v(2.76, 47.63) * mm, "end": v(4.11, 47.52) * mm});
            skLineSegment(sketch, "E894", {"start": v(4.11, 47.52) * mm, "end": v(4.03, 46.2) * mm});
            skLineSegment(sketch, "E895", {"start": v(4.03, 46.2) * mm, "end": v(3.94, 44.87) * mm});
            skLineSegment(sketch, "E896", {"start": v(3.94, 44.87) * mm, "end": v(2.67, 44.7) * mm});
            skLineSegment(sketch, "E897", {"start": v(2.67, 44.7) * mm, "end": v(1.4, 44.54) * mm});
            skLineSegment(sketch, "E898", {"start": v(1.4, 44.54) * mm, "end": v(3.02, 44.5) * mm});
            skLineSegment(sketch, "E899", {"start": v(3.02, 44.5) * mm, "end": v(4.65, 44.45) * mm});
            skLineSegment(sketch, "E900", {"start": v(4.65, 44.45) * mm, "end": v(4.65, 46.14) * mm});
            skFitSpline(sketch, "E901", {"points": [v(-18.4, 45.16) * mm, v(-18.3, 45.39) * mm, v(-18.36, 45.58) * mm, v(-18.5, 45.58) * mm]});
            skFitSpline(sketch, "E902", {"points": [v(-18.5, 45.58) * mm, v(-18.66, 45.58) * mm, v(-18.78, 45.39) * mm, v(-18.78, 45.16) * mm]});
            skFitSpline(sketch, "E903", {"points": [v(-18.78, 45.16) * mm, v(-18.78, 44.92) * mm, v(-18.73, 44.73) * mm, v(-18.67, 44.73) * mm]});
            skFitSpline(sketch, "E904", {"points": [v(-18.67, 44.73) * mm, v(-18.6, 44.73) * mm, v(-18.48, 44.92) * mm, v(-18.4, 45.16) * mm]});
            skFitSpline(sketch, "E905", {"points": [v(-37.81, 46.92) * mm, v(-37.53, 47.74) * mm, v(-37.2, 48.4) * mm, v(-37.07, 48.4) * mm]});
            skFitSpline(sketch, "E906", {"points": [v(-37.07, 48.4) * mm, v(-36.94, 48.4) * mm, v(-36.84, 48.6) * mm, v(-36.84, 48.83) * mm]});
            skFitSpline(sketch, "E907", {"points": [v(-36.84, 48.83) * mm, v(-36.84, 49.5) * mm, v(-37.22, 49.32) * mm, v(-37.88, 48.33) * mm]});
            skFitSpline(sketch, "E908", {"points": [v(-37.88, 48.33) * mm, v(-38.85, 46.88) * mm, v(-39.4, 45.35) * mm, v(-39, 45.2) * mm]});
            skFitSpline(sketch, "E909", {"points": [v(-39, 45.2) * mm, v(-38.54, 45.04) * mm, v(-38.4, 45.24) * mm, v(-37.81, 46.92) * mm]});
            skFitSpline(sketch, "E910", {"points": [v(0.41, 46.14) * mm, v(0.41, 46.27) * mm, v(0.22, 46.44) * mm, v(-0.01, 46.53) * mm]});
            skFitSpline(sketch, "E911", {"points": [v(-0.01, 46.53) * mm, v(-0.3, 46.64) * mm, v(-0.43, 46.51) * mm, v(-0.43, 46.14) * mm]});
            skFitSpline(sketch, "E912", {"points": [v(-0.43, 46.14) * mm, v(-0.43, 45.77) * mm, v(-0.3, 45.65) * mm, v(-0.01, 45.76) * mm]});
            skFitSpline(sketch, "E913", {"points": [v(-0.01, 45.76) * mm, v(0.22, 45.85) * mm, v(0.41, 46.02) * mm, v(0.41, 46.14) * mm]});
            skFitSpline(sketch, "E914", {"points": [v(-55.37, 46.72) * mm, v(-55.27, 47.19) * mm, v(-54.87, 47.9) * mm, v(-54.47, 48.3) * mm]});
            skFitSpline(sketch, "E915", {"points": [v(-54.47, 48.3) * mm, v(-53.84, 48.93) * mm, v(-53.56, 49) * mm, v(-52.28, 48.9) * mm]});
            skFitSpline(sketch, "E916", {"points": [v(-52.28, 48.9) * mm, v(-51.47, 48.84) * mm, v(-50.56, 48.7) * mm, v(-50.25, 48.59) * mm]});
            skFitSpline(sketch, "E917", {"points": [v(-50.25, 48.59) * mm, v(-49.73, 48.4) * mm, v(-50.73, 48.9) * mm, v(-52.27, 49.6) * mm]});
            skFitSpline(sketch, "E918", {"points": [v(-52.27, 49.6) * mm, v(-53.16, 50.01) * mm, v(-54.3, 49.63) * mm, v(-55.37, 48.56) * mm]});
            skFitSpline(sketch, "E919", {"points": [v(-55.37, 48.56) * mm, v(-56.25, 47.68) * mm, v(-56.6, 46.52) * mm, v(-56.13, 46.05) * mm]});
            skFitSpline(sketch, "E920", {"points": [v(-56.13, 46.05) * mm, v(-55.76, 45.68) * mm, v(-55.54, 45.87) * mm, v(-55.37, 46.72) * mm]});
            skFitSpline(sketch, "E921", {"points": [v(-36.28, 46.1) * mm, v(-36.28, 46.46) * mm, v(-37.1, 47.44) * mm, v(-37.11, 47.08) * mm]});
            skFitSpline(sketch, "E922", {"points": [v(-37.11, 47.08) * mm, v(-37.12, 46.9) * mm, v(-37.2, 46.55) * mm, v(-37.3, 46.3) * mm]});
            skFitSpline(sketch, "E923", {"points": [v(-37.3, 46.3) * mm, v(-37.42, 45.99) * mm, v(-37.3, 45.86) * mm, v(-36.87, 45.86) * mm]});
            skFitSpline(sketch, "E924", {"points": [v(-36.87, 45.86) * mm, v(-36.54, 45.86) * mm, v(-36.28, 45.97) * mm, v(-36.28, 46.1) * mm]});
            skFitSpline(sketch, "E925", {"points": [v(2.95, 46.14) * mm, v(2.95, 46.3) * mm, v(2.63, 46.43) * mm, v(2.25, 46.43) * mm]});
            skFitSpline(sketch, "E926", {"points": [v(2.25, 46.43) * mm, v(1.86, 46.43) * mm, v(1.54, 46.3) * mm, v(1.54, 46.14) * mm]});
            skFitSpline(sketch, "E927", {"points": [v(1.54, 46.14) * mm, v(1.54, 45.99) * mm, v(1.86, 45.86) * mm, v(2.25, 45.86) * mm]});
            skFitSpline(sketch, "E928", {"points": [v(2.25, 45.86) * mm, v(2.63, 45.86) * mm, v(2.95, 45.99) * mm, v(2.95, 46.14) * mm]});
            skFitSpline(sketch, "E929", {"points": [v(-26.68, 46.68) * mm, v(-26.68, 46.82) * mm, v(-26.89, 47.01) * mm, v(-27.14, 47.1) * mm]});
            skFitSpline(sketch, "E930", {"points": [v(-27.14, 47.1) * mm, v(-27.53, 47.26) * mm, v(-27.55, 47.22) * mm, v(-27.25, 46.86) * mm]});
            skFitSpline(sketch, "E931", {"points": [v(-27.25, 46.86) * mm, v(-26.84, 46.37) * mm, v(-26.68, 46.32) * mm, v(-26.68, 46.68) * mm]});
            skFitSpline(sketch, "E932", {"points": [v(-35.4, 47.46) * mm, v(-35.73, 48.04) * mm, v(-35.8, 47.85) * mm, v(-35.54, 47.14) * mm]});
            skFitSpline(sketch, "E933", {"points": [v(-35.54, 47.14) * mm, v(-35.44, 46.9) * mm, v(-35.3, 46.74) * mm, v(-35.23, 46.82) * mm]});
            skFitSpline(sketch, "E934", {"points": [v(-35.23, 46.82) * mm, v(-35.16, 46.89) * mm, v(-35.23, 47.18) * mm, v(-35.4, 47.46) * mm]});
            skFitSpline(sketch, "E935", {"points": [v(-22.41, 47.46) * mm, v(-22.75, 48.04) * mm, v(-22.83, 47.85) * mm, v(-22.55, 47.14) * mm]});
            skFitSpline(sketch, "E936", {"points": [v(-22.55, 47.14) * mm, v(-22.46, 46.9) * mm, v(-22.32, 46.74) * mm, v(-22.25, 46.82) * mm]});
            skFitSpline(sketch, "E937", {"points": [v(-22.25, 46.82) * mm, v(-22.17, 46.89) * mm, v(-22.25, 47.18) * mm, v(-22.41, 47.46) * mm]});
            skFitSpline(sketch, "E938", {"points": [v(-44.21, 47.25) * mm, v(-43.63, 47.62) * mm, v(-44.1, 48.12) * mm, v(-45.04, 48.12) * mm]});
            skFitSpline(sketch, "E939", {"points": [v(-45.04, 48.12) * mm, v(-46.36, 48.12) * mm, v(-46.14, 47.3) * mm, v(-44.74, 47.03) * mm]});
            skFitSpline(sketch, "E940", {"points": [v(-44.74, 47.03) * mm, v(-44.67, 47.01) * mm, v(-44.43, 47.11) * mm, v(-44.21, 47.25) * mm]});
            skLineSegment(sketch, "E941", {"start": v(-19.81, 48.47) * mm, "end": v(-19.37, 49.53) * mm});
            skLineSegment(sketch, "E942", {"start": v(-19.37, 49.53) * mm, "end": v(-20.46, 49.53) * mm});
            skLineSegment(sketch, "E943", {"start": v(-20.46, 49.53) * mm, "end": v(-21.55, 49.53) * mm});
            skLineSegment(sketch, "E944", {"start": v(-21.55, 49.53) * mm, "end": v(-21, 48.38) * mm});
            skFitSpline(sketch, "E945", {"points": [v(-21, 48.38) * mm, v(-20.68, 47.74) * mm, v(-20.4, 47.26) * mm, v(-20.34, 47.32) * mm]});
            skFitSpline(sketch, "E946", {"points": [v(-20.34, 47.32) * mm, v(-20.3, 47.37) * mm, v(-20.05, 47.9) * mm, v(-19.81, 48.47) * mm]});
            skFitSpline(sketch, "E947", {"points": [v(5.11, 49.32) * mm, v(5.04, 49.51) * mm, v(4.97, 49.35) * mm, v(4.97, 48.97) * mm]});
            skFitSpline(sketch, "E948", {"points": [v(4.97, 48.97) * mm, v(4.97, 48.58) * mm, v(5.04, 48.42) * mm, v(5.11, 48.61) * mm]});
            skFitSpline(sketch, "E949", {"points": [v(5.11, 48.61) * mm, v(5.2, 48.8) * mm, v(5.2, 49.13) * mm, v(5.11, 49.32) * mm]});
            skFitSpline(sketch, "E950", {"points": [v(-14.61, 49.16) * mm, v(-14.88, 49.23) * mm, v(-15.4, 49.23) * mm, v(-15.74, 49.17) * mm]});
            skFitSpline(sketch, "E951", {"points": [v(-15.74, 49.17) * mm, v(-16.1, 49.1) * mm, v(-15.87, 49.04) * mm, v(-15.25, 49.04) * mm]});
            skFitSpline(sketch, "E952", {"points": [v(-15.25, 49.04) * mm, v(-14.63, 49.03) * mm, v(-14.34, 49.1) * mm, v(-14.61, 49.16) * mm]});
            skFitSpline(sketch, "E953", {"points": [v(-28.84, 49.6) * mm, v(-28.91, 49.72) * mm, v(-29.29, 49.81) * mm, v(-29.68, 49.81) * mm]});
            skFitSpline(sketch, "E954", {"points": [v(-29.68, 49.81) * mm, v(-30.07, 49.81) * mm, v(-30.32, 49.72) * mm, v(-30.25, 49.6) * mm]});
            skFitSpline(sketch, "E955", {"points": [v(-30.25, 49.6) * mm, v(-30.18, 49.49) * mm, v(-29.8, 49.4) * mm, v(-29.42, 49.4) * mm]});
            skFitSpline(sketch, "E956", {"points": [v(-29.42, 49.4) * mm, v(-29.03, 49.4) * mm, v(-28.77, 49.49) * mm, v(-28.84, 49.6) * mm]});
            skFitSpline(sketch, "E957", {"points": [v(-35.85, 49.81) * mm, v(-35.76, 49.97) * mm, v(-35.81, 50.1) * mm, v(-35.98, 50.1) * mm]});
            skFitSpline(sketch, "E958", {"points": [v(-35.98, 50.1) * mm, v(-36.14, 50.1) * mm, v(-36.28, 49.97) * mm, v(-36.28, 49.81) * mm]});
            skFitSpline(sketch, "E959", {"points": [v(-36.28, 49.81) * mm, v(-36.28, 49.66) * mm, v(-36.22, 49.53) * mm, v(-36.15, 49.53) * mm]});
            skFitSpline(sketch, "E960", {"points": [v(-36.15, 49.53) * mm, v(-36.08, 49.53) * mm, v(-35.95, 49.66) * mm, v(-35.85, 49.81) * mm]});
            skFitSpline(sketch, "E961", {"points": [v(11.26, 42) * mm, v(11.18, 42.2) * mm, v(11.15, 43.82) * mm, v(11.2, 45.6) * mm]});
            skLineSegment(sketch, "E962", {"start": v(11.2, 45.6) * mm, "end": v(11.28, 48.83) * mm});
            skLineSegment(sketch, "E963", {"start": v(11.28, 48.83) * mm, "end": v(12.05, 48.91) * mm});
            skFitSpline(sketch, "E964", {"points": [v(12.05, 48.91) * mm, v(12.71, 49) * mm, v(12.83, 49.14) * mm, v(12.83, 49.87) * mm]});
            skLineSegment(sketch, "E965", {"start": v(12.83, 49.87) * mm, "end": v(12.83, 50.74) * mm});
            skLineSegment(sketch, "E966", {"start": v(12.83, 50.74) * mm, "end": v(14.83, 50.57) * mm});
            skFitSpline(sketch, "E967", {"points": [v(14.83, 50.57) * mm, v(16.94, 50.4) * mm, v(17.92, 49.95) * mm, v(18.94, 48.72) * mm]});
            skLineSegment(sketch, "E968", {"start": v(18.94, 48.72) * mm, "end": v(19.55, 47.98) * mm});
            skLineSegment(sketch, "E969", {"start": v(19.55, 47.98) * mm, "end": v(19.4, 48.72) * mm});
            skFitSpline(sketch, "E970", {"points": [v(19.4, 48.72) * mm, v(19.16, 50.03) * mm, v(19.73, 50.66) * mm, v(21.17, 50.66) * mm]});
            skLineSegment(sketch, "E971", {"start": v(21.17, 50.66) * mm, "end": v(22.43, 50.66) * mm});
            skLineSegment(sketch, "E972", {"start": v(22.43, 50.66) * mm, "end": v(22.43, 49.42) * mm});
            skLineSegment(sketch, "E973", {"start": v(22.43, 49.42) * mm, "end": v(22.43, 48.18) * mm});
            skLineSegment(sketch, "E974", {"start": v(22.43, 48.18) * mm, "end": v(23.36, 49.1) * mm});
            skFitSpline(sketch, "E975", {"points": [v(23.36, 49.1) * mm, v(23.87, 49.62) * mm, v(24.78, 50.17) * mm, v(25.39, 50.34) * mm]});
            skFitSpline(sketch, "E976", {"points": [v(25.39, 50.34) * mm, v(26.38, 50.61) * mm, v(26.68, 50.56) * mm, v(28.27, 49.8) * mm]});
            skFitSpline(sketch, "E977", {"points": [v(28.27, 49.8) * mm, v(30.08, 48.95) * mm, v(30.4, 48.48) * mm, v(29.6, 47.82) * mm]});
            skFitSpline(sketch, "E978", {"points": [v(29.6, 47.82) * mm, v(29.24, 47.52) * mm, v(29.02, 47.54) * mm, v(28.36, 47.93) * mm]});
            skFitSpline(sketch, "E979", {"points": [v(28.36, 47.93) * mm, v(27.34, 48.53) * mm, v(27.22, 48.52) * mm, v(27.22, 47.84) * mm]});
            skFitSpline(sketch, "E980", {"points": [v(27.22, 47.84) * mm, v(27.22, 47.35) * mm, v(27.41, 47.27) * mm, v(28.61, 47.27) * mm]});
            skFitSpline(sketch, "E981", {"points": [v(28.61, 47.27) * mm, v(29.46, 47.27) * mm, v(30.05, 47.14) * mm, v(30.14, 46.92) * mm]});
            skFitSpline(sketch, "E982", {"points": [v(30.14, 46.92) * mm, v(30.3, 46.55) * mm, v(30.42, 47.84) * mm, v(30.34, 48.88) * mm]});
            skFitSpline(sketch, "E983", {"points": [v(30.34, 48.88) * mm, v(30.24, 50.1) * mm, v(30.8, 50.66) * mm, v(32.15, 50.66) * mm]});
            skFitSpline(sketch, "E984", {"points": [v(32.15, 50.66) * mm, v(32.87, 50.66) * mm, v(33.44, 50.51) * mm, v(33.53, 50.3) * mm]});
            skFitSpline(sketch, "E985", {"points": [v(33.53, 50.3) * mm, v(33.64, 50.03) * mm, v(33.67, 50.03) * mm, v(33.7, 50.3) * mm]});
            skFitSpline(sketch, "E986", {"points": [v(33.7, 50.3) * mm, v(33.7, 50.57) * mm, v(34.68, 50.66) * mm, v(37.52, 50.66) * mm]});
            skLineSegment(sketch, "E987", {"start": v(37.52, 50.66) * mm, "end": v(41.33, 50.66) * mm});
            skLineSegment(sketch, "E988", {"start": v(41.33, 50.66) * mm, "end": v(41.33, 49.4) * mm});
            skLineSegment(sketch, "E989", {"start": v(41.33, 49.4) * mm, "end": v(41.33, 48.12) * mm});
            skLineSegment(sketch, "E990", {"start": v(41.33, 48.12) * mm, "end": v(40.06, 48.12) * mm});
            skLineSegment(sketch, "E991", {"start": v(40.06, 48.12) * mm, "end": v(38.8, 48.12) * mm});
            skLineSegment(sketch, "E992", {"start": v(38.8, 48.12) * mm, "end": v(38.8, 44.87) * mm});
            skLineSegment(sketch, "E993", {"start": v(38.8, 44.87) * mm, "end": v(38.8, 41.63) * mm});
            skLineSegment(sketch, "E994", {"start": v(38.8, 41.63) * mm, "end": v(37.79, 41.63) * mm});
            skFitSpline(sketch, "E995", {"points": [v(37.79, 41.63) * mm, v(36.18, 41.63) * mm, v(35.97, 42.05) * mm, v(35.97, 45.25) * mm]});
            skLineSegment(sketch, "E996", {"start": v(35.97, 45.25) * mm, "end": v(35.97, 48.06) * mm});
            skLineSegment(sketch, "E997", {"start": v(35.97, 48.06) * mm, "end": v(34.7, 48.16) * mm});
            skLineSegment(sketch, "E998", {"start": v(34.7, 48.16) * mm, "end": v(33.43, 48.27) * mm});
            skLineSegment(sketch, "E999", {"start": v(33.43, 48.27) * mm, "end": v(33.43, 45.4) * mm});
            skFitSpline(sketch, "E1000", {"points": [v(33.43, 45.4) * mm, v(33.43, 43.81) * mm, v(33.35, 42.32) * mm, v(33.26, 42.08) * mm]});
            skFitSpline(sketch, "E1001", {"points": [v(33.26, 42.08) * mm, v(33.03, 41.47) * mm, v(30.93, 41.46) * mm, v(30.5, 42.07) * mm]});
            skFitSpline(sketch, "E1002", {"points": [v(30.5, 42.07) * mm, v(30.2, 42.46) * mm, v(30.07, 42.46) * mm, v(29.13, 42.07) * mm]});
            skFitSpline(sketch, "E1003", {"points": [v(29.13, 42.07) * mm, v(27.65, 41.45) * mm, v(26.64, 41.52) * mm, v(25, 42.37) * mm]});
            skFitSpline(sketch, "E1004", {"points": [v(25, 42.37) * mm, v(23.95, 42.91) * mm, v(23.43, 43.41) * mm, v(23, 44.27) * mm]});
            skLineSegment(sketch, "E1005", {"start": v(23, 44.27) * mm, "end": v(22.43, 45.44) * mm});
            skLineSegment(sketch, "E1006", {"start": v(22.43, 45.44) * mm, "end": v(22.43, 43.98) * mm});
            skFitSpline(sketch, "E1007", {"points": [v(22.43, 43.98) * mm, v(22.43, 41.85) * mm, v(22.28, 41.63) * mm, v(20.87, 41.63) * mm]});
            skFitSpline(sketch, "E1008", {"points": [v(20.87, 41.63) * mm, v(19.58, 41.63) * mm, v(19.32, 41.9) * mm, v(19.32, 43.24) * mm]});
            skLineSegment(sketch, "E1009", {"start": v(19.32, 43.24) * mm, "end": v(19.32, 43.96) * mm});
            skLineSegment(sketch, "E1010", {"start": v(19.32, 43.96) * mm, "end": v(18.7, 43.19) * mm});
            skFitSpline(sketch, "E1011", {"points": [v(18.7, 43.19) * mm, v(18.37, 42.76) * mm, v(17.68, 42.23) * mm, v(17.17, 42.02) * mm]});
            skFitSpline(sketch, "E1012", {"points": [v(17.17, 42.02) * mm, v(15.92, 41.5) * mm, v(11.46, 41.48) * mm, v(11.26, 42) * mm]});
            skFitSpline(sketch, "E1013", {"points": [v(21.69, 42.64) * mm, v(21.78, 42.89) * mm, v(21.84, 44.12) * mm, v(21.8, 45.4) * mm]});
            skLineSegment(sketch, "E1014", {"start": v(21.8, 45.4) * mm, "end": v(21.75, 47.7) * mm});
            skLineSegment(sketch, "E1015", {"start": v(21.75, 47.7) * mm, "end": v(21.6, 45.17) * mm});
            skFitSpline(sketch, "E1016", {"points": [v(21.6, 45.17) * mm, v(21.45, 42.77) * mm, v(21.4, 42.63) * mm, v(20.73, 42.44) * mm]});
            skLineSegment(sketch, "E1017", {"start": v(20.73, 42.44) * mm, "end": v(20.03, 42.25) * mm});
            skLineSegment(sketch, "E1018", {"start": v(20.03, 42.25) * mm, "end": v(20.77, 42.22) * mm});
            skFitSpline(sketch, "E1019", {"points": [v(20.77, 42.22) * mm, v(21.21, 42.2) * mm, v(21.59, 42.38) * mm, v(21.69, 42.64) * mm]});
            skFitSpline(sketch, "E1020", {"points": [v(29.16, 42.83) * mm, v(29.8, 43.13) * mm, v(29.92, 43.4) * mm, v(30, 44.56) * mm]});
            skFitSpline(sketch, "E1021", {"points": [v(30, 44.56) * mm, v(30.04, 45.32) * mm, v(29.94, 46.08) * mm, v(29.78, 46.24) * mm]});
            skFitSpline(sketch, "E1022", {"points": [v(29.78, 46.24) * mm, v(29.57, 46.45) * mm, v(29.48, 46.1) * mm, v(29.48, 45.07) * mm]});
            skFitSpline(sketch, "E1023", {"points": [v(29.48, 45.07) * mm, v(29.48, 43.56) * mm, v(29.32, 43.35) * mm, v(28.63, 43.96) * mm]});
            skFitSpline(sketch, "E1024", {"points": [v(28.63, 43.96) * mm, v(28.3, 44.26) * mm, v(28.3, 44.24) * mm, v(28.6, 43.84) * mm]});
            skFitSpline(sketch, "E1025", {"points": [v(28.6, 43.84) * mm, v(28.9, 43.44) * mm, v(28.86, 43.31) * mm, v(28.39, 43.06) * mm]});
            skFitSpline(sketch, "E1026", {"points": [v(28.39, 43.06) * mm, v(28.08, 42.9) * mm, v(27.56, 42.76) * mm, v(27.24, 42.76) * mm]});
            skFitSpline(sketch, "E1027", {"points": [v(27.24, 42.76) * mm, v(26.92, 42.76) * mm, v(26.66, 42.62) * mm, v(26.66, 42.44) * mm]});
            skFitSpline(sketch, "E1028", {"points": [v(26.66, 42.44) * mm, v(26.66, 42.07) * mm, v(28, 42.28) * mm, v(29.16, 42.83) * mm]});
            skFitSpline(sketch, "E1029", {"points": [v(32.7, 42.64) * mm, v(32.8, 42.89) * mm, v(32.84, 44.12) * mm, v(32.81, 45.4) * mm]});
            skLineSegment(sketch, "E1030", {"start": v(32.81, 45.4) * mm, "end": v(32.76, 47.7) * mm});
            skLineSegment(sketch, "E1031", {"start": v(32.76, 47.7) * mm, "end": v(32.6, 45.17) * mm});
            skFitSpline(sketch, "E1032", {"points": [v(32.6, 45.17) * mm, v(32.45, 42.77) * mm, v(32.4, 42.63) * mm, v(31.74, 42.44) * mm]});
            skLineSegment(sketch, "E1033", {"start": v(31.74, 42.44) * mm, "end": v(31.03, 42.25) * mm});
            skLineSegment(sketch, "E1034", {"start": v(31.03, 42.25) * mm, "end": v(31.78, 42.22) * mm});
            skFitSpline(sketch, "E1035", {"points": [v(31.78, 42.22) * mm, v(32.22, 42.2) * mm, v(32.6, 42.38) * mm, v(32.7, 42.64) * mm]});
            skFitSpline(sketch, "E1036", {"points": [v(37.62, 46.2) * mm, v(37.54, 47.95) * mm, v(37.41, 48.46) * mm, v(36.98, 48.77) * mm]});
            skFitSpline(sketch, "E1037", {"points": [v(36.98, 48.77) * mm, v(36.69, 49) * mm, v(36.52, 49.35) * mm, v(36.6, 49.58) * mm]});
            skFitSpline(sketch, "E1038", {"points": [v(36.6, 49.58) * mm, v(36.73, 49.91) * mm, v(36.52, 49.96) * mm, v(35.38, 49.81) * mm]});
            skFitSpline(sketch, "E1039", {"points": [v(35.38, 49.81) * mm, v(34.62, 49.71) * mm, v(33.91, 49.54) * mm, v(33.8, 49.43) * mm]});
            skFitSpline(sketch, "E1040", {"points": [v(33.8, 49.43) * mm, v(33.46, 49.08) * mm, v(34.35, 48.7) * mm, v(35.48, 48.69) * mm]});
            skLineSegment(sketch, "E1041", {"start": v(35.48, 48.69) * mm, "end": v(36.54, 48.68) * mm});
            skLineSegment(sketch, "E1042", {"start": v(36.54, 48.68) * mm, "end": v(36.54, 45.85) * mm});
            skFitSpline(sketch, "E1043", {"points": [v(36.54, 45.85) * mm, v(36.54, 43.97) * mm, v(36.66, 42.89) * mm, v(36.89, 42.63) * mm]});
            skFitSpline(sketch, "E1044", {"points": [v(36.89, 42.63) * mm, v(37.42, 42.05) * mm, v(37.74, 43.59) * mm, v(37.62, 46.2) * mm]});
            skFitSpline(sketch, "E1045", {"points": [v(12.83, 42.88) * mm, v(12.83, 42.95) * mm, v(12.7, 43.09) * mm, v(12.55, 43.18) * mm]});
            skFitSpline(sketch, "E1046", {"points": [v(12.55, 43.18) * mm, v(12.4, 43.28) * mm, v(12.27, 43.22) * mm, v(12.27, 43.06) * mm]});
            skFitSpline(sketch, "E1047", {"points": [v(12.27, 43.06) * mm, v(12.27, 42.9) * mm, v(12.4, 42.76) * mm, v(12.55, 42.76) * mm]});
            skFitSpline(sketch, "E1048", {"points": [v(12.55, 42.76) * mm, v(12.7, 42.76) * mm, v(12.83, 42.81) * mm, v(12.83, 42.88) * mm]});
            skFitSpline(sketch, "E1049", {"points": [v(14.88, 42.94) * mm, v(14.68, 43.02) * mm, v(14.36, 43.02) * mm, v(14.17, 42.94) * mm]});
            skFitSpline(sketch, "E1050", {"points": [v(14.17, 42.94) * mm, v(13.98, 42.87) * mm, v(14.14, 42.8) * mm, v(14.52, 42.8) * mm]});
            skFitSpline(sketch, "E1051", {"points": [v(14.52, 42.8) * mm, v(14.91, 42.8) * mm, v(15.07, 42.87) * mm, v(14.88, 42.94) * mm]});
            skFitSpline(sketch, "E1052", {"points": [v(20.1, 46.5) * mm, v(20.03, 47.16) * mm, v(19.98, 46.55) * mm, v(19.99, 45.16) * mm]});
            skFitSpline(sketch, "E1053", {"points": [v(19.99, 45.16) * mm, v(19.99, 43.76) * mm, v(20.03, 43.22) * mm, v(20.1, 43.97) * mm]});
            skFitSpline(sketch, "E1054", {"points": [v(20.1, 43.97) * mm, v(20.15, 44.7) * mm, v(20.15, 45.85) * mm, v(20.1, 46.5) * mm]});
            skLineSegment(sketch, "E1055", {"start": v(20.1, 46.5) * mm, "end": v(20.1, 46.5) * mm});
            skFitSpline(sketch, "E1056", {"points": [v(31.1, 46.64) * mm, v(31.04, 47.38) * mm, v(31, 46.77) * mm, v(31, 45.3) * mm]});
            skFitSpline(sketch, "E1057", {"points": [v(31, 45.3) * mm, v(31, 43.82) * mm, v(31.04, 43.22) * mm, v(31.1, 43.96) * mm]});
            skFitSpline(sketch, "E1058", {"points": [v(31.1, 43.96) * mm, v(31.16, 44.7) * mm, v(31.16, 45.9) * mm, v(31.1, 46.64) * mm]});
            skFitSpline(sketch, "E1059", {"points": [v(20.94, 46.36) * mm, v(20.88, 46.94) * mm, v(20.83, 46.46) * mm, v(20.83, 45.3) * mm]});
            skFitSpline(sketch, "E1060", {"points": [v(20.83, 45.3) * mm, v(20.83, 44.13) * mm, v(20.88, 43.66) * mm, v(20.94, 44.24) * mm]});
            skFitSpline(sketch, "E1061", {"points": [v(20.94, 44.24) * mm, v(21, 44.82) * mm, v(21, 45.77) * mm, v(20.94, 46.36) * mm]});
            skFitSpline(sketch, "E1062", {"points": [v(30.53, 45.5) * mm, v(30.47, 45.94) * mm, v(30.41, 45.59) * mm, v(30.41, 44.73) * mm]});
            skFitSpline(sketch, "E1063", {"points": [v(30.41, 44.73) * mm, v(30.41, 43.88) * mm, v(30.47, 43.53) * mm, v(30.53, 43.96) * mm]});
            skFitSpline(sketch, "E1064", {"points": [v(30.53, 43.96) * mm, v(30.6, 44.38) * mm, v(30.6, 45.08) * mm, v(30.53, 45.5) * mm]});
            skFitSpline(sketch, "E1065", {"points": [v(31.94, 46.36) * mm, v(31.88, 46.94) * mm, v(31.83, 46.46) * mm, v(31.83, 45.3) * mm]});
            skFitSpline(sketch, "E1066", {"points": [v(31.83, 45.3) * mm, v(31.83, 44.13) * mm, v(31.88, 43.66) * mm, v(31.94, 44.24) * mm]});
            skFitSpline(sketch, "E1067", {"points": [v(31.94, 44.24) * mm, v(32, 44.82) * mm, v(32, 45.77) * mm, v(31.94, 46.36) * mm]});
            skFitSpline(sketch, "E1068", {"points": [v(15.16, 43.79) * mm, v(14.97, 43.87) * mm, v(14.6, 43.87) * mm, v(14.32, 43.8) * mm]});
            skFitSpline(sketch, "E1069", {"points": [v(14.32, 43.8) * mm, v(14.04, 43.73) * mm, v(14.2, 43.67) * mm, v(14.66, 43.66) * mm]});
            skFitSpline(sketch, "E1070", {"points": [v(14.66, 43.66) * mm, v(15.13, 43.65) * mm, v(15.35, 43.71) * mm, v(15.16, 43.79) * mm]});
            skFitSpline(sketch, "E1071", {"points": [v(13.4, 44.87) * mm, v(13.4, 45.26) * mm, v(13.27, 45.58) * mm, v(13.11, 45.58) * mm]});
            skFitSpline(sketch, "E1072", {"points": [v(13.11, 45.58) * mm, v(12.96, 45.58) * mm, v(12.83, 45.26) * mm, v(12.83, 44.87) * mm]});
            skFitSpline(sketch, "E1073", {"points": [v(12.83, 44.87) * mm, v(12.83, 44.49) * mm, v(12.96, 44.17) * mm, v(13.11, 44.17) * mm]});
            skFitSpline(sketch, "E1074", {"points": [v(13.11, 44.17) * mm, v(13.27, 44.17) * mm, v(13.4, 44.49) * mm, v(13.4, 44.87) * mm]});
            skFitSpline(sketch, "E1075", {"points": [v(16.35, 45.02) * mm, v(16.9, 45.58) * mm, v(16.9, 45.58) * mm, v(15.43, 45.58) * mm]});
            skFitSpline(sketch, "E1076", {"points": [v(15.43, 45.58) * mm, v(14.03, 45.58) * mm, v(13.96, 45.54) * mm, v(13.96, 44.84) * mm]});
            skFitSpline(sketch, "E1077", {"points": [v(13.96, 44.84) * mm, v(13.96, 44.15) * mm, v(14.03, 44.11) * mm, v(14.87, 44.28) * mm]});
            skFitSpline(sketch, "E1078", {"points": [v(14.87, 44.28) * mm, v(15.38, 44.38) * mm, v(16.04, 44.72) * mm, v(16.35, 45.02) * mm]});
            skFitSpline(sketch, "E1079", {"points": [v(27.2, 44.64) * mm, v(26.67, 44.78) * mm, v(26.1, 45.9) * mm, v(26.1, 46.78) * mm]});
            skFitSpline(sketch, "E1080", {"points": [v(26.1, 46.78) * mm, v(26.1, 47.23) * mm, v(26.01, 47.3) * mm, v(25.78, 47.07) * mm]});
            skFitSpline(sketch, "E1081", {"points": [v(25.78, 47.07) * mm, v(24.89, 46.18) * mm, v(25.77, 44.41) * mm, v(27.07, 44.48) * mm]});
            skFitSpline(sketch, "E1082", {"points": [v(27.07, 44.48) * mm, v(27.48, 44.5) * mm, v(27.52, 44.55) * mm, v(27.2, 44.64) * mm]});
            skFitSpline(sketch, "E1083", {"points": [v(19.52, 46.64) * mm, v(19.44, 46.91) * mm, v(19.39, 46.69) * mm, v(19.39, 46.14) * mm]});
            skFitSpline(sketch, "E1084", {"points": [v(19.39, 46.14) * mm, v(19.39, 45.6) * mm, v(19.44, 45.38) * mm, v(19.52, 45.65) * mm]});
            skFitSpline(sketch, "E1085", {"points": [v(19.52, 45.65) * mm, v(19.59, 45.92) * mm, v(19.59, 46.37) * mm, v(19.52, 46.64) * mm]});
            skFitSpline(sketch, "E1086", {"points": [v(23.9, 46.92) * mm, v(24.17, 47.97) * mm, v(25.34, 48.97) * mm, v(26.3, 48.97) * mm]});
            skFitSpline(sketch, "E1087", {"points": [v(26.3, 48.97) * mm, v(26.73, 48.97) * mm, v(26.94, 49.1) * mm, v(26.86, 49.32) * mm]});
            skFitSpline(sketch, "E1088", {"points": [v(26.86, 49.32) * mm, v(26.7, 49.8) * mm, v(25.1, 49.69) * mm, v(24.23, 49.11) * mm]});
            skFitSpline(sketch, "E1089", {"points": [v(24.23, 49.11) * mm, v(23.42, 48.58) * mm, v(22.59, 46.86) * mm, v(22.83, 46.23) * mm]});
            skFitSpline(sketch, "E1090", {"points": [v(22.83, 46.23) * mm, v(23.08, 45.58) * mm, v(23.65, 45.95) * mm, v(23.9, 46.92) * mm]});
            skFitSpline(sketch, "E1091", {"points": [v(29.06, 46.59) * mm, v(28.14, 46.85) * mm, v(26.74, 46.84) * mm, v(26.84, 46.57) * mm]});
            skFitSpline(sketch, "E1092", {"points": [v(26.84, 46.57) * mm, v(26.9, 46.4) * mm, v(27.46, 46.32) * mm, v(28.15, 46.4) * mm]});
            skFitSpline(sketch, "E1093", {"points": [v(28.15, 46.4) * mm, v(28.8, 46.46) * mm, v(29.21, 46.55) * mm, v(29.06, 46.59) * mm]});
            skFitSpline(sketch, "E1094", {"points": [v(13.3, 47.48) * mm, v(13.24, 47.75) * mm, v(13.17, 47.6) * mm, v(13.17, 47.13) * mm]});
            skFitSpline(sketch, "E1095", {"points": [v(13.17, 47.13) * mm, v(13.16, 46.67) * mm, v(13.22, 46.44) * mm, v(13.3, 46.63) * mm]});
            skFitSpline(sketch, "E1096", {"points": [v(13.3, 46.63) * mm, v(13.37, 46.82) * mm, v(13.38, 47.2) * mm, v(13.3, 47.48) * mm]});
            skLineSegment(sketch, "E1097", {"start": v(13.3, 47.48) * mm, "end": v(13.3, 47.48) * mm});
            skFitSpline(sketch, "E1098", {"points": [v(12.83, 47.27) * mm, v(12.83, 47.58) * mm, v(12.7, 47.84) * mm, v(12.55, 47.84) * mm]});
            skFitSpline(sketch, "E1099", {"points": [v(12.55, 47.84) * mm, v(12.4, 47.84) * mm, v(12.27, 47.58) * mm, v(12.27, 47.27) * mm]});
            skFitSpline(sketch, "E1100", {"points": [v(12.27, 47.27) * mm, v(12.27, 46.96) * mm, v(12.4, 46.7) * mm, v(12.55, 46.7) * mm]});
            skFitSpline(sketch, "E1101", {"points": [v(12.55, 46.7) * mm, v(12.7, 46.7) * mm, v(12.83, 46.96) * mm, v(12.83, 47.27) * mm]});
            skFitSpline(sketch, "E1102", {"points": [v(16.5, 46.98) * mm, v(16.5, 47.38) * mm, v(15.52, 47.84) * mm, v(14.68, 47.84) * mm]});
            skFitSpline(sketch, "E1103", {"points": [v(14.68, 47.84) * mm, v(14.15, 47.84) * mm, v(13.96, 47.7) * mm, v(13.96, 47.27) * mm]});
            skFitSpline(sketch, "E1104", {"points": [v(13.96, 47.27) * mm, v(13.96, 46.8) * mm, v(14.15, 46.7) * mm, v(15.23, 46.7) * mm]});
            skFitSpline(sketch, "E1105", {"points": [v(15.23, 46.7) * mm, v(15.93, 46.7) * mm, v(16.5, 46.83) * mm, v(16.5, 46.98) * mm]});
            skFitSpline(sketch, "E1106", {"points": [v(18.47, 46.97) * mm, v(18.47, 47.58) * mm, v(16.95, 48.97) * mm, v(15.99, 49.24) * mm]});
            skFitSpline(sketch, "E1107", {"points": [v(15.99, 49.24) * mm, v(14.67, 49.6) * mm, v(13.96, 49.6) * mm, v(13.96, 49.25) * mm]});
            skFitSpline(sketch, "E1108", {"points": [v(13.96, 49.25) * mm, v(13.96, 49.1) * mm, v(14.33, 48.97) * mm, v(14.79, 48.97) * mm]});
            skFitSpline(sketch, "E1109", {"points": [v(14.79, 48.97) * mm, v(16.08, 48.97) * mm, v(17.04, 48.48) * mm, v(17.57, 47.56) * mm]});
            skFitSpline(sketch, "E1110", {"points": [v(17.57, 47.56) * mm, v(18.04, 46.73) * mm, v(18.47, 46.45) * mm, v(18.47, 46.97) * mm]});
            skFitSpline(sketch, "E1111", {"points": [v(28.8, 48.83) * mm, v(28.5, 49.06) * mm, v(27.98, 49.23) * mm, v(27.66, 49.22) * mm]});
            skFitSpline(sketch, "E1112", {"points": [v(27.66, 49.22) * mm, v(27.1, 49.18) * mm, v(27.1, 49.18) * mm, v(27.65, 49.05) * mm]});
            skFitSpline(sketch, "E1113", {"points": [v(27.65, 49.05) * mm, v(27.96, 48.97) * mm, v(28.33, 48.8) * mm, v(28.48, 48.66) * mm]});
            skFitSpline(sketch, "E1114", {"points": [v(28.48, 48.66) * mm, v(28.63, 48.52) * mm, v(28.88, 48.4) * mm, v(29.04, 48.41) * mm]});
            skFitSpline(sketch, "E1115", {"points": [v(29.04, 48.41) * mm, v(29.2, 48.42) * mm, v(29.1, 48.6) * mm, v(28.8, 48.83) * mm]});
            skFitSpline(sketch, "E1116", {"points": [v(21.51, 49.16) * mm, v(21.24, 49.23) * mm, v(20.73, 49.23) * mm, v(20.38, 49.17) * mm]});
            skFitSpline(sketch, "E1117", {"points": [v(20.38, 49.17) * mm, v(20.03, 49.1) * mm, v(20.25, 49.04) * mm, v(20.87, 49.04) * mm]});
            skFitSpline(sketch, "E1118", {"points": [v(20.87, 49.04) * mm, v(21.5, 49.03) * mm, v(21.78, 49.1) * mm, v(21.51, 49.16) * mm]});
            skFitSpline(sketch, "E1119", {"points": [v(32.52, 49.16) * mm, v(32.25, 49.23) * mm, v(31.74, 49.23) * mm, v(31.39, 49.17) * mm]});
            skFitSpline(sketch, "E1120", {"points": [v(31.39, 49.17) * mm, v(31.04, 49.1) * mm, v(31.26, 49.04) * mm, v(31.88, 49.04) * mm]});
            skFitSpline(sketch, "E1121", {"points": [v(31.88, 49.04) * mm, v(32.5, 49.03) * mm, v(32.79, 49.1) * mm, v(32.52, 49.16) * mm]});
            skFitSpline(sketch, "E1122", {"points": [v(39.72, 49.45) * mm, v(39.37, 49.51) * mm, v(38.73, 49.52) * mm, v(38.3, 49.45) * mm]});
            skFitSpline(sketch, "E1123", {"points": [v(38.3, 49.45) * mm, v(37.88, 49.39) * mm, v(38.16, 49.33) * mm, v(38.94, 49.33) * mm]});
            skFitSpline(sketch, "E1124", {"points": [v(38.94, 49.33) * mm, v(39.71, 49.33) * mm, v(40.06, 49.38) * mm, v(39.72, 49.45) * mm]});
            skFitSpline(sketch, "E1125", {"points": [v(41.05, 42.12) * mm, v(41.05, 42.38) * mm, v(41.63, 43.98) * mm, v(42.35, 45.67) * mm]});
            skFitSpline(sketch, "E1126", {"points": [v(42.35, 45.67) * mm, v(43.55, 48.53) * mm, v(44.37, 49.81) * mm, v(44.97, 49.81) * mm]});
            skFitSpline(sketch, "E1127", {"points": [v(44.97, 49.81) * mm, v(45.11, 49.81) * mm, v(45.3, 50) * mm, v(45.39, 50.24) * mm]});
            skFitSpline(sketch, "E1128", {"points": [v(45.39, 50.24) * mm, v(45.63, 50.87) * mm, v(46.51, 50.75) * mm, v(47.22, 50) * mm]});
            skFitSpline(sketch, "E1129", {"points": [v(47.22, 50) * mm, v(47.56, 49.63) * mm, v(48.4, 48.02) * mm, v(49.09, 46.4) * mm]});
            skLineSegment(sketch, "E1130", {"start": v(49.09, 46.4) * mm, "end": v(50.33, 43.46) * mm});
            skLineSegment(sketch, "E1131", {"start": v(50.33, 43.46) * mm, "end": v(50.42, 47) * mm});
            skLineSegment(sketch, "E1132", {"start": v(50.42, 47) * mm, "end": v(50.5, 50.52) * mm});
            skLineSegment(sketch, "E1133", {"start": v(50.5, 50.52) * mm, "end": v(51.5, 50.52) * mm});
            skFitSpline(sketch, "E1134", {"points": [v(51.5, 50.52) * mm, v(52.36, 50.52) * mm, v(52.5, 50.42) * mm, v(52.57, 49.74) * mm]});
            skFitSpline(sketch, "E1135", {"points": [v(52.57, 49.74) * mm, v(52.62, 49.32) * mm, v(52.78, 48.97) * mm, v(52.92, 48.97) * mm]});
            skFitSpline(sketch, "E1136", {"points": [v(52.92, 48.97) * mm, v(53.07, 48.97) * mm, v(53.19, 47.82) * mm, v(53.19, 46.43) * mm]});
            skLineSegment(sketch, "E1137", {"start": v(53.19, 46.43) * mm, "end": v(53.19, 43.89) * mm});
            skLineSegment(sketch, "E1138", {"start": v(53.19, 43.89) * mm, "end": v(55.16, 43.89) * mm});
            skLineSegment(sketch, "E1139", {"start": v(55.16, 43.89) * mm, "end": v(57.14, 43.89) * mm});
            skLineSegment(sketch, "E1140", {"start": v(57.14, 43.89) * mm, "end": v(57.14, 42.76) * mm});
            skLineSegment(sketch, "E1141", {"start": v(57.14, 42.76) * mm, "end": v(57.14, 41.63) * mm});
            skLineSegment(sketch, "E1142", {"start": v(57.14, 41.63) * mm, "end": v(52.45, 41.64) * mm});
            skFitSpline(sketch, "E1143", {"points": [v(52.45, 41.64) * mm, v(48.05, 41.66) * mm, v(47.76, 41.7) * mm, v(47.62, 42.2) * mm]});
            skFitSpline(sketch, "E1144", {"points": [v(47.62, 42.2) * mm, v(47.41, 43.01) * mm, v(45.15, 43) * mm, v(44.72, 42.2) * mm]});
            skFitSpline(sketch, "E1145", {"points": [v(44.72, 42.2) * mm, v(44.47, 41.73) * mm, v(44.13, 41.63) * mm, v(42.74, 41.63) * mm]});
            skFitSpline(sketch, "E1146", {"points": [v(42.74, 41.63) * mm, v(41.33, 41.63) * mm, v(41.05, 41.7) * mm, v(41.05, 42.12) * mm]});
            skFitSpline(sketch, "E1147", {"points": [v(52.62, 42.44) * mm, v(52.62, 42.58) * mm, v(52.4, 42.68) * mm, v(52.14, 42.66) * mm]});
            skFitSpline(sketch, "E1148", {"points": [v(52.14, 42.66) * mm, v(51.87, 42.63) * mm, v(51.6, 42.86) * mm, v(51.55, 43.15) * mm]});
            skFitSpline(sketch, "E1149", {"points": [v(51.55, 43.15) * mm, v(51.46, 43.58) * mm, v(51.56, 43.65) * mm, v(52.1, 43.51) * mm]});
            skLineSegment(sketch, "E1150", {"start": v(52.1, 43.51) * mm, "end": v(52.76, 43.35) * mm});
            skLineSegment(sketch, "E1151", {"start": v(52.76, 43.35) * mm, "end": v(52.67, 45.9) * mm});
            skFitSpline(sketch, "E1152", {"points": [v(52.67, 45.9) * mm, v(52.6, 47.7) * mm, v(52.49, 48.4) * mm, v(52.25, 48.32) * mm]});
            skFitSpline(sketch, "E1153", {"points": [v(52.25, 48.32) * mm, v(52.07, 48.25) * mm, v(51.7, 48.31) * mm, v(51.42, 48.45) * mm]});
            skFitSpline(sketch, "E1154", {"points": [v(51.42, 48.45) * mm, v(50.97, 48.68) * mm, v(50.93, 48.48) * mm, v(50.93, 45.86) * mm]});
            skFitSpline(sketch, "E1155", {"points": [v(50.93, 45.86) * mm, v(50.93, 42.92) * mm, v(51.16, 42.23) * mm, v(52.13, 42.2) * mm]});
            skFitSpline(sketch, "E1156", {"points": [v(52.13, 42.2) * mm, v(52.4, 42.2) * mm, v(52.62, 42.3) * mm, v(52.62, 42.44) * mm]});
            skFitSpline(sketch, "E1157", {"points": [v(49.24, 43.04) * mm, v(49.24, 43.2) * mm, v(49.18, 43.32) * mm, v(49.11, 43.32) * mm]});
            skFitSpline(sketch, "E1158", {"points": [v(49.11, 43.32) * mm, v(49.04, 43.32) * mm, v(48.9, 43.2) * mm, v(48.81, 43.04) * mm]});
            skFitSpline(sketch, "E1159", {"points": [v(48.81, 43.04) * mm, v(48.72, 42.88) * mm, v(48.77, 42.76) * mm, v(48.94, 42.76) * mm]});
            skFitSpline(sketch, "E1160", {"points": [v(48.94, 42.76) * mm, v(49.1, 42.76) * mm, v(49.24, 42.88) * mm, v(49.24, 43.04) * mm]});
            skFitSpline(sketch, "E1161", {"points": [v(46.77, 43.52) * mm, v(46.42, 43.59) * mm, v(45.85, 43.59) * mm, v(45.5, 43.52) * mm]});
            skFitSpline(sketch, "E1162", {"points": [v(45.5, 43.52) * mm, v(45.15, 43.45) * mm, v(45.43, 43.4) * mm, v(46.13, 43.4) * mm]});
            skFitSpline(sketch, "E1163", {"points": [v(46.13, 43.4) * mm, v(46.83, 43.4) * mm, v(47.12, 43.45) * mm, v(46.77, 43.52) * mm]});
            skFitSpline(sketch, "E1164", {"points": [v(48.34, 43.98) * mm, v(48.4, 44.32) * mm, v(48.25, 44.44) * mm, v(47.78, 44.42) * mm]});
            skFitSpline(sketch, "E1165", {"points": [v(47.78, 44.42) * mm, v(47.3, 44.4) * mm, v(47.25, 44.35) * mm, v(47.61, 44.26) * mm]});
            skFitSpline(sketch, "E1166", {"points": [v(47.61, 44.26) * mm, v(48.16, 44.11) * mm, v(48.27, 43.73) * mm, v(47.82, 43.5) * mm]});
            skFitSpline(sketch, "E1167", {"points": [v(47.82, 43.5) * mm, v(47.66, 43.43) * mm, v(47.7, 43.4) * mm, v(47.89, 43.44) * mm]});
            skFitSpline(sketch, "E1168", {"points": [v(47.89, 43.44) * mm, v(48.09, 43.48) * mm, v(48.29, 43.72) * mm, v(48.34, 43.98) * mm]});
            skFitSpline(sketch, "E1169", {"points": [v(55.37, 43.52) * mm, v(54.95, 43.59) * mm, v(54.25, 43.59) * mm, v(53.82, 43.52) * mm]});
            skFitSpline(sketch, "E1170", {"points": [v(53.82, 43.52) * mm, v(53.4, 43.46) * mm, v(53.74, 43.4) * mm, v(54.6, 43.4) * mm]});
            skFitSpline(sketch, "E1171", {"points": [v(54.6, 43.4) * mm, v(55.45, 43.4) * mm, v(55.8, 43.46) * mm, v(55.37, 43.52) * mm]});
            skFitSpline(sketch, "E1172", {"points": [v(46.03, 44.4) * mm, v(45.58, 44.45) * mm, v(45.1, 44.38) * mm, v(44.97, 44.25) * mm]});
            skFitSpline(sketch, "E1173", {"points": [v(44.97, 44.25) * mm, v(44.83, 44.1) * mm, v(45.17, 44.06) * mm, v(45.78, 44.15) * mm]});
            skFitSpline(sketch, "E1174", {"points": [v(45.78, 44.15) * mm, v(46.75, 44.28) * mm, v(46.77, 44.3) * mm, v(46.03, 44.4) * mm]});
            skFitSpline(sketch, "E1175", {"points": [v(47.68, 45.02) * mm, v(47.59, 45.17) * mm, v(47.36, 45.3) * mm, v(47.17, 45.3) * mm]});
            skFitSpline(sketch, "E1176", {"points": [v(47.17, 45.3) * mm, v(46.97, 45.3) * mm, v(47, 45.18) * mm, v(47.26, 45.02) * mm]});
            skFitSpline(sketch, "E1177", {"points": [v(47.26, 45.02) * mm, v(47.8, 44.67) * mm, v(47.9, 44.67) * mm, v(47.68, 45.02) * mm]});
            skFitSpline(sketch, "E1178", {"points": [v(44.47, 46.78) * mm, v(44.92, 48) * mm, v(45.2, 48.39) * mm, v(45.5, 48.27) * mm]});
            skFitSpline(sketch, "E1179", {"points": [v(45.5, 48.27) * mm, v(45.86, 48.14) * mm, v(45.87, 48.18) * mm, v(45.57, 48.54) * mm]});
            skFitSpline(sketch, "E1180", {"points": [v(45.57, 48.54) * mm, v(45.38, 48.77) * mm, v(45.32, 48.97) * mm, v(45.44, 48.97) * mm]});
            skFitSpline(sketch, "E1181", {"points": [v(45.44, 48.97) * mm, v(45.56, 48.97) * mm, v(45.59, 49.04) * mm, v(45.5, 49.13) * mm]});
            skFitSpline(sketch, "E1182", {"points": [v(45.5, 49.13) * mm, v(45.23, 49.4) * mm, v(44.12, 48.13) * mm, v(44.33, 47.78) * mm]});
            skFitSpline(sketch, "E1183", {"points": [v(44.33, 47.78) * mm, v(44.44, 47.61) * mm, v(44.41, 47.54) * mm, v(44.27, 47.62) * mm]});
            skFitSpline(sketch, "E1184", {"points": [v(44.27, 47.62) * mm, v(44.13, 47.7) * mm, v(43.75, 47.18) * mm, v(43.43, 46.46) * mm]});
            skFitSpline(sketch, "E1185", {"points": [v(43.43, 46.46) * mm, v(42.87, 45.22) * mm, v(42.87, 45.14) * mm, v(43.34, 45.14) * mm]});
            skFitSpline(sketch, "E1186", {"points": [v(43.34, 45.14) * mm, v(43.7, 45.14) * mm, v(44.03, 45.62) * mm, v(44.47, 46.78) * mm]});
            skFitSpline(sketch, "E1187", {"points": [v(45.9, 46.36) * mm, v(45.76, 46.63) * mm, v(45.6, 47.01) * mm, v(45.53, 47.22) * mm]});
            skFitSpline(sketch, "E1188", {"points": [v(45.53, 47.22) * mm, v(45.47, 47.42) * mm, v(45.27, 47.2) * mm, v(45.1, 46.72) * mm]});
            skFitSpline(sketch, "E1189", {"points": [v(45.1, 46.72) * mm, v(44.79, 45.9) * mm, v(44.8, 45.86) * mm, v(45.46, 45.86) * mm]});
            skFitSpline(sketch, "E1190", {"points": [v(45.46, 45.86) * mm, v(46.03, 45.86) * mm, v(46.1, 45.95) * mm, v(45.9, 46.36) * mm]});
            skFitSpline(sketch, "E1191", {"points": [v(-59.68, 56.47) * mm, v(-59.7, 57.44) * mm, v(-59.53, 57.79) * mm, v(-58.67, 58.66) * mm]});
            skFitSpline(sketch, "E1192", {"points": [v(-58.67, 58.66) * mm, v(-57.76, 59.56) * mm, v(-57.47, 59.69) * mm, v(-56.34, 59.66) * mm]});
            skFitSpline(sketch, "E1193", {"points": [v(-56.34, 59.66) * mm, v(-55.18, 59.64) * mm, v(-55.13, 59.61) * mm, v(-55.9, 59.43) * mm]});
            skFitSpline(sketch, "E1194", {"points": [v(-55.9, 59.43) * mm, v(-57.59, 59.02) * mm, v(-58.91, 57.75) * mm, v(-59.43, 56.05) * mm]});
            skFitSpline(sketch, "E1195", {"points": [v(-59.43, 56.05) * mm, v(-59.62, 55.4) * mm, v(-59.66, 55.46) * mm, v(-59.68, 56.47) * mm]});
            skFitSpline(sketch, "E1196", {"points": [v(59.4, 55.92) * mm, v(59.4, 57.2) * mm, v(57.57, 59.02) * mm, v(55.87, 59.43) * mm]});
            skFitSpline(sketch, "E1197", {"points": [v(55.87, 59.43) * mm, v(55.11, 59.61) * mm, v(55.16, 59.64) * mm, v(56.32, 59.66) * mm]});
            skFitSpline(sketch, "E1198", {"points": [v(56.32, 59.66) * mm, v(57.45, 59.69) * mm, v(57.74, 59.56) * mm, v(58.64, 58.66) * mm]});
            skFitSpline(sketch, "E1199", {"points": [v(58.64, 58.66) * mm, v(59.48, 57.82) * mm, v(59.68, 57.4) * mm, v(59.68, 56.54) * mm]});
            skFitSpline(sketch, "E1200", {"points": [v(59.68, 56.54) * mm, v(59.68, 55.94) * mm, v(59.62, 55.46) * mm, v(59.54, 55.46) * mm]});
            skFitSpline(sketch, "E1201", {"points": [v(59.54, 55.46) * mm, v(59.46, 55.46) * mm, v(59.4, 55.67) * mm, v(59.4, 55.92) * mm]});
            skSolve(sketch);
        }
        {
            var Q0;
            Q0=qCreatedBy(makeId("Front.planeOp"),FACE);
            var sketch = newSketch(context, id + "F1", { "sketchPlane" : qUnion([Q0])});
            skLineSegment(sketch, "E1202", {"start": v(0, 55.85) * mm, "end": v(0, -70.46) * mm, "construction": true});
            skLineSegment(sketch, "E1203", {"start": v(-65.88, 0) * mm, "end": v(69.26, 0) * mm, "construction": true});
            skLineSegment(sketch, "E1204", {"start": v(-50, 30.13) * mm, "end": v(50, 30.13) * mm});
            skLineSegment(sketch, "E1205", {"start": v(50, -55.7) * mm, "end": v(-50, -55.7) * mm});
            skLineSegment(sketch, "E1206", {"start": v(-50, 30.13) * mm, "end": v(-50, -55.7) * mm});
            skLineSegment(sketch, "E1207", {"start": v(50, 30.13) * mm, "end": v(50, -55.7) * mm});
            skSolve(sketch);
        }
        {
            var Q0;
            Q0=qCreatedBy(makeId("Front.planeOp"),FACE);
            var sketch = newSketch(context, id + "F2", { "sketchPlane" : qUnion([Q0])});
            skFitSpline(sketch, "E1208.0.0", {"points": [v(-37.25, 2.99) * mm, v(-36.15, -1.7) * mm, v(-32.86, -5.9) * mm, v(-28.57, -8.09) * mm]});
            skFitSpline(sketch, "E1208.0.1", {"points": [v(-28.57, -8.09) * mm, v(-25.44, -9.68) * mm, v(-20.93, -10.12) * mm, v(-17.25, -9.18) * mm]});
            skFitSpline(sketch, "E1208.0.2", {"points": [v(-17.25, -9.18) * mm, v(-12.55, -7.98) * mm, v(-8.8, -4.9) * mm, v(-6.65, -0.5) * mm]});
            skFitSpline(sketch, "E1208.0.3", {"points": [v(-6.65, -0.5) * mm, v(-4.94, 3.03) * mm, v(-4.55, 6.68) * mm, v(-5.5, 10.42) * mm]});
            skFitSpline(sketch, "E1208.0.4", {"points": [v(-5.5, 10.42) * mm, v(-6.3, 13.52) * mm, v(-7.59, 15.77) * mm, v(-9.88, 18.09) * mm]});
            skFitSpline(sketch, "E1208.0.5", {"points": [v(-9.88, 18.09) * mm, v(-12.18, 20.4) * mm, v(-14.94, 21.92) * mm, v(-18.07, 22.58) * mm]});
            skFitSpline(sketch, "E1208.0.6", {"points": [v(-18.07, 22.58) * mm, v(-20.56, 23.1) * mm, v(-22.07, 23.1) * mm, v(-24.56, 22.58) * mm]});
            skFitSpline(sketch, "E1208.0.7", {"points": [v(-24.56, 22.58) * mm, v(-33.48, 20.7) * mm, v(-39.3, 11.7) * mm, v(-37.25, 2.99) * mm]});
            skFitSpline(sketch, "E1209.0.0", {"points": [v(4.94, 6.63) * mm, v(4.94, -0.58) * mm, v(10.47, -7.58) * mm, v(17.51, -9.29) * mm]});
            skFitSpline(sketch, "E1209.0.1", {"points": [v(17.51, -9.29) * mm, v(19.73, -9.82) * mm, v(23.05, -9.83) * mm, v(25.12, -9.3) * mm]});
            skFitSpline(sketch, "E1209.0.2", {"points": [v(25.12, -9.3) * mm, v(34.06, -7.05) * mm, v(39.38, 1.83) * mm, v(37.1, 10.7) * mm]});
            skFitSpline(sketch, "E1209.0.3", {"points": [v(37.1, 10.7) * mm, v(36.32, 13.77) * mm, v(35.32, 15.47) * mm, v(32.84, 17.99) * mm]});
            skFitSpline(sketch, "E1209.0.4", {"points": [v(32.84, 17.99) * mm, v(30.39, 20.47) * mm, v(27.86, 21.87) * mm, v(24.53, 22.58) * mm]});
            skFitSpline(sketch, "E1209.0.5", {"points": [v(24.53, 22.58) * mm, v(22.06, 23.1) * mm, v(20.54, 23.1) * mm, v(18.05, 22.58) * mm]});
            skFitSpline(sketch, "E1209.0.6", {"points": [v(18.05, 22.58) * mm, v(10.66, 21.03) * mm, v(4.94, 14.07) * mm, v(4.94, 6.63) * mm]});
            skFitSpline(sketch, "E1210.0.0", {"points": [v(11.28, 9.45) * mm, v(11.85, 7.84) * mm, v(13.21, 5.5) * mm, v(14.01, 4.74) * mm]});
            skFitSpline(sketch, "E1210.0.1", {"points": [v(14.01, 4.74) * mm, v(15.5, 3.35) * mm, v(17.48, 2.88) * mm, v(19.16, 3.52) * mm]});
            skFitSpline(sketch, "E1210.0.2", {"points": [v(19.16, 3.52) * mm, v(20.1, 3.88) * mm, v(20.14, 5.17) * mm, v(19.25, 6.92) * mm]});
            skFitSpline(sketch, "E1210.0.3", {"points": [v(19.25, 6.92) * mm, v(18.25, 8.9) * mm, v(16.16, 9.99) * mm, v(12.44, 10.45) * mm]});
            skLineSegment(sketch, "E1210.0.4", {"start": v(12.44, 10.45) * mm, "end": v(10.86, 10.65) * mm});
            skLineSegment(sketch, "E1210.0.5", {"start": v(10.86, 10.65) * mm, "end": v(11.28, 9.45) * mm});
            skFitSpline(sketch, "E1210.1.0", {"points": [v(20.08, 9.44) * mm, v(20.63, 8.83) * mm, v(21.18, 8.33) * mm, v(21.3, 8.33) * mm]});
            skFitSpline(sketch, "E1210.1.1", {"points": [v(21.3, 8.33) * mm, v(21.43, 8.33) * mm, v(21.92, 8.65) * mm, v(22.38, 9.04) * mm]});
            skFitSpline(sketch, "E1210.1.2", {"points": [v(22.38, 9.04) * mm, v(23.57, 10.04) * mm, v(24.24, 11.93) * mm, v(24.02, 13.62) * mm]});
            skFitSpline(sketch, "E1210.1.3", {"points": [v(24.02, 13.62) * mm, v(23.81, 15.17) * mm, v(21.68, 19.71) * mm, v(21.27, 19.46) * mm]});
            skFitSpline(sketch, "E1210.1.4", {"points": [v(21.27, 19.46) * mm, v(20.76, 19.14) * mm, v(19.02, 15.36) * mm, v(18.76, 14) * mm]});
            skFitSpline(sketch, "E1210.1.5", {"points": [v(18.76, 14) * mm, v(18.42, 12.2) * mm, v(18.81, 10.84) * mm, v(20.08, 9.44) * mm]});
            skFitSpline(sketch, "E1210.2.0", {"points": [v(18.12, -6.32) * mm, v(20, -6.77) * mm, v(23.39, -6.67) * mm, v(25.18, -6.1) * mm]});
            skLineSegment(sketch, "E1210.2.1", {"start": v(25.18, -6.1) * mm, "end": v(25.18, -6.1) * mm});
            skFitSpline(sketch, "E1210.2.2", {"points": [v(25.18, -6.1) * mm, v(28.13, -5.2) * mm, v(30.22, -3.35) * mm, v(30.76, -1.2) * mm]});
            skLineSegment(sketch, "E1210.2.3", {"start": v(30.76, -1.2) * mm, "end": v(30.95, -0.42) * mm});
            skLineSegment(sketch, "E1210.2.4", {"start": v(30.95, -0.42) * mm, "end": v(26.97, -0.42) * mm});
            skLineSegment(sketch, "E1210.2.5", {"start": v(26.97, -0.42) * mm, "end": v(22.99, -0.42) * mm});
            skLineSegment(sketch, "E1210.2.6", {"start": v(22.99, -0.42) * mm, "end": v(22.99, 1.54) * mm});
            skLineSegment(sketch, "E1210.2.7", {"start": v(22.99, 1.54) * mm, "end": v(22.99, 3.5) * mm});
            skLineSegment(sketch, "E1210.2.8", {"start": v(22.99, 3.5) * mm, "end": v(24.36, 3.34) * mm});
            skFitSpline(sketch, "E1210.2.9", {"points": [v(24.36, 3.34) * mm, v(26.16, 3.13) * mm, v(27.45, 3.58) * mm, v(28.7, 4.87) * mm]});
            skFitSpline(sketch, "E1210.2.10", {"points": [v(28.7, 4.87) * mm, v(29.66, 5.88) * mm, v(31.21, 8.59) * mm, v(31.6, 9.95) * mm]});
            skFitSpline(sketch, "E1210.2.11", {"points": [v(31.6, 9.95) * mm, v(31.82, 10.73) * mm, v(31.46, 10.76) * mm, v(28.64, 10.16) * mm]});
            skFitSpline(sketch, "E1210.2.12", {"points": [v(28.64, 10.16) * mm, v(26.18, 9.64) * mm, v(25.3, 9.2) * mm, v(24.18, 7.93) * mm]});
            skFitSpline(sketch, "E1210.2.13", {"points": [v(24.18, 7.93) * mm, v(23.03, 6.63) * mm, v(22.71, 5.36) * mm, v(22.7, 2.2) * mm]});
            skLineSegment(sketch, "E1210.2.14", {"start": v(22.7, 2.2) * mm, "end": v(22.7, -0.41) * mm});
            skLineSegment(sketch, "E1210.2.15", {"start": v(22.7, -0.41) * mm, "end": v(17.23, -0.49) * mm});
            skLineSegment(sketch, "E1210.2.16", {"start": v(17.23, -0.49) * mm, "end": v(11.75, -0.56) * mm});
            skLineSegment(sketch, "E1210.2.17", {"start": v(11.75, -0.56) * mm, "end": v(12.13, -1.66) * mm});
            skFitSpline(sketch, "E1210.2.18", {"points": [v(12.13, -1.66) * mm, v(12.82, -3.68) * mm, v(15.4, -5.68) * mm, v(18.12, -6.32) * mm]});
            skFitSpline(sketch, "E1211.0", {"points": [v(-11.63, 3.74) * mm, v(-11.44, 4.04) * mm, v(-12.73, 10.63) * mm, v(-13.42, 12.91) * mm]});
            skLineSegment(sketch, "E1211.1.0", {"start": v(-23.32, -5.16) * mm, "end": v(-19.5, -5.08) * mm});
            skLineSegment(sketch, "E1211.1.1", {"start": v(-19.5, -5.08) * mm, "end": v(-19.3, -4.1) * mm});
            skFitSpline(sketch, "E1211.1.2", {"points": [v(-19.3, -4.1) * mm, v(-19.04, -2.8) * mm, v(-18.4, -2.4) * mm, v(-16.54, -2.4) * mm]});
            skFitSpline(sketch, "E1211.1.3", {"points": [v(-16.54, -2.4) * mm, v(-15.68, -2.4) * mm, v(-14.82, -2.3) * mm, v(-14.63, -2.18) * mm]});
            skFitSpline(sketch, "E1211.1.4", {"points": [v(-14.63, -2.18) * mm, v(-14.11, -1.84) * mm, v(-13.7, -0.5) * mm, v(-13.7, 0.85) * mm]});
            skFitSpline(sketch, "E1211.1.5", {"points": [v(-13.7, 0.85) * mm, v(-13.7, 2.65) * mm, v(-13.3, 3.53) * mm, v(-12.45, 3.53) * mm]});
            skFitSpline(sketch, "E1211.1.6", {"points": [v(-12.45, 3.53) * mm, v(-12.07, 3.53) * mm, v(-11.7, 3.62) * mm, v(-11.63, 3.74) * mm]});
            skFitSpline(sketch, "E1211.1.7", {"points": [v(-11.63, 3.74) * mm, v(-11.44, 4.04) * mm, v(-12.73, 10.63) * mm, v(-13.42, 12.91) * mm]});
            skFitSpline(sketch, "E1211.1.8", {"points": [v(-13.42, 12.91) * mm, v(-14.08, 15.1) * mm, v(-15.15, 16.35) * mm, v(-17.27, 17.39) * mm]});
            skFitSpline(sketch, "E1211.1.9", {"points": [v(-17.27, 17.39) * mm, v(-18.48, 17.99) * mm, v(-19.02, 18.06) * mm, v(-22.02, 18.06) * mm]});
            skFitSpline(sketch, "E1211.1.10", {"points": [v(-22.02, 18.06) * mm, v(-24.96, 18.06) * mm, v(-25.6, 17.97) * mm, v(-26.86, 17.4) * mm]});
            skFitSpline(sketch, "E1211.1.11", {"points": [v(-26.86, 17.4) * mm, v(-29.59, 16.17) * mm, v(-30.75, 14.3) * mm, v(-31.1, 10.59) * mm]});
            skFitSpline(sketch, "E1211.1.12", {"points": [v(-31.1, 10.59) * mm, v(-31.29, 8.53) * mm, v(-30.84, 5.32) * mm, v(-30.2, 4.07) * mm]});
            skFitSpline(sketch, "E1211.1.13", {"points": [v(-30.2, 4.07) * mm, v(-29.98, 3.64) * mm, v(-29.28, 2.7) * mm, v(-28.66, 1.98) * mm]});
            skLineSegment(sketch, "E1211.1.14", {"start": v(-28.66, 1.98) * mm, "end": v(-27.53, 0.67) * mm});
            skLineSegment(sketch, "E1211.1.15", {"start": v(-27.53, 0.67) * mm, "end": v(-27.53, -2.09) * mm});
            skFitSpline(sketch, "E1211.1.16", {"points": [v(-27.53, -2.09) * mm, v(-27.53, -3.6) * mm, v(-27.44, -4.93) * mm, v(-27.33, -5.04) * mm]});
            skFitSpline(sketch, "E1211.1.17", {"points": [v(-27.33, -5.04) * mm, v(-27.22, -5.15) * mm, v(-25.42, -5.2) * mm, v(-23.32, -5.16) * mm]});
            skFitSpline(sketch, "E1212.0.0", {"points": [v(-23.86, 4.84) * mm, v(-23.86, 4) * mm, v(-23.35, 3.53) * mm, v(-22.45, 3.53) * mm]});
            skFitSpline(sketch, "E1212.0.1", {"points": [v(-22.45, 3.53) * mm, v(-22.04, 3.53) * mm, v(-21.56, 3.68) * mm, v(-21.38, 3.87) * mm]});
            skFitSpline(sketch, "E1212.0.2", {"points": [v(-21.38, 3.87) * mm, v(-21.19, 4.05) * mm, v(-21.04, 4.44) * mm, v(-21.04, 4.73) * mm]});
            skFitSpline(sketch, "E1212.0.3", {"points": [v(-21.04, 4.73) * mm, v(-21.04, 5.01) * mm, v(-20.8, 5.59) * mm, v(-20.49, 6) * mm]});
            skFitSpline(sketch, "E1212.0.4", {"points": [v(-20.49, 6) * mm, v(-19.12, 7.92) * mm, v(-20.16, 10.3) * mm, v(-22.37, 10.3) * mm]});
            skFitSpline(sketch, "E1212.0.5", {"points": [v(-22.37, 10.3) * mm, v(-23.7, 10.3) * mm, v(-24.4, 9.86) * mm, v(-24.87, 8.73) * mm]});
            skFitSpline(sketch, "E1212.0.6", {"points": [v(-24.87, 8.73) * mm, v(-25.22, 7.9) * mm, v(-25.22, 7.63) * mm, v(-24.88, 6.8) * mm]});
            skFitSpline(sketch, "E1212.0.7", {"points": [v(-24.88, 6.8) * mm, v(-24.66, 6.28) * mm, v(-24.34, 5.77) * mm, v(-24.17, 5.66) * mm]});
            skFitSpline(sketch, "E1212.0.8", {"points": [v(-24.17, 5.66) * mm, v(-24, 5.56) * mm, v(-23.86, 5.19) * mm, v(-23.86, 4.84) * mm]});
            skFitSpline(sketch, "E1213.0.0", {"points": [v(-23.01, 14.25) * mm, v(-23.01, 13.31) * mm, v(-22.92, 13.12) * mm, v(-22.45, 13.12) * mm]});
            skFitSpline(sketch, "E1213.0.1", {"points": [v(-22.45, 13.12) * mm, v(-21.98, 13.12) * mm, v(-21.88, 13.31) * mm, v(-21.88, 14.25) * mm]});
            skFitSpline(sketch, "E1213.0.2", {"points": [v(-21.88, 14.25) * mm, v(-21.88, 15.2) * mm, v(-21.98, 15.38) * mm, v(-22.45, 15.38) * mm]});
            skFitSpline(sketch, "E1213.0.3", {"points": [v(-22.45, 15.38) * mm, v(-22.92, 15.38) * mm, v(-23.01, 15.2) * mm, v(-23.01, 14.25) * mm]});
            skFitSpline(sketch, "E1213.1", {"points": [v(-26.65, 13.85) * mm, v(-26.2, 14.12) * mm, v(-25.16, 12.98) * mm, v(-25.36, 12.44) * mm]});
            skPoint(sketch, "E1213.2", {"position": v(-25.36, 12.44) * mm});
            skFitSpline(sketch, "E1213.3.0", {"points": [v(-26.62, 12.33) * mm, v(-26.15, 11.86) * mm, v(-25.57, 11.91) * mm, v(-25.36, 12.44) * mm]});
            skFitSpline(sketch, "E1213.3.1", {"points": [v(-25.36, 12.44) * mm, v(-25.16, 12.98) * mm, v(-26.2, 14.12) * mm, v(-26.65, 13.85) * mm]});
            skFitSpline(sketch, "E1213.3.2", {"points": [v(-26.65, 13.85) * mm, v(-27.06, 13.6) * mm, v(-27.05, 12.76) * mm, v(-26.62, 12.33) * mm]});
            skFitSpline(sketch, "E1213.4.0", {"points": [v(-19.63, 12.64) * mm, v(-19.63, 12.37) * mm, v(-19.37, 12.27) * mm, v(-18.85, 12.33) * mm]});
            skFitSpline(sketch, "E1213.4.1", {"points": [v(-18.85, 12.33) * mm, v(-18.24, 12.4) * mm, v(-18.05, 12.59) * mm, v(-17.98, 13.2) * mm]});
            skFitSpline(sketch, "E1213.4.2", {"points": [v(-17.98, 13.2) * mm, v(-17.93, 13.67) * mm, v(-18.03, 13.97) * mm, v(-18.24, 13.97) * mm]});
            skFitSpline(sketch, "E1213.4.3", {"points": [v(-18.24, 13.97) * mm, v(-18.74, 13.97) * mm, v(-19.63, 13.11) * mm, v(-19.63, 12.64) * mm]});
            skFitSpline(sketch, "E1214.0.0", {"points": [v(-32.91, -43.9) * mm, v(-30.85, -45.96) * mm, v(-29.24, -47) * mm, v(-26.78, -47.88) * mm]});
            skFitSpline(sketch, "E1214.0.1", {"points": [v(-26.78, -47.88) * mm, v(-23.57, -49) * mm, v(-19.23, -48.98) * mm, v(-16.12, -47.82) * mm]});
            skFitSpline(sketch, "E1214.0.2", {"points": [v(-16.12, -47.82) * mm, v(-11.18, -45.97) * mm, v(-7.23, -41.5) * mm, v(-5.9, -36.27) * mm]});
            skFitSpline(sketch, "E1214.0.3", {"points": [v(-5.9, -36.27) * mm, v(-5.29, -33.8) * mm, v(-5.5, -29.47) * mm, v(-6.36, -27.03) * mm]});
            skFitSpline(sketch, "E1214.0.4", {"points": [v(-6.36, -27.03) * mm, v(-8.6, -20.64) * mm, v(-14.77, -16.18) * mm, v(-21.42, -16.16) * mm]});
            skFitSpline(sketch, "E1214.0.5", {"points": [v(-21.42, -16.16) * mm, v(-25.68, -16.15) * mm, v(-29.35, -17.6) * mm, v(-32.46, -20.5) * mm]});
            skFitSpline(sketch, "E1214.0.6", {"points": [v(-32.46, -20.5) * mm, v(-39.17, -26.79) * mm, v(-39.37, -37.44) * mm, v(-32.91, -43.9) * mm]});
            skFitSpline(sketch, "E1215.0.0", {"points": [v(-30.56, -37.44) * mm, v(-28.9, -41.1) * mm, v(-25.4, -43.47) * mm, v(-21.52, -43.57) * mm]});
            skFitSpline(sketch, "E1215.0.1", {"points": [v(-21.52, -43.57) * mm, v(-20.93, -43.59) * mm, v(-19.67, -43.34) * mm, v(-18.7, -43.01) * mm]});
            skFitSpline(sketch, "E1215.0.2", {"points": [v(-18.7, -43.01) * mm, v(-11.6, -40.62) * mm, v(-9.47, -32.06) * mm, v(-14.63, -26.74) * mm]});
            skFitSpline(sketch, "E1215.0.3", {"points": [v(-14.63, -26.74) * mm, v(-15.9, -25.43) * mm, v(-16.25, -25.31) * mm, v(-16.92, -25.98) * mm]});
            skFitSpline(sketch, "E1215.0.4", {"points": [v(-16.92, -25.98) * mm, v(-17.58, -26.64) * mm, v(-17.49, -26.95) * mm, v(-16.14, -28.6) * mm]});
            skFitSpline(sketch, "E1215.0.5", {"points": [v(-16.14, -28.6) * mm, v(-14.75, -30.3) * mm, v(-14.26, -31.6) * mm, v(-14.26, -33.64) * mm]});
            skFitSpline(sketch, "E1215.0.6", {"points": [v(-14.26, -33.64) * mm, v(-14.26, -36.4) * mm, v(-15.67, -38.8) * mm, v(-18.03, -40.11) * mm]});
            skFitSpline(sketch, "E1215.0.7", {"points": [v(-18.03, -40.11) * mm, v(-19.27, -40.8) * mm, v(-19.8, -40.92) * mm, v(-21.6, -40.91) * mm]});
            skFitSpline(sketch, "E1215.0.8", {"points": [v(-21.6, -40.91) * mm, v(-23.22, -40.9) * mm, v(-23.99, -40.76) * mm, v(-24.85, -40.3) * mm]});
            skFitSpline(sketch, "E1215.0.9", {"points": [v(-24.85, -40.3) * mm, v(-29.26, -37.95) * mm, v(-30.25, -32.3) * mm, v(-26.94, -28.47) * mm]});
            skFitSpline(sketch, "E1215.0.10", {"points": [v(-26.94, -28.47) * mm, v(-25.71, -27.06) * mm, v(-25.55, -26.27) * mm, v(-26.4, -25.82) * mm]});
            skFitSpline(sketch, "E1215.0.11", {"points": [v(-26.4, -25.82) * mm, v(-27.12, -25.44) * mm, v(-27.72, -25.75) * mm, v(-28.94, -27.14) * mm]});
            skFitSpline(sketch, "E1215.0.12", {"points": [v(-28.94, -27.14) * mm, v(-31.39, -29.92) * mm, v(-32.05, -34.14) * mm, v(-30.56, -37.44) * mm]});
            skLineSegment(sketch, "E1216.0.0", {"start": v(-21.32, -30.56) * mm, "end": v(-20.61, -30.48) * mm});
            skLineSegment(sketch, "E1216.0.1", {"start": v(-20.61, -30.48) * mm, "end": v(-20.54, -26.22) * mm});
            skFitSpline(sketch, "E1216.0.2", {"points": [v(-20.54, -26.22) * mm, v(-20.47, -22.64) * mm, v(-20.53, -21.9) * mm, v(-20.9, -21.59) * mm]});
            skFitSpline(sketch, "E1216.0.3", {"points": [v(-20.9, -21.59) * mm, v(-21.23, -21.3) * mm, v(-21.5, -21.3) * mm, v(-22.03, -21.54) * mm]});
            skFitSpline(sketch, "E1216.0.4", {"points": [v(-22.03, -21.54) * mm, v(-22.73, -21.86) * mm, v(-22.73, -21.88) * mm, v(-22.73, -25.9) * mm]});
            skFitSpline(sketch, "E1216.0.5", {"points": [v(-22.73, -25.9) * mm, v(-22.73, -30.25) * mm, v(-22.6, -30.7) * mm, v(-21.32, -30.56) * mm]});
            skFitSpline(sketch, "E1217.0.0", {"points": [v(21.14, -16.16) * mm, v(11.14, -16.2) * mm, v(3.3, -25.76) * mm, v(5.32, -35.42) * mm]});
            skFitSpline(sketch, "E1217.0.1", {"points": [v(5.32, -35.42) * mm, v(7.42, -45.46) * mm, v(17.64, -51.26) * mm, v(27.02, -47.73) * mm]});
            skFitSpline(sketch, "E1217.0.2", {"points": [v(27.02, -47.73) * mm, v(34.74, -44.82) * mm, v(39.11, -36.66) * mm, v(37.23, -28.67) * mm]});
            skFitSpline(sketch, "E1217.0.3", {"points": [v(37.23, -28.67) * mm, v(36.18, -24.21) * mm, v(32.7, -19.85) * mm, v(28.63, -17.87) * mm]});
            skFitSpline(sketch, "E1217.0.4", {"points": [v(28.63, -17.87) * mm, v(25.96, -16.58) * mm, v(24.06, -16.14) * mm, v(21.14, -16.16) * mm]});
            skFitSpline(sketch, "E1218.0.0", {"points": [v(21.14, -16.16) * mm, v(11.14, -16.2) * mm, v(3.3, -25.76) * mm, v(5.32, -35.42) * mm]});
            skFitSpline(sketch, "E1218.0.1", {"points": [v(5.32, -35.42) * mm, v(7.42, -45.46) * mm, v(17.64, -51.26) * mm, v(27.02, -47.73) * mm]});
            skFitSpline(sketch, "E1218.0.2", {"points": [v(27.02, -47.73) * mm, v(34.74, -44.82) * mm, v(39.11, -36.66) * mm, v(37.23, -28.67) * mm]});
            skFitSpline(sketch, "E1218.0.3", {"points": [v(37.23, -28.67) * mm, v(36.18, -24.21) * mm, v(32.7, -19.85) * mm, v(28.63, -17.87) * mm]});
            skFitSpline(sketch, "E1218.0.4", {"points": [v(28.63, -17.87) * mm, v(25.96, -16.58) * mm, v(24.06, -16.14) * mm, v(21.14, -16.16) * mm]});
            skFitSpline(sketch, "E1219.0.0", {"points": [v(17.9, -22.64) * mm, v(17.9, -22.91) * mm, v(18.73, -23) * mm, v(21.3, -23) * mm]});
            skFitSpline(sketch, "E1219.0.1", {"points": [v(21.3, -23) * mm, v(25.22, -23) * mm, v(25.3, -22.93) * mm, v(23.53, -20.92) * mm]});
            skFitSpline(sketch, "E1219.0.2", {"points": [v(23.53, -20.92) * mm, v(21.8, -18.97) * mm, v(21.28, -18.95) * mm, v(19.44, -20.77) * mm]});
            skFitSpline(sketch, "E1219.0.3", {"points": [v(19.44, -20.77) * mm, v(18.6, -21.6) * mm, v(17.9, -22.44) * mm, v(17.9, -22.64) * mm]});
            skFitSpline(sketch, "E1220.0.0", {"points": [v(18.27, -43.83) * mm, v(18.45, -44.05) * mm, v(19.02, -44.16) * mm, v(19.72, -44.1) * mm]});
            skLineSegment(sketch, "E1220.0.1", {"start": v(19.72, -44.1) * mm, "end": v(20.87, -44.03) * mm});
            skLineSegment(sketch, "E1220.0.2", {"start": v(20.87, -44.03) * mm, "end": v(20.95, -40.07) * mm});
            skFitSpline(sketch, "E1220.0.3", {"points": [v(20.95, -40.07) * mm, v(20.99, -37.9) * mm, v(21.11, -35.93) * mm, v(21.23, -35.7) * mm]});
            skFitSpline(sketch, "E1220.0.4", {"points": [v(21.23, -35.7) * mm, v(21.34, -35.47) * mm, v(21.5, -37.25) * mm, v(21.58, -39.65) * mm]});
            skLineSegment(sketch, "E1220.0.5", {"start": v(21.58, -39.65) * mm, "end": v(21.72, -44.03) * mm});
            skLineSegment(sketch, "E1220.0.6", {"start": v(21.72, -44.03) * mm, "end": v(22.99, -44.03) * mm});
            skFitSpline(sketch, "E1220.0.7", {"points": [v(22.99, -44.03) * mm, v(24.22, -44.03) * mm, v(24.28, -43.98) * mm, v(24.86, -42.76) * mm]});
            skFitSpline(sketch, "E1220.0.8", {"points": [v(24.86, -42.76) * mm, v(25.8, -40.8) * mm, v(27.18, -35.55) * mm, v(27.48, -32.82) * mm]});
            skFitSpline(sketch, "E1220.0.9", {"points": [v(27.48, -32.82) * mm, v(27.81, -29.9) * mm, v(27.5, -27.49) * mm, v(26.52, -25.33) * mm]});
            skLineSegment(sketch, "E1220.0.10", {"start": v(26.52, -25.33) * mm, "end": v(25.84, -23.85) * mm});
            skLineSegment(sketch, "E1220.0.11", {"start": v(25.84, -23.85) * mm, "end": v(21.35, -23.85) * mm});
            skLineSegment(sketch, "E1220.0.12", {"start": v(21.35, -23.85) * mm, "end": v(16.86, -23.85) * mm});
            skLineSegment(sketch, "E1220.0.13", {"start": v(16.86, -23.85) * mm, "end": v(16.04, -25.61) * mm});
            skFitSpline(sketch, "E1220.0.14", {"points": [v(16.04, -25.61) * mm, v(15.28, -27.26) * mm, v(15.23, -27.6) * mm, v(15.24, -30.9) * mm]});
            skFitSpline(sketch, "E1220.0.15", {"points": [v(15.24, -30.9) * mm, v(15.24, -33.63) * mm, v(15.38, -34.94) * mm, v(15.86, -36.69) * mm]});
            skFitSpline(sketch, "E1220.0.16", {"points": [v(15.86, -36.69) * mm, v(16.7, -39.78) * mm, v(17.92, -43.38) * mm, v(18.27, -43.83) * mm]});
            skFitSpline(sketch, "E1221.0.0", {"points": [v(20.87, -26.79) * mm, v(19.87, -27.04) * mm, v(19.5, -28.54) * mm, v(20.23, -29.42) * mm]});
            skFitSpline(sketch, "E1221.0.1", {"points": [v(20.23, -29.42) * mm, v(20.67, -29.96) * mm, v(22, -29.84) * mm, v(22.56, -29.22) * mm]});
            skFitSpline(sketch, "E1221.0.2", {"points": [v(22.56, -29.22) * mm, v(23.55, -28.12) * mm, v(22.37, -26.4) * mm, v(20.87, -26.79) * mm]});
            skFitSpline(sketch, "E1222.0.0", {"points": [v(18.76, -27.37) * mm, v(18.14, -29.25) * mm, v(19.14, -30.73) * mm, v(21.32, -31.15) * mm]});
            skFitSpline(sketch, "E1222.0.1", {"points": [v(21.32, -31.15) * mm, v(21.42, -31.17) * mm, v(21.9, -31.04) * mm, v(22.4, -30.87) * mm]});
            skFitSpline(sketch, "E1222.0.2", {"points": [v(22.4, -30.87) * mm, v(24.2, -30.24) * mm, v(24.7, -27.76) * mm, v(23.3, -26.36) * mm]});
            skFitSpline(sketch, "E1222.0.3", {"points": [v(23.3, -26.36) * mm, v(21.82, -24.9) * mm, v(19.4, -25.43) * mm, v(18.76, -27.37) * mm]});
            skFitSpline(sketch, "E1223.0.0", {"points": [v(11.92, -42.38) * mm, v(11.92, -44.24) * mm, v(12.07, -45.01) * mm, v(12.44, -45.01) * mm]});
            skFitSpline(sketch, "E1223.0.1", {"points": [v(12.44, -45.01) * mm, v(12.52, -45.01) * mm, v(13.41, -44.42) * mm, v(14.42, -43.7) * mm]});
            skFitSpline(sketch, "E1223.0.2", {"points": [v(14.42, -43.7) * mm, v(15.69, -42.8) * mm, v(16.22, -42.25) * mm, v(16.13, -41.94) * mm]});
            skFitSpline(sketch, "E1223.0.3", {"points": [v(16.13, -41.94) * mm, v(16.05, -41.69) * mm, v(15.63, -40.23) * mm, v(15.2, -38.7) * mm]});
            skLineSegment(sketch, "E1223.0.4", {"start": v(15.2, -38.7) * mm, "end": v(14.4, -35.92) * mm});
            skLineSegment(sketch, "E1223.0.5", {"start": v(14.4, -35.92) * mm, "end": v(13.47, -36.99) * mm});
            skFitSpline(sketch, "E1223.0.6", {"points": [v(13.47, -36.99) * mm, v(12.33, -38.3) * mm, v(11.92, -39.74) * mm, v(11.92, -42.38) * mm]});
            skPoint(sketch, "E1224.0", {"position": v(27.22, -42.94) * mm});
            skFitSpline(sketch, "E1225.0.0", {"points": [v(28.25, -43.7) * mm, v(29.3, -44.42) * mm, v(30.25, -45.01) * mm, v(30.37, -45.01) * mm]});
            skFitSpline(sketch, "E1225.0.1", {"points": [v(30.37, -45.01) * mm, v(30.48, -45.01) * mm, v(30.66, -44.43) * mm, v(30.77, -43.72) * mm]});
            skFitSpline(sketch, "E1225.0.2", {"points": [v(30.77, -43.72) * mm, v(31.03, -41.97) * mm, v(30.72, -39.55) * mm, v(30.06, -38.29) * mm]});
            skFitSpline(sketch, "E1225.0.3", {"points": [v(30.06, -38.29) * mm, v(29.45, -37.1) * mm, v(28.27, -35.76) * mm, v(28.18, -36.15) * mm]});
            skFitSpline(sketch, "E1225.0.4", {"points": [v(28.18, -36.15) * mm, v(27.97, -37.03) * mm, v(26.67, -41.56) * mm, v(26.53, -41.94) * mm]});
            skFitSpline(sketch, "E1225.0.5", {"points": [v(26.53, -41.94) * mm, v(26.4, -42.26) * mm, v(26.87, -42.74) * mm, v(28.25, -43.7) * mm]});
            skFitSpline(sketch, "E1226.0.0", {"points": [v(28.25, -43.7) * mm, v(29.3, -44.42) * mm, v(30.25, -45.01) * mm, v(30.37, -45.01) * mm]});
            skFitSpline(sketch, "E1226.0.1", {"points": [v(30.37, -45.01) * mm, v(30.48, -45.01) * mm, v(30.66, -44.43) * mm, v(30.77, -43.72) * mm]});
            skFitSpline(sketch, "E1226.0.2", {"points": [v(30.77, -43.72) * mm, v(31.03, -41.97) * mm, v(30.72, -39.55) * mm, v(30.06, -38.29) * mm]});
            skFitSpline(sketch, "E1226.0.3", {"points": [v(30.06, -38.29) * mm, v(29.45, -37.1) * mm, v(28.27, -35.76) * mm, v(28.18, -36.15) * mm]});
            skFitSpline(sketch, "E1226.0.4", {"points": [v(28.18, -36.15) * mm, v(27.97, -37.03) * mm, v(26.67, -41.56) * mm, v(26.53, -41.94) * mm]});
            skFitSpline(sketch, "E1226.0.5", {"points": [v(26.53, -41.94) * mm, v(26.4, -42.26) * mm, v(26.87, -42.74) * mm, v(28.25, -43.7) * mm]});
            skFitSpline(sketch, "E1227", {"points": [v(-24.1, 3.67) * mm, v(-24.36, 4.79) * mm, v(-24.63, 5.46) * mm, v(-25.34, 6.62) * mm, v(-25.35, 8.87) * mm, v(-22.4, 10.8) * mm, v(-19.46, 8.66) * mm, v(-20, 5.92) * mm, v(-20.54, 4.66) * mm, v(-20.68, 3.67) * mm], "startDerivative": vector(-1.53, 14) * mm, "endDerivative": vector(-2.36, -12.1) * mm});
            skFitSpline(sketch, "E1228", {"points": [v(-24.1, 3.67) * mm, v(-23.84, 3.4) * mm, v(-23.7, 2.45) * mm, v(-21.2, 2.44) * mm, v(-20.87, 3.03) * mm, v(-20.68, 3.67) * mm], "startDerivative": vector(2.85, -1.49) * mm, "endDerivative": vector(3.43, 1.52) * mm});
            skSolve(sketch);
        }
        {
            var Q0;
            Q0=makeQuery(id+"F2.imprint","IMPRINT",FACE,{"disambiguationData":[TD([[makeQuery(id+"F2.imprint","IMPRINT",EDGE,{"derivedFrom":sQuery(id+"F2.wireOp",EDGE,"E1210.0.0")}),1.0]])]});
            var Q1;
            Q1=makeQuery(id+"F2.imprint","IMPRINT",FACE,{"disambiguationData":[TD([[makeQuery(id+"F2.imprint","IMPRINT",EDGE,{"derivedFrom":sQuery(id+"F2.wireOp",EDGE,"E1210.1.0")}),1.0]])]});
            var Q2;
            Q2=makeQuery(id+"F2.imprint","IMPRINT",FACE,{"disambiguationData":[TD([[makeQuery(id+"F2.imprint","IMPRINT",EDGE,{"derivedFrom":sQuery(id+"F2.wireOp",EDGE,"E1210.2.0")}),1.0]])]});
            var Q3;
            Q3=makeQuery(id+"F2.imprint","IMPRINT",FACE,{"disambiguationData":[TD([[makeQuery(id+"F2.imprint","IMPRINT",EDGE,{"derivedFrom":sQuery(id+"F2.wireOp",EDGE,"E1219.0.0")}),1.0]])]});
            var Q4;
            Q4=makeQuery(id+"F2.imprint","IMPRINT",FACE,{"disambiguationData":[TD([[makeQuery(id+"F2.imprint","IMPRINT",EDGE,{"derivedFrom":sQuery(id+"F2.wireOp",EDGE,"E1220.0.0")}),1.0]])]});
            var Q5;
            Q5=makeQuery(id+"F2.imprint","IMPRINT",FACE,{"disambiguationData":[TD([[makeQuery(id+"F2.imprint","IMPRINT",EDGE,{"derivedFrom":sQuery(id+"F2.wireOp",EDGE,"E1221.0.0")}),1.0]])]});
            var Q6;
            Q6=makeQuery(id+"F2.imprint","IMPRINT",FACE,{"disambiguationData":[TD([[makeQuery(id+"F2.imprint","IMPRINT",EDGE,{"derivedFrom":sQuery(id+"F2.wireOp",EDGE,"E1223.0.0")}),1.0]])]});
            var Q7;
            Q7=makeQuery(id+"F2.imprint","IMPRINT",FACE,{"disambiguationData":[TD([[makeQuery(id+"F2.imprint","IMPRINT",EDGE,{"derivedFrom":sQuery(id+"F2.wireOp",EDGE,"E1226.0.0")}),1.0]])]});
            var Q8;
            Q8=makeQuery(id+"F2.imprint","IMPRINT",FACE,{"disambiguationData":[TD([[makeQuery(id+"F2.imprint","IMPRINT",EDGE,{"derivedFrom":sQuery(id+"F2.wireOp",EDGE,"E1215.0.0")}),1.0]])]});
            var Q9;
            Q9=makeQuery(id+"F2.imprint","IMPRINT",FACE,{"disambiguationData":[TD([[makeQuery(id+"F2.imprint","IMPRINT",EDGE,{"derivedFrom":sQuery(id+"F2.wireOp",EDGE,"E1216.0.0")}),1.0]])]});
            var Q10;
            Q10=makeQuery(id+"F2.imprint","IMPRINT",FACE,{"disambiguationData":[TD([[makeQuery(id+"F2.imprint","IMPRINT",EDGE,{"derivedFrom":sQuery(id+"F2.wireOp",EDGE,"E1212.0.0")}),1.0]])]});
            var Q11;
            Q11=makeQuery(id+"F2.imprint","IMPRINT",FACE,{"disambiguationData":[TD([[makeQuery(id+"F2.imprint","IMPRINT",EDGE,{"derivedFrom":sQuery(id+"F2.wireOp",EDGE,"E1211.1.0")}),1.0]])]});
            extrude(context, id + "F3", {"entities" : qUnion([Q0, Q1, Q2, Q3, Q4, Q5, Q6, Q7, Q8, Q9, Q10, Q11]), "depth" : 4 * mm});
        }
        {
            var Q0;
            Q0=makeQuery(id+"F2.imprint","IMPRINT",FACE,{"disambiguationData":[TD([[makeQuery(id+"F2.imprint","IMPRINT",EDGE,{"derivedFrom":sQuery(id+"F2.wireOp",EDGE,"E1214.0.0")}),1.0]])]});
            var Q1;
            Q1=makeQuery(id+"F2.imprint","IMPRINT",FACE,{"disambiguationData":[TD([[makeQuery(id+"F2.imprint","IMPRINT",EDGE,{"derivedFrom":sQuery(id+"F2.wireOp",EDGE,"E1208.0.0")}),1.0]])]});
            var Q2;
            Q2=makeQuery(id+"F2.imprint","IMPRINT",FACE,{"disambiguationData":[TD([[makeQuery(id+"F2.imprint","IMPRINT",EDGE,{"derivedFrom":sQuery(id+"F2.wireOp",EDGE,"E1218.0.0")}),1.0]])]});
            var Q3;
            Q3=makeQuery(id+"F2.imprint","IMPRINT",FACE,{"disambiguationData":[TD([[makeQuery(id+"F2.imprint","IMPRINT",EDGE,{"derivedFrom":sQuery(id+"F2.wireOp",EDGE,"E1209.0.0")}),1.0]])]});
            var Q4;
            Q4=makeQuery(id+"F2.imprint","IMPRINT",FACE,{"disambiguationData":[TD([[makeQuery(id+"F2.imprint","IMPRINT",EDGE,{"derivedFrom":sQuery(id+"F2.wireOp",EDGE,"E1213.3.0")}),1.0]])]});
            var Q5;
            Q5=makeQuery(id+"F2.imprint","IMPRINT",FACE,{"disambiguationData":[TD([[makeQuery(id+"F2.imprint","IMPRINT",EDGE,{"derivedFrom":sQuery(id+"F2.wireOp",EDGE,"E1213.0.0")}),1.0]])]});
            var Q6;
            Q6=makeQuery(id+"F2.imprint","IMPRINT",FACE,{"disambiguationData":[TD([[makeQuery(id+"F2.imprint","IMPRINT",EDGE,{"derivedFrom":sQuery(id+"F2.wireOp",EDGE,"E1213.4.0")}),1.0]])]});
            var Q7;
            Q7=makeQuery(id+"F2.imprint","IMPRINT",FACE,{"disambiguationData":[TD([[makeQuery(id+"F2.imprint","IMPRINT",EDGE,{"derivedFrom":sQuery(id+"F2.wireOp",EDGE,"E1212.0.0")}),-1.0]])]});
            var Q8;
            Q8=makeQuery(id+"F2.imprint","IMPRINT",FACE,{"disambiguationData":[TD([[makeQuery(id+"F2.imprint","IMPRINT",EDGE,{"derivedFrom":sQuery(id+"F2.wireOp",EDGE,"E1221.0.0")}),-1.0]])]});
            extrude(context, id + "F4", {"entities" : qUnion([Q0, Q1, Q2, Q3, Q4, Q5, Q6, Q7, Q8]), "depth" : 1.6 * mm});
        }
        {
            var Q0;
            Q0 = qSketchRegion(id + "F1", true);
            extrude(context, id + "F5", {"entities" : qUnion([Q0]), "oppositeDirection" : true, "depth" : 3 * mm});
        }
    });
